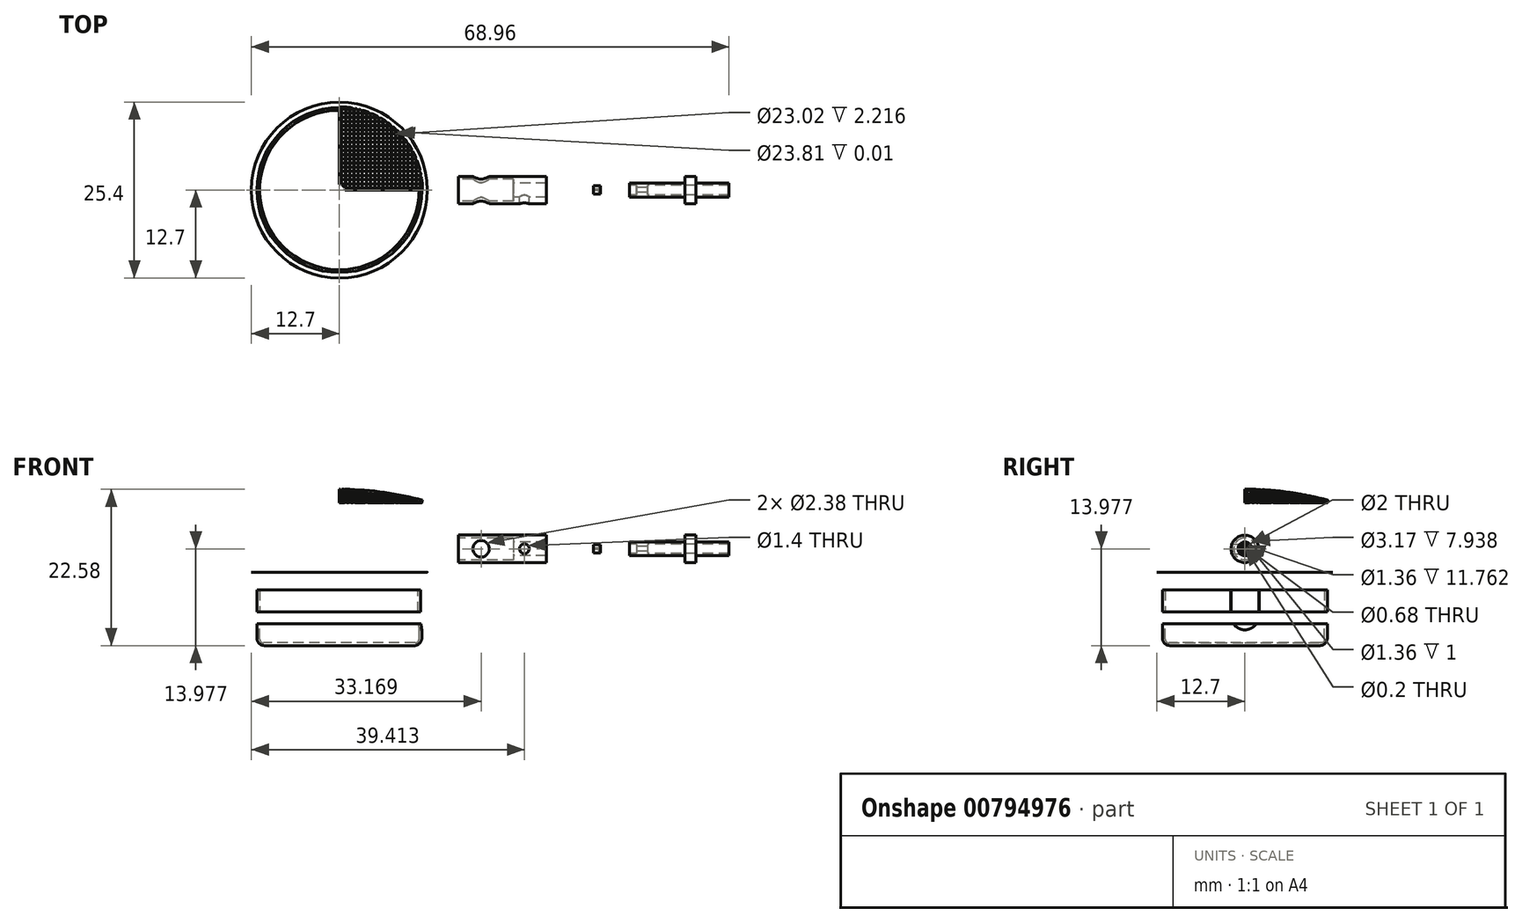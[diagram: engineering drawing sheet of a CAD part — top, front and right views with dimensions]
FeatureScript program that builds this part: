
annotation { "Feature Type Name" : "Feature", "Feature Type Description" : "" }
export const myFeature = defineFeature(function(context is Context, id is Id, definition is map)
    precondition{}
    {
        {
            var Q0;
            Q0=qCreatedBy(makeId("Right.planeOp"),FACE);
            cPlane(context, id + "F0", {"entities" : qUnion([Q0]), "cplaneType" : CPlaneType.OFFSET, "offset" : 15 * mm, "width" : 150 * mm, "height" : 150 * mm});
        }
        {
            var Q0;
            Q0=qCreatedBy(makeId("Front.planeOp"),FACE);
            var sketch = newSketch(context, id + "F1", { "sketchPlane" : qUnion([Q0])});
            skLineSegment(sketch, "E0", {"start": v(0, 0) * mm, "end": v(11.9, 0) * mm, "construction": true});
            skLineSegment(sketch, "E1", {"start": v(0, 0) * mm, "end": v(-11.9, 0) * mm, "construction": true});
            skLineSegment(sketch, "E2", {"start": v(0, 0) * mm, "end": v(0, 1.59) * mm, "construction": true});
            skArc(sketch, "E3", {"start": v(11.9, 0) * mm, "mid": v(0, 1.59) * mm, "end": v(-11.9, 0) * mm});
            skArc(sketch, "E4.0", {"start": v(12.01, 0.38) * mm, "mid": v(0, 1.98) * mm, "end": v(-12.01, 0.38) * mm});
            skLineSegment(sketch, "E5", {"start": v(12.01, 0.38) * mm, "end": v(11.9, 0) * mm});
            skLineSegment(sketch, "E6", {"start": v(0.8, 1.98) * mm, "end": v(0.8, 1.58) * mm});
            skSolve(sketch);
        }
        {
            var Q0;
            {var subQ0=sQuery(id+"F1.wireOp",EDGE,"E5");Q0=makeQuery(id+"F1.imprint","IMPRINT",FACE,{"disambiguationData":[TD([[makeQuery(id+"F1.imprint","IMPRINT",EDGE,{"derivedFrom":subQ0}),-1.0]])]});}
            var Q1;
            Q1=sQuery(id+"F1.wireOp",EDGE,"E2");
            revolve(context, id + "F2", {"surfaceOperationType" : NewSurfaceOperationType.NEW, "entities" : qUnion([Q0]), "axis" : qUnion([Q1]), "revolveType" : RevolveType.ONE_DIRECTION, "angle" : 90 * degree});
        }
        {
            var Q0;
            Q0=qCreatedBy(makeId("Top.planeOp"),FACE);
            var sketch = newSketch(context, id + "F3", { "sketchPlane" : qUnion([Q0])});
            skLineSegment(sketch, "E7.0.20.0", {"start": v(0.11, 11.5) * mm, "end": v(0.11, 11.9) * mm});
            skLineSegment(sketch, "E7.3.20.0", {"start": v(0.51, 11.5) * mm, "end": v(0.51, 11.9) * mm});
            skLineSegment(sketch, "E7.6.20.0", {"start": v(0.51, 11.9) * mm, "end": v(0.11, 11.9) * mm});
            skLineSegment(sketch, "E7.9.20.0", {"start": v(0.51, 11.5) * mm, "end": v(0.11, 11.5) * mm});
            skLineSegment(sketch, "E7.0.20.1", {"start": v(0.11, 10.9) * mm, "end": v(0.11, 11.3) * mm});
            skLineSegment(sketch, "E7.3.20.1", {"start": v(0.5, 10.9) * mm, "end": v(0.5, 11.3) * mm});
            skLineSegment(sketch, "E7.6.20.1", {"start": v(0.5, 11.3) * mm, "end": v(0.11, 11.3) * mm});
            skLineSegment(sketch, "E7.9.20.1", {"start": v(0.5, 10.9) * mm, "end": v(0.11, 10.9) * mm});
            skLineSegment(sketch, "E7.0.20.2", {"start": v(0.11, 10.3) * mm, "end": v(0.11, 10.7) * mm});
            skLineSegment(sketch, "E7.3.20.2", {"start": v(0.5, 10.3) * mm, "end": v(0.5, 10.7) * mm});
            skLineSegment(sketch, "E7.6.20.2", {"start": v(0.5, 10.7) * mm, "end": v(0.11, 10.7) * mm});
            skLineSegment(sketch, "E7.9.20.2", {"start": v(0.5, 10.3) * mm, "end": v(0.11, 10.3) * mm});
            skLineSegment(sketch, "E7.0.20.3", {"start": v(0.11, 9.7) * mm, "end": v(0.11, 10.1) * mm});
            skLineSegment(sketch, "E7.3.20.3", {"start": v(0.5, 9.7) * mm, "end": v(0.5, 10.1) * mm});
            skLineSegment(sketch, "E7.6.20.3", {"start": v(0.5, 10.1) * mm, "end": v(0.11, 10.1) * mm});
            skLineSegment(sketch, "E7.9.20.3", {"start": v(0.5, 9.7) * mm, "end": v(0.11, 9.7) * mm});
            skLineSegment(sketch, "E7.0.20.4", {"start": v(0.11, 9.1) * mm, "end": v(0.11, 9.5) * mm});
            skLineSegment(sketch, "E7.3.20.4", {"start": v(0.5, 9.1) * mm, "end": v(0.5, 9.5) * mm});
            skLineSegment(sketch, "E7.6.20.4", {"start": v(0.5, 9.5) * mm, "end": v(0.11, 9.5) * mm});
            skLineSegment(sketch, "E7.9.20.4", {"start": v(0.5, 9.1) * mm, "end": v(0.11, 9.1) * mm});
            skLineSegment(sketch, "E7.0.20.5", {"start": v(0.11, 8.5) * mm, "end": v(0.11, 8.9) * mm});
            skLineSegment(sketch, "E7.3.20.5", {"start": v(0.5, 8.5) * mm, "end": v(0.5, 8.9) * mm});
            skLineSegment(sketch, "E7.6.20.5", {"start": v(0.5, 8.9) * mm, "end": v(0.11, 8.9) * mm});
            skLineSegment(sketch, "E7.9.20.5", {"start": v(0.5, 8.5) * mm, "end": v(0.11, 8.5) * mm});
            skLineSegment(sketch, "E7.0.20.6", {"start": v(0.11, 7.9) * mm, "end": v(0.11, 8.3) * mm});
            skLineSegment(sketch, "E7.3.20.6", {"start": v(0.5, 7.9) * mm, "end": v(0.5, 8.3) * mm});
            skLineSegment(sketch, "E7.6.20.6", {"start": v(0.5, 8.3) * mm, "end": v(0.11, 8.3) * mm});
            skLineSegment(sketch, "E7.9.20.6", {"start": v(0.5, 7.9) * mm, "end": v(0.11, 7.9) * mm});
            skLineSegment(sketch, "E7.0.20.7", {"start": v(0.11, 7.3) * mm, "end": v(0.11, 7.7) * mm});
            skLineSegment(sketch, "E7.3.20.7", {"start": v(0.5, 7.3) * mm, "end": v(0.5, 7.7) * mm});
            skLineSegment(sketch, "E7.6.20.7", {"start": v(0.5, 7.7) * mm, "end": v(0.11, 7.7) * mm});
            skLineSegment(sketch, "E7.9.20.7", {"start": v(0.5, 7.3) * mm, "end": v(0.11, 7.3) * mm});
            skLineSegment(sketch, "E7.0.20.8", {"start": v(0.11, 6.7) * mm, "end": v(0.11, 7.1) * mm});
            skLineSegment(sketch, "E7.3.20.8", {"start": v(0.5, 6.7) * mm, "end": v(0.5, 7.1) * mm});
            skLineSegment(sketch, "E7.6.20.8", {"start": v(0.5, 7.1) * mm, "end": v(0.11, 7.1) * mm});
            skLineSegment(sketch, "E7.9.20.8", {"start": v(0.5, 6.7) * mm, "end": v(0.11, 6.7) * mm});
            skLineSegment(sketch, "E7.0.20.9", {"start": v(0.11, 6.1) * mm, "end": v(0.11, 6.5) * mm});
            skLineSegment(sketch, "E7.3.20.9", {"start": v(0.5, 6.1) * mm, "end": v(0.5, 6.5) * mm});
            skLineSegment(sketch, "E7.6.20.9", {"start": v(0.5, 6.5) * mm, "end": v(0.11, 6.5) * mm});
            skLineSegment(sketch, "E7.9.20.9", {"start": v(0.5, 6.1) * mm, "end": v(0.11, 6.1) * mm});
            skLineSegment(sketch, "E7.0.21.0", {"start": v(0.71, 11.5) * mm, "end": v(0.71, 11.9) * mm});
            skLineSegment(sketch, "E7.3.21.0", {"start": v(1.11, 11.5) * mm, "end": v(1.11, 11.9) * mm});
            skLineSegment(sketch, "E7.6.21.0", {"start": v(1.11, 11.9) * mm, "end": v(0.71, 11.9) * mm});
            skLineSegment(sketch, "E7.9.21.0", {"start": v(1.11, 11.5) * mm, "end": v(0.71, 11.5) * mm});
            skLineSegment(sketch, "E7.0.21.1", {"start": v(0.71, 10.9) * mm, "end": v(0.71, 11.3) * mm});
            skLineSegment(sketch, "E7.3.21.1", {"start": v(1.1, 10.9) * mm, "end": v(1.1, 11.3) * mm});
            skLineSegment(sketch, "E7.6.21.1", {"start": v(1.1, 11.3) * mm, "end": v(0.71, 11.3) * mm});
            skLineSegment(sketch, "E7.9.21.1", {"start": v(1.1, 10.9) * mm, "end": v(0.71, 10.9) * mm});
            skLineSegment(sketch, "E7.0.21.2", {"start": v(0.71, 10.3) * mm, "end": v(0.71, 10.7) * mm});
            skLineSegment(sketch, "E7.3.21.2", {"start": v(1.1, 10.3) * mm, "end": v(1.1, 10.7) * mm});
            skLineSegment(sketch, "E7.6.21.2", {"start": v(1.1, 10.7) * mm, "end": v(0.71, 10.7) * mm});
            skLineSegment(sketch, "E7.9.21.2", {"start": v(1.1, 10.3) * mm, "end": v(0.71, 10.3) * mm});
            skLineSegment(sketch, "E7.0.21.3", {"start": v(0.71, 9.7) * mm, "end": v(0.71, 10.1) * mm});
            skLineSegment(sketch, "E7.3.21.3", {"start": v(1.1, 9.7) * mm, "end": v(1.1, 10.1) * mm});
            skLineSegment(sketch, "E7.6.21.3", {"start": v(1.1, 10.1) * mm, "end": v(0.71, 10.1) * mm});
            skLineSegment(sketch, "E7.9.21.3", {"start": v(1.1, 9.7) * mm, "end": v(0.71, 9.7) * mm});
            skLineSegment(sketch, "E7.0.21.4", {"start": v(0.71, 9.1) * mm, "end": v(0.71, 9.5) * mm});
            skLineSegment(sketch, "E7.3.21.4", {"start": v(1.1, 9.1) * mm, "end": v(1.1, 9.5) * mm});
            skLineSegment(sketch, "E7.6.21.4", {"start": v(1.1, 9.5) * mm, "end": v(0.71, 9.5) * mm});
            skLineSegment(sketch, "E7.9.21.4", {"start": v(1.1, 9.1) * mm, "end": v(0.71, 9.1) * mm});
            skLineSegment(sketch, "E7.0.21.5", {"start": v(0.71, 8.5) * mm, "end": v(0.71, 8.9) * mm});
            skLineSegment(sketch, "E7.3.21.5", {"start": v(1.1, 8.5) * mm, "end": v(1.1, 8.9) * mm});
            skLineSegment(sketch, "E7.6.21.5", {"start": v(1.1, 8.9) * mm, "end": v(0.71, 8.9) * mm});
            skLineSegment(sketch, "E7.9.21.5", {"start": v(1.1, 8.5) * mm, "end": v(0.71, 8.5) * mm});
            skLineSegment(sketch, "E7.0.21.6", {"start": v(0.71, 7.9) * mm, "end": v(0.71, 8.3) * mm});
            skLineSegment(sketch, "E7.3.21.6", {"start": v(1.1, 7.9) * mm, "end": v(1.1, 8.3) * mm});
            skLineSegment(sketch, "E7.6.21.6", {"start": v(1.1, 8.3) * mm, "end": v(0.71, 8.3) * mm});
            skLineSegment(sketch, "E7.9.21.6", {"start": v(1.1, 7.9) * mm, "end": v(0.71, 7.9) * mm});
            skLineSegment(sketch, "E7.0.21.7", {"start": v(0.71, 7.3) * mm, "end": v(0.71, 7.7) * mm});
            skLineSegment(sketch, "E7.3.21.7", {"start": v(1.1, 7.3) * mm, "end": v(1.1, 7.7) * mm});
            skLineSegment(sketch, "E7.6.21.7", {"start": v(1.1, 7.7) * mm, "end": v(0.71, 7.7) * mm});
            skLineSegment(sketch, "E7.9.21.7", {"start": v(1.1, 7.3) * mm, "end": v(0.71, 7.3) * mm});
            skLineSegment(sketch, "E7.0.21.8", {"start": v(0.71, 6.7) * mm, "end": v(0.71, 7.1) * mm});
            skLineSegment(sketch, "E7.3.21.8", {"start": v(1.1, 6.7) * mm, "end": v(1.1, 7.1) * mm});
            skLineSegment(sketch, "E7.6.21.8", {"start": v(1.1, 7.1) * mm, "end": v(0.71, 7.1) * mm});
            skLineSegment(sketch, "E7.9.21.8", {"start": v(1.1, 6.7) * mm, "end": v(0.71, 6.7) * mm});
            skLineSegment(sketch, "E7.0.21.9", {"start": v(0.71, 6.1) * mm, "end": v(0.71, 6.5) * mm});
            skLineSegment(sketch, "E7.3.21.9", {"start": v(1.1, 6.1) * mm, "end": v(1.1, 6.5) * mm});
            skLineSegment(sketch, "E7.6.21.9", {"start": v(1.1, 6.5) * mm, "end": v(0.71, 6.5) * mm});
            skLineSegment(sketch, "E7.9.21.9", {"start": v(1.1, 6.1) * mm, "end": v(0.71, 6.1) * mm});
            skLineSegment(sketch, "E7.0.22.0", {"start": v(1.31, 11.5) * mm, "end": v(1.31, 11.9) * mm});
            skLineSegment(sketch, "E7.3.22.0", {"start": v(1.71, 11.5) * mm, "end": v(1.71, 11.9) * mm});
            skLineSegment(sketch, "E7.6.22.0", {"start": v(1.71, 11.9) * mm, "end": v(1.31, 11.9) * mm});
            skLineSegment(sketch, "E7.9.22.0", {"start": v(1.71, 11.5) * mm, "end": v(1.31, 11.5) * mm});
            skLineSegment(sketch, "E7.0.22.1", {"start": v(1.31, 10.9) * mm, "end": v(1.31, 11.3) * mm});
            skLineSegment(sketch, "E7.3.22.1", {"start": v(1.7, 10.9) * mm, "end": v(1.7, 11.3) * mm});
            skLineSegment(sketch, "E7.6.22.1", {"start": v(1.7, 11.3) * mm, "end": v(1.31, 11.3) * mm});
            skLineSegment(sketch, "E7.9.22.1", {"start": v(1.7, 10.9) * mm, "end": v(1.31, 10.9) * mm});
            skLineSegment(sketch, "E7.0.22.2", {"start": v(1.31, 10.3) * mm, "end": v(1.31, 10.7) * mm});
            skLineSegment(sketch, "E7.3.22.2", {"start": v(1.7, 10.3) * mm, "end": v(1.7, 10.7) * mm});
            skLineSegment(sketch, "E7.6.22.2", {"start": v(1.7, 10.7) * mm, "end": v(1.31, 10.7) * mm});
            skLineSegment(sketch, "E7.9.22.2", {"start": v(1.7, 10.3) * mm, "end": v(1.31, 10.3) * mm});
            skLineSegment(sketch, "E7.0.22.3", {"start": v(1.31, 9.7) * mm, "end": v(1.31, 10.1) * mm});
            skLineSegment(sketch, "E7.3.22.3", {"start": v(1.7, 9.7) * mm, "end": v(1.7, 10.1) * mm});
            skLineSegment(sketch, "E7.6.22.3", {"start": v(1.7, 10.1) * mm, "end": v(1.31, 10.1) * mm});
            skLineSegment(sketch, "E7.9.22.3", {"start": v(1.7, 9.7) * mm, "end": v(1.31, 9.7) * mm});
            skLineSegment(sketch, "E7.0.22.4", {"start": v(1.31, 9.1) * mm, "end": v(1.31, 9.5) * mm});
            skLineSegment(sketch, "E7.3.22.4", {"start": v(1.7, 9.1) * mm, "end": v(1.7, 9.5) * mm});
            skLineSegment(sketch, "E7.6.22.4", {"start": v(1.7, 9.5) * mm, "end": v(1.31, 9.5) * mm});
            skLineSegment(sketch, "E7.9.22.4", {"start": v(1.7, 9.1) * mm, "end": v(1.31, 9.1) * mm});
            skLineSegment(sketch, "E7.0.22.5", {"start": v(1.31, 8.5) * mm, "end": v(1.31, 8.9) * mm});
            skLineSegment(sketch, "E7.3.22.5", {"start": v(1.7, 8.5) * mm, "end": v(1.7, 8.9) * mm});
            skLineSegment(sketch, "E7.6.22.5", {"start": v(1.7, 8.9) * mm, "end": v(1.31, 8.9) * mm});
            skLineSegment(sketch, "E7.9.22.5", {"start": v(1.7, 8.5) * mm, "end": v(1.31, 8.5) * mm});
            skLineSegment(sketch, "E7.0.22.6", {"start": v(1.31, 7.9) * mm, "end": v(1.31, 8.3) * mm});
            skLineSegment(sketch, "E7.3.22.6", {"start": v(1.7, 7.9) * mm, "end": v(1.7, 8.3) * mm});
            skLineSegment(sketch, "E7.6.22.6", {"start": v(1.7, 8.3) * mm, "end": v(1.31, 8.3) * mm});
            skLineSegment(sketch, "E7.9.22.6", {"start": v(1.7, 7.9) * mm, "end": v(1.31, 7.9) * mm});
            skLineSegment(sketch, "E7.0.22.7", {"start": v(1.31, 7.3) * mm, "end": v(1.31, 7.7) * mm});
            skLineSegment(sketch, "E7.3.22.7", {"start": v(1.7, 7.3) * mm, "end": v(1.7, 7.7) * mm});
            skLineSegment(sketch, "E7.6.22.7", {"start": v(1.7, 7.7) * mm, "end": v(1.31, 7.7) * mm});
            skLineSegment(sketch, "E7.9.22.7", {"start": v(1.7, 7.3) * mm, "end": v(1.31, 7.3) * mm});
            skLineSegment(sketch, "E7.0.22.8", {"start": v(1.31, 6.7) * mm, "end": v(1.31, 7.1) * mm});
            skLineSegment(sketch, "E7.3.22.8", {"start": v(1.7, 6.7) * mm, "end": v(1.7, 7.1) * mm});
            skLineSegment(sketch, "E7.6.22.8", {"start": v(1.7, 7.1) * mm, "end": v(1.31, 7.1) * mm});
            skLineSegment(sketch, "E7.9.22.8", {"start": v(1.7, 6.7) * mm, "end": v(1.31, 6.7) * mm});
            skLineSegment(sketch, "E7.0.22.9", {"start": v(1.31, 6.1) * mm, "end": v(1.31, 6.5) * mm});
            skLineSegment(sketch, "E7.3.22.9", {"start": v(1.7, 6.1) * mm, "end": v(1.7, 6.5) * mm});
            skLineSegment(sketch, "E7.6.22.9", {"start": v(1.7, 6.5) * mm, "end": v(1.31, 6.5) * mm});
            skLineSegment(sketch, "E7.9.22.9", {"start": v(1.7, 6.1) * mm, "end": v(1.31, 6.1) * mm});
            skLineSegment(sketch, "E7.0.23.0", {"start": v(1.91, 11.5) * mm, "end": v(1.91, 11.9) * mm});
            skLineSegment(sketch, "E7.3.23.0", {"start": v(2.31, 11.5) * mm, "end": v(2.31, 11.9) * mm});
            skLineSegment(sketch, "E7.6.23.0", {"start": v(2.31, 11.9) * mm, "end": v(1.91, 11.9) * mm});
            skLineSegment(sketch, "E7.9.23.0", {"start": v(2.31, 11.5) * mm, "end": v(1.91, 11.5) * mm});
            skLineSegment(sketch, "E7.0.23.1", {"start": v(1.91, 10.9) * mm, "end": v(1.91, 11.3) * mm});
            skLineSegment(sketch, "E7.3.23.1", {"start": v(2.3, 10.9) * mm, "end": v(2.3, 11.3) * mm});
            skLineSegment(sketch, "E7.6.23.1", {"start": v(2.3, 11.3) * mm, "end": v(1.91, 11.3) * mm});
            skLineSegment(sketch, "E7.9.23.1", {"start": v(2.3, 10.9) * mm, "end": v(1.91, 10.9) * mm});
            skLineSegment(sketch, "E7.0.23.2", {"start": v(1.91, 10.3) * mm, "end": v(1.91, 10.7) * mm});
            skLineSegment(sketch, "E7.3.23.2", {"start": v(2.3, 10.3) * mm, "end": v(2.3, 10.7) * mm});
            skLineSegment(sketch, "E7.6.23.2", {"start": v(2.3, 10.7) * mm, "end": v(1.91, 10.7) * mm});
            skLineSegment(sketch, "E7.9.23.2", {"start": v(2.3, 10.3) * mm, "end": v(1.91, 10.3) * mm});
            skLineSegment(sketch, "E7.0.23.3", {"start": v(1.91, 9.7) * mm, "end": v(1.91, 10.1) * mm});
            skLineSegment(sketch, "E7.3.23.3", {"start": v(2.3, 9.7) * mm, "end": v(2.3, 10.1) * mm});
            skLineSegment(sketch, "E7.6.23.3", {"start": v(2.3, 10.1) * mm, "end": v(1.91, 10.1) * mm});
            skLineSegment(sketch, "E7.9.23.3", {"start": v(2.3, 9.7) * mm, "end": v(1.91, 9.7) * mm});
            skLineSegment(sketch, "E7.0.23.4", {"start": v(1.91, 9.1) * mm, "end": v(1.91, 9.5) * mm});
            skLineSegment(sketch, "E7.3.23.4", {"start": v(2.3, 9.1) * mm, "end": v(2.3, 9.5) * mm});
            skLineSegment(sketch, "E7.6.23.4", {"start": v(2.3, 9.5) * mm, "end": v(1.91, 9.5) * mm});
            skLineSegment(sketch, "E7.9.23.4", {"start": v(2.3, 9.1) * mm, "end": v(1.91, 9.1) * mm});
            skLineSegment(sketch, "E7.0.23.5", {"start": v(1.91, 8.5) * mm, "end": v(1.91, 8.9) * mm});
            skLineSegment(sketch, "E7.3.23.5", {"start": v(2.3, 8.5) * mm, "end": v(2.3, 8.9) * mm});
            skLineSegment(sketch, "E7.6.23.5", {"start": v(2.3, 8.9) * mm, "end": v(1.91, 8.9) * mm});
            skLineSegment(sketch, "E7.9.23.5", {"start": v(2.3, 8.5) * mm, "end": v(1.91, 8.5) * mm});
            skLineSegment(sketch, "E7.0.23.6", {"start": v(1.91, 7.9) * mm, "end": v(1.91, 8.3) * mm});
            skLineSegment(sketch, "E7.3.23.6", {"start": v(2.3, 7.9) * mm, "end": v(2.3, 8.3) * mm});
            skLineSegment(sketch, "E7.6.23.6", {"start": v(2.3, 8.3) * mm, "end": v(1.91, 8.3) * mm});
            skLineSegment(sketch, "E7.9.23.6", {"start": v(2.3, 7.9) * mm, "end": v(1.91, 7.9) * mm});
            skLineSegment(sketch, "E7.0.23.7", {"start": v(1.91, 7.3) * mm, "end": v(1.91, 7.7) * mm});
            skLineSegment(sketch, "E7.3.23.7", {"start": v(2.3, 7.3) * mm, "end": v(2.3, 7.7) * mm});
            skLineSegment(sketch, "E7.6.23.7", {"start": v(2.3, 7.7) * mm, "end": v(1.91, 7.7) * mm});
            skLineSegment(sketch, "E7.9.23.7", {"start": v(2.3, 7.3) * mm, "end": v(1.91, 7.3) * mm});
            skLineSegment(sketch, "E7.0.23.8", {"start": v(1.91, 6.7) * mm, "end": v(1.91, 7.1) * mm});
            skLineSegment(sketch, "E7.3.23.8", {"start": v(2.3, 6.7) * mm, "end": v(2.3, 7.1) * mm});
            skLineSegment(sketch, "E7.6.23.8", {"start": v(2.3, 7.1) * mm, "end": v(1.91, 7.1) * mm});
            skLineSegment(sketch, "E7.9.23.8", {"start": v(2.3, 6.7) * mm, "end": v(1.91, 6.7) * mm});
            skLineSegment(sketch, "E7.0.23.9", {"start": v(1.91, 6.1) * mm, "end": v(1.91, 6.5) * mm});
            skLineSegment(sketch, "E7.3.23.9", {"start": v(2.3, 6.1) * mm, "end": v(2.3, 6.5) * mm});
            skLineSegment(sketch, "E7.6.23.9", {"start": v(2.3, 6.5) * mm, "end": v(1.91, 6.5) * mm});
            skLineSegment(sketch, "E7.9.23.9", {"start": v(2.3, 6.1) * mm, "end": v(1.91, 6.1) * mm});
            skLineSegment(sketch, "E7.0.24.0", {"start": v(2.51, 11.5) * mm, "end": v(2.51, 11.9) * mm});
            skLineSegment(sketch, "E7.3.24.0", {"start": v(2.91, 11.5) * mm, "end": v(2.91, 11.9) * mm});
            skLineSegment(sketch, "E7.6.24.0", {"start": v(2.91, 11.9) * mm, "end": v(2.51, 11.9) * mm});
            skLineSegment(sketch, "E7.9.24.0", {"start": v(2.91, 11.5) * mm, "end": v(2.51, 11.5) * mm});
            skLineSegment(sketch, "E7.0.24.1", {"start": v(2.51, 10.9) * mm, "end": v(2.51, 11.3) * mm});
            skLineSegment(sketch, "E7.3.24.1", {"start": v(2.9, 10.9) * mm, "end": v(2.9, 11.3) * mm});
            skLineSegment(sketch, "E7.6.24.1", {"start": v(2.9, 11.3) * mm, "end": v(2.51, 11.3) * mm});
            skLineSegment(sketch, "E7.9.24.1", {"start": v(2.9, 10.9) * mm, "end": v(2.51, 10.9) * mm});
            skLineSegment(sketch, "E7.0.24.2", {"start": v(2.51, 10.3) * mm, "end": v(2.51, 10.7) * mm});
            skLineSegment(sketch, "E7.3.24.2", {"start": v(2.9, 10.3) * mm, "end": v(2.9, 10.7) * mm});
            skLineSegment(sketch, "E7.6.24.2", {"start": v(2.9, 10.7) * mm, "end": v(2.51, 10.7) * mm});
            skLineSegment(sketch, "E7.9.24.2", {"start": v(2.9, 10.3) * mm, "end": v(2.51, 10.3) * mm});
            skLineSegment(sketch, "E7.0.24.3", {"start": v(2.51, 9.7) * mm, "end": v(2.51, 10.1) * mm});
            skLineSegment(sketch, "E7.3.24.3", {"start": v(2.9, 9.7) * mm, "end": v(2.9, 10.1) * mm});
            skLineSegment(sketch, "E7.6.24.3", {"start": v(2.9, 10.1) * mm, "end": v(2.51, 10.1) * mm});
            skLineSegment(sketch, "E7.9.24.3", {"start": v(2.9, 9.7) * mm, "end": v(2.51, 9.7) * mm});
            skLineSegment(sketch, "E7.0.24.4", {"start": v(2.51, 9.1) * mm, "end": v(2.51, 9.5) * mm});
            skLineSegment(sketch, "E7.3.24.4", {"start": v(2.9, 9.1) * mm, "end": v(2.9, 9.5) * mm});
            skLineSegment(sketch, "E7.6.24.4", {"start": v(2.9, 9.5) * mm, "end": v(2.51, 9.5) * mm});
            skLineSegment(sketch, "E7.9.24.4", {"start": v(2.9, 9.1) * mm, "end": v(2.51, 9.1) * mm});
            skLineSegment(sketch, "E7.0.24.5", {"start": v(2.51, 8.5) * mm, "end": v(2.51, 8.9) * mm});
            skLineSegment(sketch, "E7.3.24.5", {"start": v(2.9, 8.5) * mm, "end": v(2.9, 8.9) * mm});
            skLineSegment(sketch, "E7.6.24.5", {"start": v(2.9, 8.9) * mm, "end": v(2.51, 8.9) * mm});
            skLineSegment(sketch, "E7.9.24.5", {"start": v(2.9, 8.5) * mm, "end": v(2.51, 8.5) * mm});
            skLineSegment(sketch, "E7.0.24.6", {"start": v(2.51, 7.9) * mm, "end": v(2.51, 8.3) * mm});
            skLineSegment(sketch, "E7.3.24.6", {"start": v(2.9, 7.9) * mm, "end": v(2.9, 8.3) * mm});
            skLineSegment(sketch, "E7.6.24.6", {"start": v(2.9, 8.3) * mm, "end": v(2.51, 8.3) * mm});
            skLineSegment(sketch, "E7.9.24.6", {"start": v(2.9, 7.9) * mm, "end": v(2.51, 7.9) * mm});
            skLineSegment(sketch, "E7.0.24.7", {"start": v(2.51, 7.3) * mm, "end": v(2.51, 7.7) * mm});
            skLineSegment(sketch, "E7.3.24.7", {"start": v(2.9, 7.3) * mm, "end": v(2.9, 7.7) * mm});
            skLineSegment(sketch, "E7.6.24.7", {"start": v(2.9, 7.7) * mm, "end": v(2.51, 7.7) * mm});
            skLineSegment(sketch, "E7.9.24.7", {"start": v(2.9, 7.3) * mm, "end": v(2.51, 7.3) * mm});
            skLineSegment(sketch, "E7.0.24.8", {"start": v(2.51, 6.7) * mm, "end": v(2.51, 7.1) * mm});
            skLineSegment(sketch, "E7.3.24.8", {"start": v(2.9, 6.7) * mm, "end": v(2.9, 7.1) * mm});
            skLineSegment(sketch, "E7.6.24.8", {"start": v(2.9, 7.1) * mm, "end": v(2.51, 7.1) * mm});
            skLineSegment(sketch, "E7.9.24.8", {"start": v(2.9, 6.7) * mm, "end": v(2.51, 6.7) * mm});
            skLineSegment(sketch, "E7.0.24.9", {"start": v(2.51, 6.1) * mm, "end": v(2.51, 6.5) * mm});
            skLineSegment(sketch, "E7.3.24.9", {"start": v(2.9, 6.1) * mm, "end": v(2.9, 6.5) * mm});
            skLineSegment(sketch, "E7.6.24.9", {"start": v(2.9, 6.5) * mm, "end": v(2.51, 6.5) * mm});
            skLineSegment(sketch, "E7.9.24.9", {"start": v(2.9, 6.1) * mm, "end": v(2.51, 6.1) * mm});
            skLineSegment(sketch, "E7.0.25.0", {"start": v(3.11, 11.5) * mm, "end": v(3.11, 11.9) * mm});
            skLineSegment(sketch, "E7.3.25.0", {"start": v(3.51, 11.5) * mm, "end": v(3.51, 11.9) * mm});
            skLineSegment(sketch, "E7.6.25.0", {"start": v(3.51, 11.9) * mm, "end": v(3.11, 11.9) * mm});
            skLineSegment(sketch, "E7.9.25.0", {"start": v(3.51, 11.5) * mm, "end": v(3.11, 11.5) * mm});
            skLineSegment(sketch, "E7.0.25.1", {"start": v(3.11, 10.9) * mm, "end": v(3.11, 11.3) * mm});
            skLineSegment(sketch, "E7.3.25.1", {"start": v(3.5, 10.9) * mm, "end": v(3.5, 11.3) * mm});
            skLineSegment(sketch, "E7.6.25.1", {"start": v(3.5, 11.3) * mm, "end": v(3.11, 11.3) * mm});
            skLineSegment(sketch, "E7.9.25.1", {"start": v(3.5, 10.9) * mm, "end": v(3.11, 10.9) * mm});
            skLineSegment(sketch, "E7.0.25.2", {"start": v(3.11, 10.3) * mm, "end": v(3.11, 10.7) * mm});
            skLineSegment(sketch, "E7.3.25.2", {"start": v(3.5, 10.3) * mm, "end": v(3.5, 10.7) * mm});
            skLineSegment(sketch, "E7.6.25.2", {"start": v(3.5, 10.7) * mm, "end": v(3.11, 10.7) * mm});
            skLineSegment(sketch, "E7.9.25.2", {"start": v(3.5, 10.3) * mm, "end": v(3.11, 10.3) * mm});
            skLineSegment(sketch, "E7.0.25.3", {"start": v(3.11, 9.7) * mm, "end": v(3.11, 10.1) * mm});
            skLineSegment(sketch, "E7.3.25.3", {"start": v(3.5, 9.7) * mm, "end": v(3.5, 10.1) * mm});
            skLineSegment(sketch, "E7.6.25.3", {"start": v(3.5, 10.1) * mm, "end": v(3.11, 10.1) * mm});
            skLineSegment(sketch, "E7.9.25.3", {"start": v(3.5, 9.7) * mm, "end": v(3.11, 9.7) * mm});
            skLineSegment(sketch, "E7.0.25.4", {"start": v(3.11, 9.1) * mm, "end": v(3.11, 9.5) * mm});
            skLineSegment(sketch, "E7.3.25.4", {"start": v(3.5, 9.1) * mm, "end": v(3.5, 9.5) * mm});
            skLineSegment(sketch, "E7.6.25.4", {"start": v(3.5, 9.5) * mm, "end": v(3.11, 9.5) * mm});
            skLineSegment(sketch, "E7.9.25.4", {"start": v(3.5, 9.1) * mm, "end": v(3.11, 9.1) * mm});
            skLineSegment(sketch, "E7.0.25.5", {"start": v(3.11, 8.5) * mm, "end": v(3.11, 8.9) * mm});
            skLineSegment(sketch, "E7.3.25.5", {"start": v(3.5, 8.5) * mm, "end": v(3.5, 8.9) * mm});
            skLineSegment(sketch, "E7.6.25.5", {"start": v(3.5, 8.9) * mm, "end": v(3.11, 8.9) * mm});
            skLineSegment(sketch, "E7.9.25.5", {"start": v(3.5, 8.5) * mm, "end": v(3.11, 8.5) * mm});
            skLineSegment(sketch, "E7.0.25.6", {"start": v(3.11, 7.9) * mm, "end": v(3.11, 8.3) * mm});
            skLineSegment(sketch, "E7.3.25.6", {"start": v(3.5, 7.9) * mm, "end": v(3.5, 8.3) * mm});
            skLineSegment(sketch, "E7.6.25.6", {"start": v(3.5, 8.3) * mm, "end": v(3.11, 8.3) * mm});
            skLineSegment(sketch, "E7.9.25.6", {"start": v(3.5, 7.9) * mm, "end": v(3.11, 7.9) * mm});
            skLineSegment(sketch, "E7.0.25.7", {"start": v(3.11, 7.3) * mm, "end": v(3.11, 7.7) * mm});
            skLineSegment(sketch, "E7.3.25.7", {"start": v(3.5, 7.3) * mm, "end": v(3.5, 7.7) * mm});
            skLineSegment(sketch, "E7.6.25.7", {"start": v(3.5, 7.7) * mm, "end": v(3.11, 7.7) * mm});
            skLineSegment(sketch, "E7.9.25.7", {"start": v(3.5, 7.3) * mm, "end": v(3.11, 7.3) * mm});
            skLineSegment(sketch, "E7.0.25.8", {"start": v(3.11, 6.7) * mm, "end": v(3.11, 7.1) * mm});
            skLineSegment(sketch, "E7.3.25.8", {"start": v(3.5, 6.7) * mm, "end": v(3.5, 7.1) * mm});
            skLineSegment(sketch, "E7.6.25.8", {"start": v(3.5, 7.1) * mm, "end": v(3.11, 7.1) * mm});
            skLineSegment(sketch, "E7.9.25.8", {"start": v(3.5, 6.7) * mm, "end": v(3.11, 6.7) * mm});
            skLineSegment(sketch, "E7.0.25.9", {"start": v(3.11, 6.1) * mm, "end": v(3.11, 6.5) * mm});
            skLineSegment(sketch, "E7.3.25.9", {"start": v(3.5, 6.1) * mm, "end": v(3.5, 6.5) * mm});
            skLineSegment(sketch, "E7.6.25.9", {"start": v(3.5, 6.5) * mm, "end": v(3.11, 6.5) * mm});
            skLineSegment(sketch, "E7.9.25.9", {"start": v(3.5, 6.1) * mm, "end": v(3.11, 6.1) * mm});
            skLineSegment(sketch, "E7.0.26.1", {"start": v(3.71, 10.9) * mm, "end": v(3.71, 11.3) * mm});
            skLineSegment(sketch, "E7.3.26.1", {"start": v(4.1, 10.9) * mm, "end": v(4.1, 11.3) * mm});
            skLineSegment(sketch, "E7.6.26.1", {"start": v(4.1, 11.3) * mm, "end": v(3.71, 11.3) * mm});
            skLineSegment(sketch, "E7.9.26.1", {"start": v(4.1, 10.9) * mm, "end": v(3.71, 10.9) * mm});
            skLineSegment(sketch, "E7.0.26.2", {"start": v(3.71, 10.3) * mm, "end": v(3.71, 10.7) * mm});
            skLineSegment(sketch, "E7.3.26.2", {"start": v(4.1, 10.3) * mm, "end": v(4.1, 10.7) * mm});
            skLineSegment(sketch, "E7.6.26.2", {"start": v(4.1, 10.7) * mm, "end": v(3.71, 10.7) * mm});
            skLineSegment(sketch, "E7.9.26.2", {"start": v(4.1, 10.3) * mm, "end": v(3.71, 10.3) * mm});
            skLineSegment(sketch, "E7.0.26.3", {"start": v(3.71, 9.7) * mm, "end": v(3.71, 10.1) * mm});
            skLineSegment(sketch, "E7.3.26.3", {"start": v(4.1, 9.7) * mm, "end": v(4.1, 10.1) * mm});
            skLineSegment(sketch, "E7.6.26.3", {"start": v(4.1, 10.1) * mm, "end": v(3.71, 10.1) * mm});
            skLineSegment(sketch, "E7.9.26.3", {"start": v(4.1, 9.7) * mm, "end": v(3.71, 9.7) * mm});
            skLineSegment(sketch, "E7.0.26.4", {"start": v(3.71, 9.1) * mm, "end": v(3.71, 9.5) * mm});
            skLineSegment(sketch, "E7.3.26.4", {"start": v(4.1, 9.1) * mm, "end": v(4.1, 9.5) * mm});
            skLineSegment(sketch, "E7.6.26.4", {"start": v(4.1, 9.5) * mm, "end": v(3.71, 9.5) * mm});
            skLineSegment(sketch, "E7.9.26.4", {"start": v(4.1, 9.1) * mm, "end": v(3.71, 9.1) * mm});
            skLineSegment(sketch, "E7.0.26.5", {"start": v(3.71, 8.5) * mm, "end": v(3.71, 8.9) * mm});
            skLineSegment(sketch, "E7.3.26.5", {"start": v(4.1, 8.5) * mm, "end": v(4.1, 8.9) * mm});
            skLineSegment(sketch, "E7.6.26.5", {"start": v(4.1, 8.9) * mm, "end": v(3.71, 8.9) * mm});
            skLineSegment(sketch, "E7.9.26.5", {"start": v(4.1, 8.5) * mm, "end": v(3.71, 8.5) * mm});
            skLineSegment(sketch, "E7.0.26.6", {"start": v(3.71, 7.9) * mm, "end": v(3.71, 8.3) * mm});
            skLineSegment(sketch, "E7.3.26.6", {"start": v(4.1, 7.9) * mm, "end": v(4.1, 8.3) * mm});
            skLineSegment(sketch, "E7.6.26.6", {"start": v(4.1, 8.3) * mm, "end": v(3.71, 8.3) * mm});
            skLineSegment(sketch, "E7.9.26.6", {"start": v(4.1, 7.9) * mm, "end": v(3.71, 7.9) * mm});
            skLineSegment(sketch, "E7.0.26.7", {"start": v(3.71, 7.3) * mm, "end": v(3.71, 7.7) * mm});
            skLineSegment(sketch, "E7.3.26.7", {"start": v(4.1, 7.3) * mm, "end": v(4.1, 7.7) * mm});
            skLineSegment(sketch, "E7.6.26.7", {"start": v(4.1, 7.7) * mm, "end": v(3.71, 7.7) * mm});
            skLineSegment(sketch, "E7.9.26.7", {"start": v(4.1, 7.3) * mm, "end": v(3.71, 7.3) * mm});
            skLineSegment(sketch, "E7.0.26.8", {"start": v(3.71, 6.7) * mm, "end": v(3.71, 7.1) * mm});
            skLineSegment(sketch, "E7.3.26.8", {"start": v(4.1, 6.7) * mm, "end": v(4.1, 7.1) * mm});
            skLineSegment(sketch, "E7.6.26.8", {"start": v(4.1, 7.1) * mm, "end": v(3.71, 7.1) * mm});
            skLineSegment(sketch, "E7.9.26.8", {"start": v(4.1, 6.7) * mm, "end": v(3.71, 6.7) * mm});
            skLineSegment(sketch, "E7.0.26.9", {"start": v(3.71, 6.1) * mm, "end": v(3.71, 6.5) * mm});
            skLineSegment(sketch, "E7.3.26.9", {"start": v(4.1, 6.1) * mm, "end": v(4.1, 6.5) * mm});
            skLineSegment(sketch, "E7.6.26.9", {"start": v(4.1, 6.5) * mm, "end": v(3.71, 6.5) * mm});
            skLineSegment(sketch, "E7.9.26.9", {"start": v(4.1, 6.1) * mm, "end": v(3.71, 6.1) * mm});
            skLineSegment(sketch, "E7.0.27.1", {"start": v(4.31, 10.9) * mm, "end": v(4.31, 11.3) * mm});
            skLineSegment(sketch, "E7.3.27.1", {"start": v(4.7, 10.9) * mm, "end": v(4.7, 11.3) * mm});
            skLineSegment(sketch, "E7.6.27.1", {"start": v(4.7, 11.3) * mm, "end": v(4.31, 11.3) * mm});
            skLineSegment(sketch, "E7.9.27.1", {"start": v(4.7, 10.9) * mm, "end": v(4.31, 10.9) * mm});
            skLineSegment(sketch, "E7.0.27.2", {"start": v(4.31, 10.3) * mm, "end": v(4.31, 10.7) * mm});
            skLineSegment(sketch, "E7.3.27.2", {"start": v(4.7, 10.3) * mm, "end": v(4.7, 10.7) * mm});
            skLineSegment(sketch, "E7.6.27.2", {"start": v(4.7, 10.7) * mm, "end": v(4.31, 10.7) * mm});
            skLineSegment(sketch, "E7.9.27.2", {"start": v(4.7, 10.3) * mm, "end": v(4.31, 10.3) * mm});
            skLineSegment(sketch, "E7.0.27.3", {"start": v(4.31, 9.7) * mm, "end": v(4.31, 10.1) * mm});
            skLineSegment(sketch, "E7.3.27.3", {"start": v(4.7, 9.7) * mm, "end": v(4.7, 10.1) * mm});
            skLineSegment(sketch, "E7.6.27.3", {"start": v(4.7, 10.1) * mm, "end": v(4.31, 10.1) * mm});
            skLineSegment(sketch, "E7.9.27.3", {"start": v(4.7, 9.7) * mm, "end": v(4.31, 9.7) * mm});
            skLineSegment(sketch, "E7.0.27.4", {"start": v(4.31, 9.1) * mm, "end": v(4.31, 9.5) * mm});
            skLineSegment(sketch, "E7.3.27.4", {"start": v(4.7, 9.1) * mm, "end": v(4.7, 9.5) * mm});
            skLineSegment(sketch, "E7.6.27.4", {"start": v(4.7, 9.5) * mm, "end": v(4.31, 9.5) * mm});
            skLineSegment(sketch, "E7.9.27.4", {"start": v(4.7, 9.1) * mm, "end": v(4.31, 9.1) * mm});
            skLineSegment(sketch, "E7.0.27.5", {"start": v(4.31, 8.5) * mm, "end": v(4.31, 8.9) * mm});
            skLineSegment(sketch, "E7.3.27.5", {"start": v(4.7, 8.5) * mm, "end": v(4.7, 8.9) * mm});
            skLineSegment(sketch, "E7.6.27.5", {"start": v(4.7, 8.9) * mm, "end": v(4.31, 8.9) * mm});
            skLineSegment(sketch, "E7.9.27.5", {"start": v(4.7, 8.5) * mm, "end": v(4.31, 8.5) * mm});
            skLineSegment(sketch, "E7.0.27.6", {"start": v(4.31, 7.9) * mm, "end": v(4.31, 8.3) * mm});
            skLineSegment(sketch, "E7.3.27.6", {"start": v(4.7, 7.9) * mm, "end": v(4.7, 8.3) * mm});
            skLineSegment(sketch, "E7.6.27.6", {"start": v(4.7, 8.3) * mm, "end": v(4.31, 8.3) * mm});
            skLineSegment(sketch, "E7.9.27.6", {"start": v(4.7, 7.9) * mm, "end": v(4.31, 7.9) * mm});
            skLineSegment(sketch, "E7.0.27.7", {"start": v(4.31, 7.3) * mm, "end": v(4.31, 7.7) * mm});
            skLineSegment(sketch, "E7.3.27.7", {"start": v(4.7, 7.3) * mm, "end": v(4.7, 7.7) * mm});
            skLineSegment(sketch, "E7.6.27.7", {"start": v(4.7, 7.7) * mm, "end": v(4.31, 7.7) * mm});
            skLineSegment(sketch, "E7.9.27.7", {"start": v(4.7, 7.3) * mm, "end": v(4.31, 7.3) * mm});
            skLineSegment(sketch, "E7.0.27.8", {"start": v(4.31, 6.7) * mm, "end": v(4.31, 7.1) * mm});
            skLineSegment(sketch, "E7.3.27.8", {"start": v(4.7, 6.7) * mm, "end": v(4.7, 7.1) * mm});
            skLineSegment(sketch, "E7.6.27.8", {"start": v(4.7, 7.1) * mm, "end": v(4.31, 7.1) * mm});
            skLineSegment(sketch, "E7.9.27.8", {"start": v(4.7, 6.7) * mm, "end": v(4.31, 6.7) * mm});
            skLineSegment(sketch, "E7.0.27.9", {"start": v(4.31, 6.1) * mm, "end": v(4.31, 6.5) * mm});
            skLineSegment(sketch, "E7.3.27.9", {"start": v(4.7, 6.1) * mm, "end": v(4.7, 6.5) * mm});
            skLineSegment(sketch, "E7.6.27.9", {"start": v(4.7, 6.5) * mm, "end": v(4.31, 6.5) * mm});
            skLineSegment(sketch, "E7.9.27.9", {"start": v(4.7, 6.1) * mm, "end": v(4.31, 6.1) * mm});
            skLineSegment(sketch, "E7.0.28.2", {"start": v(4.91, 10.3) * mm, "end": v(4.91, 10.7) * mm});
            skLineSegment(sketch, "E7.3.28.2", {"start": v(5.3, 10.3) * mm, "end": v(5.3, 10.7) * mm});
            skLineSegment(sketch, "E7.6.28.2", {"start": v(5.3, 10.7) * mm, "end": v(4.91, 10.7) * mm});
            skLineSegment(sketch, "E7.9.28.2", {"start": v(5.3, 10.3) * mm, "end": v(4.91, 10.3) * mm});
            skLineSegment(sketch, "E7.0.28.3", {"start": v(4.91, 9.7) * mm, "end": v(4.91, 10.1) * mm});
            skLineSegment(sketch, "E7.3.28.3", {"start": v(5.3, 9.7) * mm, "end": v(5.3, 10.1) * mm});
            skLineSegment(sketch, "E7.6.28.3", {"start": v(5.3, 10.1) * mm, "end": v(4.91, 10.1) * mm});
            skLineSegment(sketch, "E7.9.28.3", {"start": v(5.3, 9.7) * mm, "end": v(4.91, 9.7) * mm});
            skLineSegment(sketch, "E7.0.28.4", {"start": v(4.91, 9.1) * mm, "end": v(4.91, 9.5) * mm});
            skLineSegment(sketch, "E7.3.28.4", {"start": v(5.3, 9.1) * mm, "end": v(5.3, 9.5) * mm});
            skLineSegment(sketch, "E7.6.28.4", {"start": v(5.3, 9.5) * mm, "end": v(4.91, 9.5) * mm});
            skLineSegment(sketch, "E7.9.28.4", {"start": v(5.3, 9.1) * mm, "end": v(4.91, 9.1) * mm});
            skLineSegment(sketch, "E7.0.28.5", {"start": v(4.91, 8.5) * mm, "end": v(4.91, 8.9) * mm});
            skLineSegment(sketch, "E7.3.28.5", {"start": v(5.3, 8.5) * mm, "end": v(5.3, 8.9) * mm});
            skLineSegment(sketch, "E7.6.28.5", {"start": v(5.3, 8.9) * mm, "end": v(4.91, 8.9) * mm});
            skLineSegment(sketch, "E7.9.28.5", {"start": v(5.3, 8.5) * mm, "end": v(4.91, 8.5) * mm});
            skLineSegment(sketch, "E7.0.28.6", {"start": v(4.91, 7.9) * mm, "end": v(4.91, 8.3) * mm});
            skLineSegment(sketch, "E7.3.28.6", {"start": v(5.3, 7.9) * mm, "end": v(5.3, 8.3) * mm});
            skLineSegment(sketch, "E7.6.28.6", {"start": v(5.3, 8.3) * mm, "end": v(4.91, 8.3) * mm});
            skLineSegment(sketch, "E7.9.28.6", {"start": v(5.3, 7.9) * mm, "end": v(4.91, 7.9) * mm});
            skLineSegment(sketch, "E7.0.28.7", {"start": v(4.91, 7.3) * mm, "end": v(4.91, 7.7) * mm});
            skLineSegment(sketch, "E7.3.28.7", {"start": v(5.3, 7.3) * mm, "end": v(5.3, 7.7) * mm});
            skLineSegment(sketch, "E7.6.28.7", {"start": v(5.3, 7.7) * mm, "end": v(4.91, 7.7) * mm});
            skLineSegment(sketch, "E7.9.28.7", {"start": v(5.3, 7.3) * mm, "end": v(4.91, 7.3) * mm});
            skLineSegment(sketch, "E7.0.28.8", {"start": v(4.91, 6.7) * mm, "end": v(4.91, 7.1) * mm});
            skLineSegment(sketch, "E7.3.28.8", {"start": v(5.3, 6.7) * mm, "end": v(5.3, 7.1) * mm});
            skLineSegment(sketch, "E7.6.28.8", {"start": v(5.3, 7.1) * mm, "end": v(4.91, 7.1) * mm});
            skLineSegment(sketch, "E7.9.28.8", {"start": v(5.3, 6.7) * mm, "end": v(4.91, 6.7) * mm});
            skLineSegment(sketch, "E7.0.28.9", {"start": v(4.91, 6.1) * mm, "end": v(4.91, 6.5) * mm});
            skLineSegment(sketch, "E7.3.28.9", {"start": v(5.3, 6.1) * mm, "end": v(5.3, 6.5) * mm});
            skLineSegment(sketch, "E7.6.28.9", {"start": v(5.3, 6.5) * mm, "end": v(4.91, 6.5) * mm});
            skLineSegment(sketch, "E7.9.28.9", {"start": v(5.3, 6.1) * mm, "end": v(4.91, 6.1) * mm});
            skLineSegment(sketch, "E7.0.29.2", {"start": v(5.51, 10.3) * mm, "end": v(5.51, 10.7) * mm});
            skLineSegment(sketch, "E7.3.29.2", {"start": v(5.9, 10.3) * mm, "end": v(5.9, 10.7) * mm});
            skLineSegment(sketch, "E7.6.29.2", {"start": v(5.9, 10.7) * mm, "end": v(5.51, 10.7) * mm});
            skLineSegment(sketch, "E7.9.29.2", {"start": v(5.9, 10.3) * mm, "end": v(5.51, 10.3) * mm});
            skLineSegment(sketch, "E7.0.29.3", {"start": v(5.51, 9.7) * mm, "end": v(5.51, 10.1) * mm});
            skLineSegment(sketch, "E7.3.29.3", {"start": v(5.9, 9.7) * mm, "end": v(5.9, 10.1) * mm});
            skLineSegment(sketch, "E7.6.29.3", {"start": v(5.9, 10.1) * mm, "end": v(5.51, 10.1) * mm});
            skLineSegment(sketch, "E7.9.29.3", {"start": v(5.9, 9.7) * mm, "end": v(5.51, 9.7) * mm});
            skLineSegment(sketch, "E7.0.29.4", {"start": v(5.51, 9.1) * mm, "end": v(5.51, 9.5) * mm});
            skLineSegment(sketch, "E7.3.29.4", {"start": v(5.9, 9.1) * mm, "end": v(5.9, 9.5) * mm});
            skLineSegment(sketch, "E7.6.29.4", {"start": v(5.9, 9.5) * mm, "end": v(5.51, 9.5) * mm});
            skLineSegment(sketch, "E7.9.29.4", {"start": v(5.9, 9.1) * mm, "end": v(5.51, 9.1) * mm});
            skLineSegment(sketch, "E7.0.29.5", {"start": v(5.51, 8.5) * mm, "end": v(5.51, 8.9) * mm});
            skLineSegment(sketch, "E7.3.29.5", {"start": v(5.9, 8.5) * mm, "end": v(5.9, 8.9) * mm});
            skLineSegment(sketch, "E7.6.29.5", {"start": v(5.9, 8.9) * mm, "end": v(5.51, 8.9) * mm});
            skLineSegment(sketch, "E7.9.29.5", {"start": v(5.9, 8.5) * mm, "end": v(5.51, 8.5) * mm});
            skLineSegment(sketch, "E7.0.29.6", {"start": v(5.51, 7.9) * mm, "end": v(5.51, 8.3) * mm});
            skLineSegment(sketch, "E7.3.29.6", {"start": v(5.9, 7.9) * mm, "end": v(5.9, 8.3) * mm});
            skLineSegment(sketch, "E7.6.29.6", {"start": v(5.9, 8.3) * mm, "end": v(5.51, 8.3) * mm});
            skLineSegment(sketch, "E7.9.29.6", {"start": v(5.9, 7.9) * mm, "end": v(5.51, 7.9) * mm});
            skLineSegment(sketch, "E7.0.29.7", {"start": v(5.51, 7.3) * mm, "end": v(5.51, 7.7) * mm});
            skLineSegment(sketch, "E7.3.29.7", {"start": v(5.9, 7.3) * mm, "end": v(5.9, 7.7) * mm});
            skLineSegment(sketch, "E7.6.29.7", {"start": v(5.9, 7.7) * mm, "end": v(5.51, 7.7) * mm});
            skLineSegment(sketch, "E7.9.29.7", {"start": v(5.9, 7.3) * mm, "end": v(5.51, 7.3) * mm});
            skLineSegment(sketch, "E7.0.29.8", {"start": v(5.51, 6.7) * mm, "end": v(5.51, 7.1) * mm});
            skLineSegment(sketch, "E7.3.29.8", {"start": v(5.9, 6.7) * mm, "end": v(5.9, 7.1) * mm});
            skLineSegment(sketch, "E7.6.29.8", {"start": v(5.9, 7.1) * mm, "end": v(5.51, 7.1) * mm});
            skLineSegment(sketch, "E7.9.29.8", {"start": v(5.9, 6.7) * mm, "end": v(5.51, 6.7) * mm});
            skLineSegment(sketch, "E7.0.29.9", {"start": v(5.51, 6.1) * mm, "end": v(5.51, 6.5) * mm});
            skLineSegment(sketch, "E7.3.29.9", {"start": v(5.9, 6.1) * mm, "end": v(5.9, 6.5) * mm});
            skLineSegment(sketch, "E7.6.29.9", {"start": v(5.9, 6.5) * mm, "end": v(5.51, 6.5) * mm});
            skLineSegment(sketch, "E7.9.29.9", {"start": v(5.9, 6.1) * mm, "end": v(5.51, 6.1) * mm});
            skLineSegment(sketch, "E7.0.30.3", {"start": v(6.11, 9.7) * mm, "end": v(6.11, 10.1) * mm});
            skLineSegment(sketch, "E7.3.30.3", {"start": v(6.5, 9.7) * mm, "end": v(6.5, 10.1) * mm});
            skLineSegment(sketch, "E7.6.30.3", {"start": v(6.5, 10.1) * mm, "end": v(6.11, 10.1) * mm});
            skLineSegment(sketch, "E7.9.30.3", {"start": v(6.5, 9.7) * mm, "end": v(6.11, 9.7) * mm});
            skLineSegment(sketch, "E7.0.30.4", {"start": v(6.11, 9.1) * mm, "end": v(6.11, 9.5) * mm});
            skLineSegment(sketch, "E7.3.30.4", {"start": v(6.5, 9.1) * mm, "end": v(6.5, 9.5) * mm});
            skLineSegment(sketch, "E7.6.30.4", {"start": v(6.5, 9.5) * mm, "end": v(6.11, 9.5) * mm});
            skLineSegment(sketch, "E7.9.30.4", {"start": v(6.5, 9.1) * mm, "end": v(6.11, 9.1) * mm});
            skLineSegment(sketch, "E7.0.30.5", {"start": v(6.11, 8.5) * mm, "end": v(6.11, 8.9) * mm});
            skLineSegment(sketch, "E7.3.30.5", {"start": v(6.5, 8.5) * mm, "end": v(6.5, 8.9) * mm});
            skLineSegment(sketch, "E7.6.30.5", {"start": v(6.5, 8.9) * mm, "end": v(6.11, 8.9) * mm});
            skLineSegment(sketch, "E7.9.30.5", {"start": v(6.5, 8.5) * mm, "end": v(6.11, 8.5) * mm});
            skLineSegment(sketch, "E7.0.30.6", {"start": v(6.11, 7.9) * mm, "end": v(6.11, 8.3) * mm});
            skLineSegment(sketch, "E7.3.30.6", {"start": v(6.5, 7.9) * mm, "end": v(6.5, 8.3) * mm});
            skLineSegment(sketch, "E7.6.30.6", {"start": v(6.5, 8.3) * mm, "end": v(6.11, 8.3) * mm});
            skLineSegment(sketch, "E7.9.30.6", {"start": v(6.5, 7.9) * mm, "end": v(6.11, 7.9) * mm});
            skLineSegment(sketch, "E7.0.30.7", {"start": v(6.11, 7.3) * mm, "end": v(6.11, 7.7) * mm});
            skLineSegment(sketch, "E7.3.30.7", {"start": v(6.5, 7.3) * mm, "end": v(6.5, 7.7) * mm});
            skLineSegment(sketch, "E7.6.30.7", {"start": v(6.5, 7.7) * mm, "end": v(6.11, 7.7) * mm});
            skLineSegment(sketch, "E7.9.30.7", {"start": v(6.5, 7.3) * mm, "end": v(6.11, 7.3) * mm});
            skLineSegment(sketch, "E7.0.30.8", {"start": v(6.11, 6.7) * mm, "end": v(6.11, 7.1) * mm});
            skLineSegment(sketch, "E7.3.30.8", {"start": v(6.5, 6.7) * mm, "end": v(6.5, 7.1) * mm});
            skLineSegment(sketch, "E7.6.30.8", {"start": v(6.5, 7.1) * mm, "end": v(6.11, 7.1) * mm});
            skLineSegment(sketch, "E7.9.30.8", {"start": v(6.5, 6.7) * mm, "end": v(6.11, 6.7) * mm});
            skLineSegment(sketch, "E7.0.30.9", {"start": v(6.11, 6.1) * mm, "end": v(6.11, 6.5) * mm});
            skLineSegment(sketch, "E7.3.30.9", {"start": v(6.5, 6.1) * mm, "end": v(6.5, 6.5) * mm});
            skLineSegment(sketch, "E7.6.30.9", {"start": v(6.5, 6.5) * mm, "end": v(6.11, 6.5) * mm});
            skLineSegment(sketch, "E7.9.30.9", {"start": v(6.5, 6.1) * mm, "end": v(6.11, 6.1) * mm});
            skLineSegment(sketch, "E7.0.31.3", {"start": v(6.71, 9.7) * mm, "end": v(6.71, 10.1) * mm});
            skLineSegment(sketch, "E7.3.31.3", {"start": v(7.1, 9.7) * mm, "end": v(7.1, 10.1) * mm});
            skLineSegment(sketch, "E7.6.31.3", {"start": v(7.1, 10.1) * mm, "end": v(6.71, 10.1) * mm});
            skLineSegment(sketch, "E7.9.31.3", {"start": v(7.1, 9.7) * mm, "end": v(6.71, 9.7) * mm});
            skLineSegment(sketch, "E7.0.31.4", {"start": v(6.71, 9.1) * mm, "end": v(6.71, 9.5) * mm});
            skLineSegment(sketch, "E7.3.31.4", {"start": v(7.1, 9.1) * mm, "end": v(7.1, 9.5) * mm});
            skLineSegment(sketch, "E7.6.31.4", {"start": v(7.1, 9.5) * mm, "end": v(6.71, 9.5) * mm});
            skLineSegment(sketch, "E7.9.31.4", {"start": v(7.1, 9.1) * mm, "end": v(6.71, 9.1) * mm});
            skLineSegment(sketch, "E7.0.31.5", {"start": v(6.71, 8.5) * mm, "end": v(6.71, 8.9) * mm});
            skLineSegment(sketch, "E7.3.31.5", {"start": v(7.1, 8.5) * mm, "end": v(7.1, 8.9) * mm});
            skLineSegment(sketch, "E7.6.31.5", {"start": v(7.1, 8.9) * mm, "end": v(6.71, 8.9) * mm});
            skLineSegment(sketch, "E7.9.31.5", {"start": v(7.1, 8.5) * mm, "end": v(6.71, 8.5) * mm});
            skLineSegment(sketch, "E7.0.31.6", {"start": v(6.71, 7.9) * mm, "end": v(6.71, 8.3) * mm});
            skLineSegment(sketch, "E7.3.31.6", {"start": v(7.1, 7.9) * mm, "end": v(7.1, 8.3) * mm});
            skLineSegment(sketch, "E7.6.31.6", {"start": v(7.1, 8.3) * mm, "end": v(6.71, 8.3) * mm});
            skLineSegment(sketch, "E7.9.31.6", {"start": v(7.1, 7.9) * mm, "end": v(6.71, 7.9) * mm});
            skLineSegment(sketch, "E7.0.31.7", {"start": v(6.71, 7.3) * mm, "end": v(6.71, 7.7) * mm});
            skLineSegment(sketch, "E7.3.31.7", {"start": v(7.1, 7.3) * mm, "end": v(7.1, 7.7) * mm});
            skLineSegment(sketch, "E7.6.31.7", {"start": v(7.1, 7.7) * mm, "end": v(6.71, 7.7) * mm});
            skLineSegment(sketch, "E7.9.31.7", {"start": v(7.1, 7.3) * mm, "end": v(6.71, 7.3) * mm});
            skLineSegment(sketch, "E7.0.31.8", {"start": v(6.71, 6.7) * mm, "end": v(6.71, 7.1) * mm});
            skLineSegment(sketch, "E7.3.31.8", {"start": v(7.1, 6.7) * mm, "end": v(7.1, 7.1) * mm});
            skLineSegment(sketch, "E7.6.31.8", {"start": v(7.1, 7.1) * mm, "end": v(6.71, 7.1) * mm});
            skLineSegment(sketch, "E7.9.31.8", {"start": v(7.1, 6.7) * mm, "end": v(6.71, 6.7) * mm});
            skLineSegment(sketch, "E7.0.31.9", {"start": v(6.71, 6.1) * mm, "end": v(6.71, 6.5) * mm});
            skLineSegment(sketch, "E7.3.31.9", {"start": v(7.1, 6.1) * mm, "end": v(7.1, 6.5) * mm});
            skLineSegment(sketch, "E7.6.31.9", {"start": v(7.1, 6.5) * mm, "end": v(6.71, 6.5) * mm});
            skLineSegment(sketch, "E7.9.31.9", {"start": v(7.1, 6.1) * mm, "end": v(6.71, 6.1) * mm});
            skLineSegment(sketch, "E7.0.32.4", {"start": v(7.31, 9.1) * mm, "end": v(7.31, 9.5) * mm});
            skLineSegment(sketch, "E7.3.32.4", {"start": v(7.7, 9.1) * mm, "end": v(7.7, 9.5) * mm});
            skLineSegment(sketch, "E7.6.32.4", {"start": v(7.7, 9.5) * mm, "end": v(7.31, 9.5) * mm});
            skLineSegment(sketch, "E7.9.32.4", {"start": v(7.7, 9.1) * mm, "end": v(7.31, 9.1) * mm});
            skLineSegment(sketch, "E7.0.32.5", {"start": v(7.31, 8.5) * mm, "end": v(7.31, 8.9) * mm});
            skLineSegment(sketch, "E7.3.32.5", {"start": v(7.7, 8.5) * mm, "end": v(7.7, 8.9) * mm});
            skLineSegment(sketch, "E7.6.32.5", {"start": v(7.7, 8.9) * mm, "end": v(7.31, 8.9) * mm});
            skLineSegment(sketch, "E7.9.32.5", {"start": v(7.7, 8.5) * mm, "end": v(7.31, 8.5) * mm});
            skLineSegment(sketch, "E7.0.32.6", {"start": v(7.31, 7.9) * mm, "end": v(7.31, 8.3) * mm});
            skLineSegment(sketch, "E7.3.32.6", {"start": v(7.7, 7.9) * mm, "end": v(7.7, 8.3) * mm});
            skLineSegment(sketch, "E7.6.32.6", {"start": v(7.7, 8.3) * mm, "end": v(7.31, 8.3) * mm});
            skLineSegment(sketch, "E7.9.32.6", {"start": v(7.7, 7.9) * mm, "end": v(7.31, 7.9) * mm});
            skLineSegment(sketch, "E7.0.32.7", {"start": v(7.31, 7.3) * mm, "end": v(7.31, 7.7) * mm});
            skLineSegment(sketch, "E7.3.32.7", {"start": v(7.7, 7.3) * mm, "end": v(7.7, 7.7) * mm});
            skLineSegment(sketch, "E7.6.32.7", {"start": v(7.7, 7.7) * mm, "end": v(7.31, 7.7) * mm});
            skLineSegment(sketch, "E7.9.32.7", {"start": v(7.7, 7.3) * mm, "end": v(7.31, 7.3) * mm});
            skLineSegment(sketch, "E7.0.32.8", {"start": v(7.31, 6.7) * mm, "end": v(7.31, 7.1) * mm});
            skLineSegment(sketch, "E7.3.32.8", {"start": v(7.7, 6.7) * mm, "end": v(7.7, 7.1) * mm});
            skLineSegment(sketch, "E7.6.32.8", {"start": v(7.7, 7.1) * mm, "end": v(7.31, 7.1) * mm});
            skLineSegment(sketch, "E7.9.32.8", {"start": v(7.7, 6.7) * mm, "end": v(7.31, 6.7) * mm});
            skLineSegment(sketch, "E7.0.32.9", {"start": v(7.31, 6.1) * mm, "end": v(7.31, 6.5) * mm});
            skLineSegment(sketch, "E7.3.32.9", {"start": v(7.7, 6.1) * mm, "end": v(7.7, 6.5) * mm});
            skLineSegment(sketch, "E7.6.32.9", {"start": v(7.7, 6.5) * mm, "end": v(7.31, 6.5) * mm});
            skLineSegment(sketch, "E7.9.32.9", {"start": v(7.7, 6.1) * mm, "end": v(7.31, 6.1) * mm});
            skLineSegment(sketch, "E7.0.33.5", {"start": v(7.91, 8.5) * mm, "end": v(7.91, 8.9) * mm});
            skLineSegment(sketch, "E7.3.33.5", {"start": v(8.3, 8.5) * mm, "end": v(8.3, 8.9) * mm});
            skLineSegment(sketch, "E7.6.33.5", {"start": v(8.3, 8.9) * mm, "end": v(7.91, 8.9) * mm});
            skLineSegment(sketch, "E7.9.33.5", {"start": v(8.3, 8.5) * mm, "end": v(7.91, 8.5) * mm});
            skLineSegment(sketch, "E7.0.33.6", {"start": v(7.91, 7.9) * mm, "end": v(7.91, 8.3) * mm});
            skLineSegment(sketch, "E7.3.33.6", {"start": v(8.3, 7.9) * mm, "end": v(8.3, 8.3) * mm});
            skLineSegment(sketch, "E7.6.33.6", {"start": v(8.3, 8.3) * mm, "end": v(7.91, 8.3) * mm});
            skLineSegment(sketch, "E7.9.33.6", {"start": v(8.3, 7.9) * mm, "end": v(7.91, 7.9) * mm});
            skLineSegment(sketch, "E7.0.33.7", {"start": v(7.91, 7.3) * mm, "end": v(7.91, 7.7) * mm});
            skLineSegment(sketch, "E7.3.33.7", {"start": v(8.3, 7.3) * mm, "end": v(8.3, 7.7) * mm});
            skLineSegment(sketch, "E7.6.33.7", {"start": v(8.3, 7.7) * mm, "end": v(7.91, 7.7) * mm});
            skLineSegment(sketch, "E7.9.33.7", {"start": v(8.3, 7.3) * mm, "end": v(7.91, 7.3) * mm});
            skLineSegment(sketch, "E7.0.33.8", {"start": v(7.91, 6.7) * mm, "end": v(7.91, 7.1) * mm});
            skLineSegment(sketch, "E7.3.33.8", {"start": v(8.3, 6.7) * mm, "end": v(8.3, 7.1) * mm});
            skLineSegment(sketch, "E7.6.33.8", {"start": v(8.3, 7.1) * mm, "end": v(7.91, 7.1) * mm});
            skLineSegment(sketch, "E7.9.33.8", {"start": v(8.3, 6.7) * mm, "end": v(7.91, 6.7) * mm});
            skLineSegment(sketch, "E7.0.33.9", {"start": v(7.91, 6.1) * mm, "end": v(7.91, 6.5) * mm});
            skLineSegment(sketch, "E7.3.33.9", {"start": v(8.3, 6.1) * mm, "end": v(8.3, 6.5) * mm});
            skLineSegment(sketch, "E7.6.33.9", {"start": v(8.3, 6.5) * mm, "end": v(7.91, 6.5) * mm});
            skLineSegment(sketch, "E7.9.33.9", {"start": v(8.3, 6.1) * mm, "end": v(7.91, 6.1) * mm});
            skLineSegment(sketch, "E7.0.34.6", {"start": v(8.51, 7.9) * mm, "end": v(8.51, 8.3) * mm});
            skLineSegment(sketch, "E7.3.34.6", {"start": v(8.9, 7.9) * mm, "end": v(8.9, 8.3) * mm});
            skLineSegment(sketch, "E7.6.34.6", {"start": v(8.9, 8.3) * mm, "end": v(8.51, 8.3) * mm});
            skLineSegment(sketch, "E7.9.34.6", {"start": v(8.9, 7.9) * mm, "end": v(8.51, 7.9) * mm});
            skLineSegment(sketch, "E7.0.34.7", {"start": v(8.51, 7.3) * mm, "end": v(8.51, 7.7) * mm});
            skLineSegment(sketch, "E7.3.34.7", {"start": v(8.9, 7.3) * mm, "end": v(8.9, 7.7) * mm});
            skLineSegment(sketch, "E7.6.34.7", {"start": v(8.9, 7.7) * mm, "end": v(8.51, 7.7) * mm});
            skLineSegment(sketch, "E7.9.34.7", {"start": v(8.9, 7.3) * mm, "end": v(8.51, 7.3) * mm});
            skLineSegment(sketch, "E7.0.34.8", {"start": v(8.51, 6.7) * mm, "end": v(8.51, 7.1) * mm});
            skLineSegment(sketch, "E7.3.34.8", {"start": v(8.9, 6.7) * mm, "end": v(8.9, 7.1) * mm});
            skLineSegment(sketch, "E7.6.34.8", {"start": v(8.9, 7.1) * mm, "end": v(8.51, 7.1) * mm});
            skLineSegment(sketch, "E7.9.34.8", {"start": v(8.9, 6.7) * mm, "end": v(8.51, 6.7) * mm});
            skLineSegment(sketch, "E7.0.34.9", {"start": v(8.51, 6.1) * mm, "end": v(8.51, 6.5) * mm});
            skLineSegment(sketch, "E7.3.34.9", {"start": v(8.9, 6.1) * mm, "end": v(8.9, 6.5) * mm});
            skLineSegment(sketch, "E7.6.34.9", {"start": v(8.9, 6.5) * mm, "end": v(8.51, 6.5) * mm});
            skLineSegment(sketch, "E7.9.34.9", {"start": v(8.9, 6.1) * mm, "end": v(8.51, 6.1) * mm});
            skLineSegment(sketch, "E7.0.35.7", {"start": v(9.11, 7.3) * mm, "end": v(9.11, 7.7) * mm});
            skLineSegment(sketch, "E7.3.35.7", {"start": v(9.5, 7.3) * mm, "end": v(9.5, 7.7) * mm});
            skLineSegment(sketch, "E7.6.35.7", {"start": v(9.5, 7.7) * mm, "end": v(9.11, 7.7) * mm});
            skLineSegment(sketch, "E7.9.35.7", {"start": v(9.5, 7.3) * mm, "end": v(9.11, 7.3) * mm});
            skLineSegment(sketch, "E7.0.35.8", {"start": v(9.11, 6.7) * mm, "end": v(9.11, 7.1) * mm});
            skLineSegment(sketch, "E7.3.35.8", {"start": v(9.5, 6.7) * mm, "end": v(9.5, 7.1) * mm});
            skLineSegment(sketch, "E7.6.35.8", {"start": v(9.5, 7.1) * mm, "end": v(9.11, 7.1) * mm});
            skLineSegment(sketch, "E7.9.35.8", {"start": v(9.5, 6.7) * mm, "end": v(9.11, 6.7) * mm});
            skLineSegment(sketch, "E7.0.35.9", {"start": v(9.11, 6.1) * mm, "end": v(9.11, 6.5) * mm});
            skLineSegment(sketch, "E7.3.35.9", {"start": v(9.5, 6.1) * mm, "end": v(9.5, 6.5) * mm});
            skLineSegment(sketch, "E7.6.35.9", {"start": v(9.5, 6.5) * mm, "end": v(9.11, 6.5) * mm});
            skLineSegment(sketch, "E7.9.35.9", {"start": v(9.5, 6.1) * mm, "end": v(9.11, 6.1) * mm});
            skLineSegment(sketch, "E7.0.36.8", {"start": v(9.71, 6.7) * mm, "end": v(9.71, 7.1) * mm});
            skLineSegment(sketch, "E7.3.36.8", {"start": v(10.1, 6.7) * mm, "end": v(10.1, 7.1) * mm});
            skLineSegment(sketch, "E7.6.36.8", {"start": v(10.1, 7.1) * mm, "end": v(9.71, 7.1) * mm});
            skLineSegment(sketch, "E7.9.36.8", {"start": v(10.1, 6.7) * mm, "end": v(9.71, 6.7) * mm});
            skLineSegment(sketch, "E7.0.36.9", {"start": v(9.71, 6.1) * mm, "end": v(9.71, 6.5) * mm});
            skLineSegment(sketch, "E7.3.36.9", {"start": v(10.1, 6.1) * mm, "end": v(10.1, 6.5) * mm});
            skLineSegment(sketch, "E7.6.36.9", {"start": v(10.1, 6.5) * mm, "end": v(9.71, 6.5) * mm});
            skLineSegment(sketch, "E7.9.36.9", {"start": v(10.1, 6.1) * mm, "end": v(9.71, 6.1) * mm});
            skLineSegment(sketch, "E8.0.20.10", {"start": v(0.11, 5.5) * mm, "end": v(0.11, 5.9) * mm});
            skLineSegment(sketch, "E8.3.20.10", {"start": v(0.5, 5.5) * mm, "end": v(0.5, 5.9) * mm});
            skLineSegment(sketch, "E8.6.20.10", {"start": v(0.5, 5.9) * mm, "end": v(0.11, 5.9) * mm});
            skLineSegment(sketch, "E8.9.20.10", {"start": v(0.5, 5.5) * mm, "end": v(0.11, 5.5) * mm});
            skLineSegment(sketch, "E8.0.20.11", {"start": v(0.1, 4.9) * mm, "end": v(0.1, 5.3) * mm});
            skLineSegment(sketch, "E8.3.20.11", {"start": v(0.5, 4.9) * mm, "end": v(0.5, 5.3) * mm});
            skLineSegment(sketch, "E8.6.20.11", {"start": v(0.5, 5.3) * mm, "end": v(0.1, 5.3) * mm});
            skLineSegment(sketch, "E8.9.20.11", {"start": v(0.5, 4.9) * mm, "end": v(0.1, 4.9) * mm});
            skLineSegment(sketch, "E8.0.20.12", {"start": v(0.1, 4.3) * mm, "end": v(0.1, 4.7) * mm});
            skLineSegment(sketch, "E8.3.20.12", {"start": v(0.5, 4.3) * mm, "end": v(0.5, 4.7) * mm});
            skLineSegment(sketch, "E8.6.20.12", {"start": v(0.5, 4.7) * mm, "end": v(0.1, 4.7) * mm});
            skLineSegment(sketch, "E8.9.20.12", {"start": v(0.5, 4.3) * mm, "end": v(0.1, 4.3) * mm});
            skLineSegment(sketch, "E8.0.20.13", {"start": v(0.1, 3.7) * mm, "end": v(0.1, 4.1) * mm});
            skLineSegment(sketch, "E8.3.20.13", {"start": v(0.5, 3.7) * mm, "end": v(0.5, 4.1) * mm});
            skLineSegment(sketch, "E8.6.20.13", {"start": v(0.5, 4.1) * mm, "end": v(0.1, 4.1) * mm});
            skLineSegment(sketch, "E8.9.20.13", {"start": v(0.5, 3.7) * mm, "end": v(0.1, 3.7) * mm});
            skLineSegment(sketch, "E8.0.20.14", {"start": v(0.1, 3.1) * mm, "end": v(0.1, 3.5) * mm});
            skLineSegment(sketch, "E8.3.20.14", {"start": v(0.5, 3.1) * mm, "end": v(0.5, 3.5) * mm});
            skLineSegment(sketch, "E8.6.20.14", {"start": v(0.5, 3.5) * mm, "end": v(0.1, 3.5) * mm});
            skLineSegment(sketch, "E8.9.20.14", {"start": v(0.5, 3.1) * mm, "end": v(0.1, 3.1) * mm});
            skLineSegment(sketch, "E8.0.21.10", {"start": v(0.71, 5.5) * mm, "end": v(0.71, 5.9) * mm});
            skLineSegment(sketch, "E8.3.21.10", {"start": v(1.1, 5.5) * mm, "end": v(1.1, 5.9) * mm});
            skLineSegment(sketch, "E8.6.21.10", {"start": v(1.1, 5.9) * mm, "end": v(0.71, 5.9) * mm});
            skLineSegment(sketch, "E8.9.21.10", {"start": v(1.1, 5.5) * mm, "end": v(0.71, 5.5) * mm});
            skLineSegment(sketch, "E8.0.21.11", {"start": v(0.7, 4.9) * mm, "end": v(0.7, 5.3) * mm});
            skLineSegment(sketch, "E8.3.21.11", {"start": v(1.1, 4.9) * mm, "end": v(1.1, 5.3) * mm});
            skLineSegment(sketch, "E8.6.21.11", {"start": v(1.1, 5.3) * mm, "end": v(0.7, 5.3) * mm});
            skLineSegment(sketch, "E8.9.21.11", {"start": v(1.1, 4.9) * mm, "end": v(0.7, 4.9) * mm});
            skLineSegment(sketch, "E8.0.21.12", {"start": v(0.7, 4.3) * mm, "end": v(0.7, 4.7) * mm});
            skLineSegment(sketch, "E8.3.21.12", {"start": v(1.1, 4.3) * mm, "end": v(1.1, 4.7) * mm});
            skLineSegment(sketch, "E8.6.21.12", {"start": v(1.1, 4.7) * mm, "end": v(0.7, 4.7) * mm});
            skLineSegment(sketch, "E8.9.21.12", {"start": v(1.1, 4.3) * mm, "end": v(0.7, 4.3) * mm});
            skLineSegment(sketch, "E8.0.21.13", {"start": v(0.7, 3.7) * mm, "end": v(0.7, 4.1) * mm});
            skLineSegment(sketch, "E8.3.21.13", {"start": v(1.1, 3.7) * mm, "end": v(1.1, 4.1) * mm});
            skLineSegment(sketch, "E8.6.21.13", {"start": v(1.1, 4.1) * mm, "end": v(0.7, 4.1) * mm});
            skLineSegment(sketch, "E8.9.21.13", {"start": v(1.1, 3.7) * mm, "end": v(0.7, 3.7) * mm});
            skLineSegment(sketch, "E8.0.21.14", {"start": v(0.7, 3.1) * mm, "end": v(0.7, 3.5) * mm});
            skLineSegment(sketch, "E8.3.21.14", {"start": v(1.1, 3.1) * mm, "end": v(1.1, 3.5) * mm});
            skLineSegment(sketch, "E8.6.21.14", {"start": v(1.1, 3.5) * mm, "end": v(0.7, 3.5) * mm});
            skLineSegment(sketch, "E8.9.21.14", {"start": v(1.1, 3.1) * mm, "end": v(0.7, 3.1) * mm});
            skLineSegment(sketch, "E8.0.22.10", {"start": v(1.31, 5.5) * mm, "end": v(1.31, 5.9) * mm});
            skLineSegment(sketch, "E8.3.22.10", {"start": v(1.7, 5.5) * mm, "end": v(1.7, 5.9) * mm});
            skLineSegment(sketch, "E8.6.22.10", {"start": v(1.7, 5.9) * mm, "end": v(1.31, 5.9) * mm});
            skLineSegment(sketch, "E8.9.22.10", {"start": v(1.7, 5.5) * mm, "end": v(1.31, 5.5) * mm});
            skLineSegment(sketch, "E8.0.22.11", {"start": v(1.3, 4.9) * mm, "end": v(1.3, 5.3) * mm});
            skLineSegment(sketch, "E8.3.22.11", {"start": v(1.7, 4.9) * mm, "end": v(1.7, 5.3) * mm});
            skLineSegment(sketch, "E8.6.22.11", {"start": v(1.7, 5.3) * mm, "end": v(1.3, 5.3) * mm});
            skLineSegment(sketch, "E8.9.22.11", {"start": v(1.7, 4.9) * mm, "end": v(1.3, 4.9) * mm});
            skLineSegment(sketch, "E8.0.22.12", {"start": v(1.3, 4.3) * mm, "end": v(1.3, 4.7) * mm});
            skLineSegment(sketch, "E8.3.22.12", {"start": v(1.7, 4.3) * mm, "end": v(1.7, 4.7) * mm});
            skLineSegment(sketch, "E8.6.22.12", {"start": v(1.7, 4.7) * mm, "end": v(1.3, 4.7) * mm});
            skLineSegment(sketch, "E8.9.22.12", {"start": v(1.7, 4.3) * mm, "end": v(1.3, 4.3) * mm});
            skLineSegment(sketch, "E8.0.22.13", {"start": v(1.3, 3.7) * mm, "end": v(1.3, 4.1) * mm});
            skLineSegment(sketch, "E8.3.22.13", {"start": v(1.7, 3.7) * mm, "end": v(1.7, 4.1) * mm});
            skLineSegment(sketch, "E8.6.22.13", {"start": v(1.7, 4.1) * mm, "end": v(1.3, 4.1) * mm});
            skLineSegment(sketch, "E8.9.22.13", {"start": v(1.7, 3.7) * mm, "end": v(1.3, 3.7) * mm});
            skLineSegment(sketch, "E8.0.22.14", {"start": v(1.3, 3.1) * mm, "end": v(1.3, 3.5) * mm});
            skLineSegment(sketch, "E8.3.22.14", {"start": v(1.7, 3.1) * mm, "end": v(1.7, 3.5) * mm});
            skLineSegment(sketch, "E8.6.22.14", {"start": v(1.7, 3.5) * mm, "end": v(1.3, 3.5) * mm});
            skLineSegment(sketch, "E8.9.22.14", {"start": v(1.7, 3.1) * mm, "end": v(1.3, 3.1) * mm});
            skLineSegment(sketch, "E8.0.23.10", {"start": v(1.91, 5.5) * mm, "end": v(1.91, 5.9) * mm});
            skLineSegment(sketch, "E8.3.23.10", {"start": v(2.3, 5.5) * mm, "end": v(2.3, 5.9) * mm});
            skLineSegment(sketch, "E8.6.23.10", {"start": v(2.3, 5.9) * mm, "end": v(1.91, 5.9) * mm});
            skLineSegment(sketch, "E8.9.23.10", {"start": v(2.3, 5.5) * mm, "end": v(1.91, 5.5) * mm});
            skLineSegment(sketch, "E8.0.23.11", {"start": v(1.9, 4.9) * mm, "end": v(1.9, 5.3) * mm});
            skLineSegment(sketch, "E8.3.23.11", {"start": v(2.3, 4.9) * mm, "end": v(2.3, 5.3) * mm});
            skLineSegment(sketch, "E8.6.23.11", {"start": v(2.3, 5.3) * mm, "end": v(1.9, 5.3) * mm});
            skLineSegment(sketch, "E8.9.23.11", {"start": v(2.3, 4.9) * mm, "end": v(1.9, 4.9) * mm});
            skLineSegment(sketch, "E8.0.23.12", {"start": v(1.9, 4.3) * mm, "end": v(1.9, 4.7) * mm});
            skLineSegment(sketch, "E8.3.23.12", {"start": v(2.3, 4.3) * mm, "end": v(2.3, 4.7) * mm});
            skLineSegment(sketch, "E8.6.23.12", {"start": v(2.3, 4.7) * mm, "end": v(1.9, 4.7) * mm});
            skLineSegment(sketch, "E8.9.23.12", {"start": v(2.3, 4.3) * mm, "end": v(1.9, 4.3) * mm});
            skLineSegment(sketch, "E8.0.23.13", {"start": v(1.9, 3.7) * mm, "end": v(1.9, 4.1) * mm});
            skLineSegment(sketch, "E8.3.23.13", {"start": v(2.3, 3.7) * mm, "end": v(2.3, 4.1) * mm});
            skLineSegment(sketch, "E8.6.23.13", {"start": v(2.3, 4.1) * mm, "end": v(1.9, 4.1) * mm});
            skLineSegment(sketch, "E8.9.23.13", {"start": v(2.3, 3.7) * mm, "end": v(1.9, 3.7) * mm});
            skLineSegment(sketch, "E8.0.23.14", {"start": v(1.9, 3.1) * mm, "end": v(1.9, 3.5) * mm});
            skLineSegment(sketch, "E8.3.23.14", {"start": v(2.3, 3.1) * mm, "end": v(2.3, 3.5) * mm});
            skLineSegment(sketch, "E8.6.23.14", {"start": v(2.3, 3.5) * mm, "end": v(1.9, 3.5) * mm});
            skLineSegment(sketch, "E8.9.23.14", {"start": v(2.3, 3.1) * mm, "end": v(1.9, 3.1) * mm});
            skLineSegment(sketch, "E8.0.24.10", {"start": v(2.51, 5.5) * mm, "end": v(2.51, 5.9) * mm});
            skLineSegment(sketch, "E8.3.24.10", {"start": v(2.9, 5.5) * mm, "end": v(2.9, 5.9) * mm});
            skLineSegment(sketch, "E8.6.24.10", {"start": v(2.9, 5.9) * mm, "end": v(2.51, 5.9) * mm});
            skLineSegment(sketch, "E8.9.24.10", {"start": v(2.9, 5.5) * mm, "end": v(2.51, 5.5) * mm});
            skLineSegment(sketch, "E8.0.24.11", {"start": v(2.5, 4.9) * mm, "end": v(2.5, 5.3) * mm});
            skLineSegment(sketch, "E8.3.24.11", {"start": v(2.9, 4.9) * mm, "end": v(2.9, 5.3) * mm});
            skLineSegment(sketch, "E8.6.24.11", {"start": v(2.9, 5.3) * mm, "end": v(2.5, 5.3) * mm});
            skLineSegment(sketch, "E8.9.24.11", {"start": v(2.9, 4.9) * mm, "end": v(2.5, 4.9) * mm});
            skLineSegment(sketch, "E8.0.24.12", {"start": v(2.5, 4.3) * mm, "end": v(2.5, 4.7) * mm});
            skLineSegment(sketch, "E8.3.24.12", {"start": v(2.9, 4.3) * mm, "end": v(2.9, 4.7) * mm});
            skLineSegment(sketch, "E8.6.24.12", {"start": v(2.9, 4.7) * mm, "end": v(2.5, 4.7) * mm});
            skLineSegment(sketch, "E8.9.24.12", {"start": v(2.9, 4.3) * mm, "end": v(2.5, 4.3) * mm});
            skLineSegment(sketch, "E8.0.24.13", {"start": v(2.5, 3.7) * mm, "end": v(2.5, 4.1) * mm});
            skLineSegment(sketch, "E8.3.24.13", {"start": v(2.9, 3.7) * mm, "end": v(2.9, 4.1) * mm});
            skLineSegment(sketch, "E8.6.24.13", {"start": v(2.9, 4.1) * mm, "end": v(2.5, 4.1) * mm});
            skLineSegment(sketch, "E8.9.24.13", {"start": v(2.9, 3.7) * mm, "end": v(2.5, 3.7) * mm});
            skLineSegment(sketch, "E8.0.24.14", {"start": v(2.5, 3.1) * mm, "end": v(2.5, 3.5) * mm});
            skLineSegment(sketch, "E8.3.24.14", {"start": v(2.9, 3.1) * mm, "end": v(2.9, 3.5) * mm});
            skLineSegment(sketch, "E8.6.24.14", {"start": v(2.9, 3.5) * mm, "end": v(2.5, 3.5) * mm});
            skLineSegment(sketch, "E8.9.24.14", {"start": v(2.9, 3.1) * mm, "end": v(2.5, 3.1) * mm});
            skLineSegment(sketch, "E8.0.25.10", {"start": v(3.11, 5.5) * mm, "end": v(3.11, 5.9) * mm});
            skLineSegment(sketch, "E8.3.25.10", {"start": v(3.5, 5.5) * mm, "end": v(3.5, 5.9) * mm});
            skLineSegment(sketch, "E8.6.25.10", {"start": v(3.5, 5.9) * mm, "end": v(3.11, 5.9) * mm});
            skLineSegment(sketch, "E8.9.25.10", {"start": v(3.5, 5.5) * mm, "end": v(3.11, 5.5) * mm});
            skLineSegment(sketch, "E8.0.25.11", {"start": v(3.1, 4.9) * mm, "end": v(3.1, 5.3) * mm});
            skLineSegment(sketch, "E8.3.25.11", {"start": v(3.5, 4.9) * mm, "end": v(3.5, 5.3) * mm});
            skLineSegment(sketch, "E8.6.25.11", {"start": v(3.5, 5.3) * mm, "end": v(3.1, 5.3) * mm});
            skLineSegment(sketch, "E8.9.25.11", {"start": v(3.5, 4.9) * mm, "end": v(3.1, 4.9) * mm});
            skLineSegment(sketch, "E8.0.25.12", {"start": v(3.1, 4.3) * mm, "end": v(3.1, 4.7) * mm});
            skLineSegment(sketch, "E8.3.25.12", {"start": v(3.5, 4.3) * mm, "end": v(3.5, 4.7) * mm});
            skLineSegment(sketch, "E8.6.25.12", {"start": v(3.5, 4.7) * mm, "end": v(3.1, 4.7) * mm});
            skLineSegment(sketch, "E8.9.25.12", {"start": v(3.5, 4.3) * mm, "end": v(3.1, 4.3) * mm});
            skLineSegment(sketch, "E8.0.25.13", {"start": v(3.1, 3.7) * mm, "end": v(3.1, 4.1) * mm});
            skLineSegment(sketch, "E8.3.25.13", {"start": v(3.5, 3.7) * mm, "end": v(3.5, 4.1) * mm});
            skLineSegment(sketch, "E8.6.25.13", {"start": v(3.5, 4.1) * mm, "end": v(3.1, 4.1) * mm});
            skLineSegment(sketch, "E8.9.25.13", {"start": v(3.5, 3.7) * mm, "end": v(3.1, 3.7) * mm});
            skLineSegment(sketch, "E8.0.25.14", {"start": v(3.1, 3.1) * mm, "end": v(3.1, 3.5) * mm});
            skLineSegment(sketch, "E8.3.25.14", {"start": v(3.5, 3.1) * mm, "end": v(3.5, 3.5) * mm});
            skLineSegment(sketch, "E8.6.25.14", {"start": v(3.5, 3.5) * mm, "end": v(3.1, 3.5) * mm});
            skLineSegment(sketch, "E8.9.25.14", {"start": v(3.5, 3.1) * mm, "end": v(3.1, 3.1) * mm});
            skLineSegment(sketch, "E8.0.26.10", {"start": v(3.71, 5.5) * mm, "end": v(3.71, 5.9) * mm});
            skLineSegment(sketch, "E8.3.26.10", {"start": v(4.1, 5.5) * mm, "end": v(4.1, 5.9) * mm});
            skLineSegment(sketch, "E8.6.26.10", {"start": v(4.1, 5.9) * mm, "end": v(3.71, 5.9) * mm});
            skLineSegment(sketch, "E8.9.26.10", {"start": v(4.1, 5.5) * mm, "end": v(3.71, 5.5) * mm});
            skLineSegment(sketch, "E8.0.26.11", {"start": v(3.7, 4.9) * mm, "end": v(3.7, 5.3) * mm});
            skLineSegment(sketch, "E8.3.26.11", {"start": v(4.1, 4.9) * mm, "end": v(4.1, 5.3) * mm});
            skLineSegment(sketch, "E8.6.26.11", {"start": v(4.1, 5.3) * mm, "end": v(3.7, 5.3) * mm});
            skLineSegment(sketch, "E8.9.26.11", {"start": v(4.1, 4.9) * mm, "end": v(3.7, 4.9) * mm});
            skLineSegment(sketch, "E8.0.26.12", {"start": v(3.7, 4.3) * mm, "end": v(3.7, 4.7) * mm});
            skLineSegment(sketch, "E8.3.26.12", {"start": v(4.1, 4.3) * mm, "end": v(4.1, 4.7) * mm});
            skLineSegment(sketch, "E8.6.26.12", {"start": v(4.1, 4.7) * mm, "end": v(3.7, 4.7) * mm});
            skLineSegment(sketch, "E8.9.26.12", {"start": v(4.1, 4.3) * mm, "end": v(3.7, 4.3) * mm});
            skLineSegment(sketch, "E8.0.26.13", {"start": v(3.7, 3.7) * mm, "end": v(3.7, 4.1) * mm});
            skLineSegment(sketch, "E8.3.26.13", {"start": v(4.1, 3.7) * mm, "end": v(4.1, 4.1) * mm});
            skLineSegment(sketch, "E8.6.26.13", {"start": v(4.1, 4.1) * mm, "end": v(3.7, 4.1) * mm});
            skLineSegment(sketch, "E8.9.26.13", {"start": v(4.1, 3.7) * mm, "end": v(3.7, 3.7) * mm});
            skLineSegment(sketch, "E8.0.26.14", {"start": v(3.7, 3.1) * mm, "end": v(3.7, 3.5) * mm});
            skLineSegment(sketch, "E8.3.26.14", {"start": v(4.1, 3.1) * mm, "end": v(4.1, 3.5) * mm});
            skLineSegment(sketch, "E8.6.26.14", {"start": v(4.1, 3.5) * mm, "end": v(3.7, 3.5) * mm});
            skLineSegment(sketch, "E8.9.26.14", {"start": v(4.1, 3.1) * mm, "end": v(3.7, 3.1) * mm});
            skLineSegment(sketch, "E8.0.27.10", {"start": v(4.31, 5.5) * mm, "end": v(4.31, 5.9) * mm});
            skLineSegment(sketch, "E8.3.27.10", {"start": v(4.7, 5.5) * mm, "end": v(4.7, 5.9) * mm});
            skLineSegment(sketch, "E8.6.27.10", {"start": v(4.7, 5.9) * mm, "end": v(4.31, 5.9) * mm});
            skLineSegment(sketch, "E8.9.27.10", {"start": v(4.7, 5.5) * mm, "end": v(4.31, 5.5) * mm});
            skLineSegment(sketch, "E8.0.27.11", {"start": v(4.3, 4.9) * mm, "end": v(4.3, 5.3) * mm});
            skLineSegment(sketch, "E8.3.27.11", {"start": v(4.7, 4.9) * mm, "end": v(4.7, 5.3) * mm});
            skLineSegment(sketch, "E8.6.27.11", {"start": v(4.7, 5.3) * mm, "end": v(4.3, 5.3) * mm});
            skLineSegment(sketch, "E8.9.27.11", {"start": v(4.7, 4.9) * mm, "end": v(4.3, 4.9) * mm});
            skLineSegment(sketch, "E8.0.27.12", {"start": v(4.3, 4.3) * mm, "end": v(4.3, 4.7) * mm});
            skLineSegment(sketch, "E8.3.27.12", {"start": v(4.7, 4.3) * mm, "end": v(4.7, 4.7) * mm});
            skLineSegment(sketch, "E8.6.27.12", {"start": v(4.7, 4.7) * mm, "end": v(4.3, 4.7) * mm});
            skLineSegment(sketch, "E8.9.27.12", {"start": v(4.7, 4.3) * mm, "end": v(4.3, 4.3) * mm});
            skLineSegment(sketch, "E8.0.27.13", {"start": v(4.3, 3.7) * mm, "end": v(4.3, 4.1) * mm});
            skLineSegment(sketch, "E8.3.27.13", {"start": v(4.7, 3.7) * mm, "end": v(4.7, 4.1) * mm});
            skLineSegment(sketch, "E8.6.27.13", {"start": v(4.7, 4.1) * mm, "end": v(4.3, 4.1) * mm});
            skLineSegment(sketch, "E8.9.27.13", {"start": v(4.7, 3.7) * mm, "end": v(4.3, 3.7) * mm});
            skLineSegment(sketch, "E8.0.27.14", {"start": v(4.3, 3.1) * mm, "end": v(4.3, 3.5) * mm});
            skLineSegment(sketch, "E8.3.27.14", {"start": v(4.7, 3.1) * mm, "end": v(4.7, 3.5) * mm});
            skLineSegment(sketch, "E8.6.27.14", {"start": v(4.7, 3.5) * mm, "end": v(4.3, 3.5) * mm});
            skLineSegment(sketch, "E8.9.27.14", {"start": v(4.7, 3.1) * mm, "end": v(4.3, 3.1) * mm});
            skLineSegment(sketch, "E8.0.28.10", {"start": v(4.91, 5.5) * mm, "end": v(4.91, 5.9) * mm});
            skLineSegment(sketch, "E8.3.28.10", {"start": v(5.3, 5.5) * mm, "end": v(5.3, 5.9) * mm});
            skLineSegment(sketch, "E8.6.28.10", {"start": v(5.3, 5.9) * mm, "end": v(4.91, 5.9) * mm});
            skLineSegment(sketch, "E8.9.28.10", {"start": v(5.3, 5.5) * mm, "end": v(4.91, 5.5) * mm});
            skLineSegment(sketch, "E8.0.28.11", {"start": v(4.9, 4.9) * mm, "end": v(4.9, 5.3) * mm});
            skLineSegment(sketch, "E8.3.28.11", {"start": v(5.3, 4.9) * mm, "end": v(5.3, 5.3) * mm});
            skLineSegment(sketch, "E8.6.28.11", {"start": v(5.3, 5.3) * mm, "end": v(4.9, 5.3) * mm});
            skLineSegment(sketch, "E8.9.28.11", {"start": v(5.3, 4.9) * mm, "end": v(4.9, 4.9) * mm});
            skLineSegment(sketch, "E8.0.28.12", {"start": v(4.9, 4.3) * mm, "end": v(4.9, 4.7) * mm});
            skLineSegment(sketch, "E8.3.28.12", {"start": v(5.3, 4.3) * mm, "end": v(5.3, 4.7) * mm});
            skLineSegment(sketch, "E8.6.28.12", {"start": v(5.3, 4.7) * mm, "end": v(4.9, 4.7) * mm});
            skLineSegment(sketch, "E8.9.28.12", {"start": v(5.3, 4.3) * mm, "end": v(4.9, 4.3) * mm});
            skLineSegment(sketch, "E8.0.28.13", {"start": v(4.9, 3.7) * mm, "end": v(4.9, 4.1) * mm});
            skLineSegment(sketch, "E8.3.28.13", {"start": v(5.3, 3.7) * mm, "end": v(5.3, 4.1) * mm});
            skLineSegment(sketch, "E8.6.28.13", {"start": v(5.3, 4.1) * mm, "end": v(4.9, 4.1) * mm});
            skLineSegment(sketch, "E8.9.28.13", {"start": v(5.3, 3.7) * mm, "end": v(4.9, 3.7) * mm});
            skLineSegment(sketch, "E8.0.28.14", {"start": v(4.9, 3.1) * mm, "end": v(4.9, 3.5) * mm});
            skLineSegment(sketch, "E8.3.28.14", {"start": v(5.3, 3.1) * mm, "end": v(5.3, 3.5) * mm});
            skLineSegment(sketch, "E8.6.28.14", {"start": v(5.3, 3.5) * mm, "end": v(4.9, 3.5) * mm});
            skLineSegment(sketch, "E8.9.28.14", {"start": v(5.3, 3.1) * mm, "end": v(4.9, 3.1) * mm});
            skLineSegment(sketch, "E8.0.29.10", {"start": v(5.51, 5.5) * mm, "end": v(5.51, 5.9) * mm});
            skLineSegment(sketch, "E8.3.29.10", {"start": v(5.9, 5.5) * mm, "end": v(5.9, 5.9) * mm});
            skLineSegment(sketch, "E8.6.29.10", {"start": v(5.9, 5.9) * mm, "end": v(5.51, 5.9) * mm});
            skLineSegment(sketch, "E8.9.29.10", {"start": v(5.9, 5.5) * mm, "end": v(5.51, 5.5) * mm});
            skLineSegment(sketch, "E8.0.29.11", {"start": v(5.5, 4.9) * mm, "end": v(5.5, 5.3) * mm});
            skLineSegment(sketch, "E8.3.29.11", {"start": v(5.9, 4.9) * mm, "end": v(5.9, 5.3) * mm});
            skLineSegment(sketch, "E8.6.29.11", {"start": v(5.9, 5.3) * mm, "end": v(5.5, 5.3) * mm});
            skLineSegment(sketch, "E8.9.29.11", {"start": v(5.9, 4.9) * mm, "end": v(5.5, 4.9) * mm});
            skLineSegment(sketch, "E8.0.29.12", {"start": v(5.5, 4.3) * mm, "end": v(5.5, 4.7) * mm});
            skLineSegment(sketch, "E8.3.29.12", {"start": v(5.9, 4.3) * mm, "end": v(5.9, 4.7) * mm});
            skLineSegment(sketch, "E8.6.29.12", {"start": v(5.9, 4.7) * mm, "end": v(5.5, 4.7) * mm});
            skLineSegment(sketch, "E8.9.29.12", {"start": v(5.9, 4.3) * mm, "end": v(5.5, 4.3) * mm});
            skLineSegment(sketch, "E8.0.29.13", {"start": v(5.5, 3.7) * mm, "end": v(5.5, 4.1) * mm});
            skLineSegment(sketch, "E8.3.29.13", {"start": v(5.9, 3.7) * mm, "end": v(5.9, 4.1) * mm});
            skLineSegment(sketch, "E8.6.29.13", {"start": v(5.9, 4.1) * mm, "end": v(5.5, 4.1) * mm});
            skLineSegment(sketch, "E8.9.29.13", {"start": v(5.9, 3.7) * mm, "end": v(5.5, 3.7) * mm});
            skLineSegment(sketch, "E8.0.29.14", {"start": v(5.5, 3.1) * mm, "end": v(5.5, 3.5) * mm});
            skLineSegment(sketch, "E8.3.29.14", {"start": v(5.9, 3.1) * mm, "end": v(5.9, 3.5) * mm});
            skLineSegment(sketch, "E8.6.29.14", {"start": v(5.9, 3.5) * mm, "end": v(5.5, 3.5) * mm});
            skLineSegment(sketch, "E8.9.29.14", {"start": v(5.9, 3.1) * mm, "end": v(5.5, 3.1) * mm});
            skLineSegment(sketch, "E8.0.30.10", {"start": v(6.11, 5.5) * mm, "end": v(6.11, 5.9) * mm});
            skLineSegment(sketch, "E8.3.30.10", {"start": v(6.5, 5.5) * mm, "end": v(6.5, 5.9) * mm});
            skLineSegment(sketch, "E8.6.30.10", {"start": v(6.5, 5.9) * mm, "end": v(6.11, 5.9) * mm});
            skLineSegment(sketch, "E8.9.30.10", {"start": v(6.5, 5.5) * mm, "end": v(6.11, 5.5) * mm});
            skLineSegment(sketch, "E8.0.30.11", {"start": v(6.1, 4.9) * mm, "end": v(6.1, 5.3) * mm});
            skLineSegment(sketch, "E8.3.30.11", {"start": v(6.5, 4.9) * mm, "end": v(6.5, 5.3) * mm});
            skLineSegment(sketch, "E8.6.30.11", {"start": v(6.5, 5.3) * mm, "end": v(6.1, 5.3) * mm});
            skLineSegment(sketch, "E8.9.30.11", {"start": v(6.5, 4.9) * mm, "end": v(6.1, 4.9) * mm});
            skLineSegment(sketch, "E8.0.30.12", {"start": v(6.1, 4.3) * mm, "end": v(6.1, 4.7) * mm});
            skLineSegment(sketch, "E8.3.30.12", {"start": v(6.5, 4.3) * mm, "end": v(6.5, 4.7) * mm});
            skLineSegment(sketch, "E8.6.30.12", {"start": v(6.5, 4.7) * mm, "end": v(6.1, 4.7) * mm});
            skLineSegment(sketch, "E8.9.30.12", {"start": v(6.5, 4.3) * mm, "end": v(6.1, 4.3) * mm});
            skLineSegment(sketch, "E8.0.30.13", {"start": v(6.1, 3.7) * mm, "end": v(6.1, 4.1) * mm});
            skLineSegment(sketch, "E8.3.30.13", {"start": v(6.5, 3.7) * mm, "end": v(6.5, 4.1) * mm});
            skLineSegment(sketch, "E8.6.30.13", {"start": v(6.5, 4.1) * mm, "end": v(6.1, 4.1) * mm});
            skLineSegment(sketch, "E8.9.30.13", {"start": v(6.5, 3.7) * mm, "end": v(6.1, 3.7) * mm});
            skLineSegment(sketch, "E8.0.30.14", {"start": v(6.1, 3.1) * mm, "end": v(6.1, 3.5) * mm});
            skLineSegment(sketch, "E8.3.30.14", {"start": v(6.5, 3.1) * mm, "end": v(6.5, 3.5) * mm});
            skLineSegment(sketch, "E8.6.30.14", {"start": v(6.5, 3.5) * mm, "end": v(6.1, 3.5) * mm});
            skLineSegment(sketch, "E8.9.30.14", {"start": v(6.5, 3.1) * mm, "end": v(6.1, 3.1) * mm});
            skLineSegment(sketch, "E8.0.31.10", {"start": v(6.71, 5.5) * mm, "end": v(6.71, 5.9) * mm});
            skLineSegment(sketch, "E8.3.31.10", {"start": v(7.1, 5.5) * mm, "end": v(7.1, 5.9) * mm});
            skLineSegment(sketch, "E8.6.31.10", {"start": v(7.1, 5.9) * mm, "end": v(6.71, 5.9) * mm});
            skLineSegment(sketch, "E8.9.31.10", {"start": v(7.1, 5.5) * mm, "end": v(6.71, 5.5) * mm});
            skLineSegment(sketch, "E8.0.31.11", {"start": v(6.7, 4.9) * mm, "end": v(6.7, 5.3) * mm});
            skLineSegment(sketch, "E8.3.31.11", {"start": v(7.1, 4.9) * mm, "end": v(7.1, 5.3) * mm});
            skLineSegment(sketch, "E8.6.31.11", {"start": v(7.1, 5.3) * mm, "end": v(6.7, 5.3) * mm});
            skLineSegment(sketch, "E8.9.31.11", {"start": v(7.1, 4.9) * mm, "end": v(6.7, 4.9) * mm});
            skLineSegment(sketch, "E8.0.31.12", {"start": v(6.7, 4.3) * mm, "end": v(6.7, 4.7) * mm});
            skLineSegment(sketch, "E8.3.31.12", {"start": v(7.1, 4.3) * mm, "end": v(7.1, 4.7) * mm});
            skLineSegment(sketch, "E8.6.31.12", {"start": v(7.1, 4.7) * mm, "end": v(6.7, 4.7) * mm});
            skLineSegment(sketch, "E8.9.31.12", {"start": v(7.1, 4.3) * mm, "end": v(6.7, 4.3) * mm});
            skLineSegment(sketch, "E8.0.31.13", {"start": v(6.7, 3.7) * mm, "end": v(6.7, 4.1) * mm});
            skLineSegment(sketch, "E8.3.31.13", {"start": v(7.1, 3.7) * mm, "end": v(7.1, 4.1) * mm});
            skLineSegment(sketch, "E8.6.31.13", {"start": v(7.1, 4.1) * mm, "end": v(6.7, 4.1) * mm});
            skLineSegment(sketch, "E8.9.31.13", {"start": v(7.1, 3.7) * mm, "end": v(6.7, 3.7) * mm});
            skLineSegment(sketch, "E8.0.31.14", {"start": v(6.7, 3.1) * mm, "end": v(6.7, 3.5) * mm});
            skLineSegment(sketch, "E8.3.31.14", {"start": v(7.1, 3.1) * mm, "end": v(7.1, 3.5) * mm});
            skLineSegment(sketch, "E8.6.31.14", {"start": v(7.1, 3.5) * mm, "end": v(6.7, 3.5) * mm});
            skLineSegment(sketch, "E8.9.31.14", {"start": v(7.1, 3.1) * mm, "end": v(6.7, 3.1) * mm});
            skLineSegment(sketch, "E8.0.32.10", {"start": v(7.31, 5.5) * mm, "end": v(7.31, 5.9) * mm});
            skLineSegment(sketch, "E8.3.32.10", {"start": v(7.7, 5.5) * mm, "end": v(7.7, 5.9) * mm});
            skLineSegment(sketch, "E8.6.32.10", {"start": v(7.7, 5.9) * mm, "end": v(7.31, 5.9) * mm});
            skLineSegment(sketch, "E8.9.32.10", {"start": v(7.7, 5.5) * mm, "end": v(7.31, 5.5) * mm});
            skLineSegment(sketch, "E8.0.32.11", {"start": v(7.3, 4.9) * mm, "end": v(7.3, 5.3) * mm});
            skLineSegment(sketch, "E8.3.32.11", {"start": v(7.7, 4.9) * mm, "end": v(7.7, 5.3) * mm});
            skLineSegment(sketch, "E8.6.32.11", {"start": v(7.7, 5.3) * mm, "end": v(7.3, 5.3) * mm});
            skLineSegment(sketch, "E8.9.32.11", {"start": v(7.7, 4.9) * mm, "end": v(7.3, 4.9) * mm});
            skLineSegment(sketch, "E8.0.32.12", {"start": v(7.3, 4.3) * mm, "end": v(7.3, 4.7) * mm});
            skLineSegment(sketch, "E8.3.32.12", {"start": v(7.7, 4.3) * mm, "end": v(7.7, 4.7) * mm});
            skLineSegment(sketch, "E8.6.32.12", {"start": v(7.7, 4.7) * mm, "end": v(7.3, 4.7) * mm});
            skLineSegment(sketch, "E8.9.32.12", {"start": v(7.7, 4.3) * mm, "end": v(7.3, 4.3) * mm});
            skLineSegment(sketch, "E8.0.32.13", {"start": v(7.3, 3.7) * mm, "end": v(7.3, 4.1) * mm});
            skLineSegment(sketch, "E8.3.32.13", {"start": v(7.7, 3.7) * mm, "end": v(7.7, 4.1) * mm});
            skLineSegment(sketch, "E8.6.32.13", {"start": v(7.7, 4.1) * mm, "end": v(7.3, 4.1) * mm});
            skLineSegment(sketch, "E8.9.32.13", {"start": v(7.7, 3.7) * mm, "end": v(7.3, 3.7) * mm});
            skLineSegment(sketch, "E8.0.32.14", {"start": v(7.3, 3.1) * mm, "end": v(7.3, 3.5) * mm});
            skLineSegment(sketch, "E8.3.32.14", {"start": v(7.7, 3.1) * mm, "end": v(7.7, 3.5) * mm});
            skLineSegment(sketch, "E8.6.32.14", {"start": v(7.7, 3.5) * mm, "end": v(7.3, 3.5) * mm});
            skLineSegment(sketch, "E8.9.32.14", {"start": v(7.7, 3.1) * mm, "end": v(7.3, 3.1) * mm});
            skLineSegment(sketch, "E8.0.33.10", {"start": v(7.91, 5.5) * mm, "end": v(7.91, 5.9) * mm});
            skLineSegment(sketch, "E8.3.33.10", {"start": v(8.3, 5.5) * mm, "end": v(8.3, 5.9) * mm});
            skLineSegment(sketch, "E8.6.33.10", {"start": v(8.3, 5.9) * mm, "end": v(7.91, 5.9) * mm});
            skLineSegment(sketch, "E8.9.33.10", {"start": v(8.3, 5.5) * mm, "end": v(7.91, 5.5) * mm});
            skLineSegment(sketch, "E8.0.33.11", {"start": v(7.9, 4.9) * mm, "end": v(7.9, 5.3) * mm});
            skLineSegment(sketch, "E8.3.33.11", {"start": v(8.3, 4.9) * mm, "end": v(8.3, 5.3) * mm});
            skLineSegment(sketch, "E8.6.33.11", {"start": v(8.3, 5.3) * mm, "end": v(7.9, 5.3) * mm});
            skLineSegment(sketch, "E8.9.33.11", {"start": v(8.3, 4.9) * mm, "end": v(7.9, 4.9) * mm});
            skLineSegment(sketch, "E8.0.33.12", {"start": v(7.9, 4.3) * mm, "end": v(7.9, 4.7) * mm});
            skLineSegment(sketch, "E8.3.33.12", {"start": v(8.3, 4.3) * mm, "end": v(8.3, 4.7) * mm});
            skLineSegment(sketch, "E8.6.33.12", {"start": v(8.3, 4.7) * mm, "end": v(7.9, 4.7) * mm});
            skLineSegment(sketch, "E8.9.33.12", {"start": v(8.3, 4.3) * mm, "end": v(7.9, 4.3) * mm});
            skLineSegment(sketch, "E8.0.33.13", {"start": v(7.9, 3.7) * mm, "end": v(7.9, 4.1) * mm});
            skLineSegment(sketch, "E8.3.33.13", {"start": v(8.3, 3.7) * mm, "end": v(8.3, 4.1) * mm});
            skLineSegment(sketch, "E8.6.33.13", {"start": v(8.3, 4.1) * mm, "end": v(7.9, 4.1) * mm});
            skLineSegment(sketch, "E8.9.33.13", {"start": v(8.3, 3.7) * mm, "end": v(7.9, 3.7) * mm});
            skLineSegment(sketch, "E8.0.33.14", {"start": v(7.9, 3.1) * mm, "end": v(7.9, 3.5) * mm});
            skLineSegment(sketch, "E8.3.33.14", {"start": v(8.3, 3.1) * mm, "end": v(8.3, 3.5) * mm});
            skLineSegment(sketch, "E8.6.33.14", {"start": v(8.3, 3.5) * mm, "end": v(7.9, 3.5) * mm});
            skLineSegment(sketch, "E8.9.33.14", {"start": v(8.3, 3.1) * mm, "end": v(7.9, 3.1) * mm});
            skLineSegment(sketch, "E8.0.34.10", {"start": v(8.51, 5.5) * mm, "end": v(8.51, 5.9) * mm});
            skLineSegment(sketch, "E8.3.34.10", {"start": v(8.9, 5.5) * mm, "end": v(8.9, 5.9) * mm});
            skLineSegment(sketch, "E8.6.34.10", {"start": v(8.9, 5.9) * mm, "end": v(8.51, 5.9) * mm});
            skLineSegment(sketch, "E8.9.34.10", {"start": v(8.9, 5.5) * mm, "end": v(8.51, 5.5) * mm});
            skLineSegment(sketch, "E8.0.34.11", {"start": v(8.5, 4.9) * mm, "end": v(8.5, 5.3) * mm});
            skLineSegment(sketch, "E8.3.34.11", {"start": v(8.9, 4.9) * mm, "end": v(8.9, 5.3) * mm});
            skLineSegment(sketch, "E8.6.34.11", {"start": v(8.9, 5.3) * mm, "end": v(8.5, 5.3) * mm});
            skLineSegment(sketch, "E8.9.34.11", {"start": v(8.9, 4.9) * mm, "end": v(8.5, 4.9) * mm});
            skLineSegment(sketch, "E8.0.34.12", {"start": v(8.5, 4.3) * mm, "end": v(8.5, 4.7) * mm});
            skLineSegment(sketch, "E8.3.34.12", {"start": v(8.9, 4.3) * mm, "end": v(8.9, 4.7) * mm});
            skLineSegment(sketch, "E8.6.34.12", {"start": v(8.9, 4.7) * mm, "end": v(8.5, 4.7) * mm});
            skLineSegment(sketch, "E8.9.34.12", {"start": v(8.9, 4.3) * mm, "end": v(8.5, 4.3) * mm});
            skLineSegment(sketch, "E8.0.34.13", {"start": v(8.5, 3.7) * mm, "end": v(8.5, 4.1) * mm});
            skLineSegment(sketch, "E8.3.34.13", {"start": v(8.9, 3.7) * mm, "end": v(8.9, 4.1) * mm});
            skLineSegment(sketch, "E8.6.34.13", {"start": v(8.9, 4.1) * mm, "end": v(8.5, 4.1) * mm});
            skLineSegment(sketch, "E8.9.34.13", {"start": v(8.9, 3.7) * mm, "end": v(8.5, 3.7) * mm});
            skLineSegment(sketch, "E8.0.34.14", {"start": v(8.5, 3.1) * mm, "end": v(8.5, 3.5) * mm});
            skLineSegment(sketch, "E8.3.34.14", {"start": v(8.9, 3.1) * mm, "end": v(8.9, 3.5) * mm});
            skLineSegment(sketch, "E8.6.34.14", {"start": v(8.9, 3.5) * mm, "end": v(8.5, 3.5) * mm});
            skLineSegment(sketch, "E8.9.34.14", {"start": v(8.9, 3.1) * mm, "end": v(8.5, 3.1) * mm});
            skLineSegment(sketch, "E8.0.35.10", {"start": v(9.11, 5.5) * mm, "end": v(9.11, 5.9) * mm});
            skLineSegment(sketch, "E8.3.35.10", {"start": v(9.5, 5.5) * mm, "end": v(9.5, 5.9) * mm});
            skLineSegment(sketch, "E8.6.35.10", {"start": v(9.5, 5.9) * mm, "end": v(9.11, 5.9) * mm});
            skLineSegment(sketch, "E8.9.35.10", {"start": v(9.5, 5.5) * mm, "end": v(9.11, 5.5) * mm});
            skLineSegment(sketch, "E8.0.35.11", {"start": v(9.1, 4.9) * mm, "end": v(9.1, 5.3) * mm});
            skLineSegment(sketch, "E8.3.35.11", {"start": v(9.5, 4.9) * mm, "end": v(9.5, 5.3) * mm});
            skLineSegment(sketch, "E8.6.35.11", {"start": v(9.5, 5.3) * mm, "end": v(9.1, 5.3) * mm});
            skLineSegment(sketch, "E8.9.35.11", {"start": v(9.5, 4.9) * mm, "end": v(9.1, 4.9) * mm});
            skLineSegment(sketch, "E8.0.35.12", {"start": v(9.1, 4.3) * mm, "end": v(9.1, 4.7) * mm});
            skLineSegment(sketch, "E8.3.35.12", {"start": v(9.5, 4.3) * mm, "end": v(9.5, 4.7) * mm});
            skLineSegment(sketch, "E8.6.35.12", {"start": v(9.5, 4.7) * mm, "end": v(9.1, 4.7) * mm});
            skLineSegment(sketch, "E8.9.35.12", {"start": v(9.5, 4.3) * mm, "end": v(9.1, 4.3) * mm});
            skLineSegment(sketch, "E8.0.35.13", {"start": v(9.1, 3.7) * mm, "end": v(9.1, 4.1) * mm});
            skLineSegment(sketch, "E8.3.35.13", {"start": v(9.5, 3.7) * mm, "end": v(9.5, 4.1) * mm});
            skLineSegment(sketch, "E8.6.35.13", {"start": v(9.5, 4.1) * mm, "end": v(9.1, 4.1) * mm});
            skLineSegment(sketch, "E8.9.35.13", {"start": v(9.5, 3.7) * mm, "end": v(9.1, 3.7) * mm});
            skLineSegment(sketch, "E8.0.35.14", {"start": v(9.1, 3.1) * mm, "end": v(9.1, 3.5) * mm});
            skLineSegment(sketch, "E8.3.35.14", {"start": v(9.5, 3.1) * mm, "end": v(9.5, 3.5) * mm});
            skLineSegment(sketch, "E8.6.35.14", {"start": v(9.5, 3.5) * mm, "end": v(9.1, 3.5) * mm});
            skLineSegment(sketch, "E8.9.35.14", {"start": v(9.5, 3.1) * mm, "end": v(9.1, 3.1) * mm});
            skLineSegment(sketch, "E8.0.36.10", {"start": v(9.71, 5.5) * mm, "end": v(9.71, 5.9) * mm});
            skLineSegment(sketch, "E8.3.36.10", {"start": v(10.1, 5.5) * mm, "end": v(10.1, 5.9) * mm});
            skLineSegment(sketch, "E8.6.36.10", {"start": v(10.1, 5.9) * mm, "end": v(9.71, 5.9) * mm});
            skLineSegment(sketch, "E8.9.36.10", {"start": v(10.1, 5.5) * mm, "end": v(9.71, 5.5) * mm});
            skLineSegment(sketch, "E8.0.36.11", {"start": v(9.7, 4.9) * mm, "end": v(9.7, 5.3) * mm});
            skLineSegment(sketch, "E8.3.36.11", {"start": v(10.1, 4.9) * mm, "end": v(10.1, 5.3) * mm});
            skLineSegment(sketch, "E8.6.36.11", {"start": v(10.1, 5.3) * mm, "end": v(9.7, 5.3) * mm});
            skLineSegment(sketch, "E8.9.36.11", {"start": v(10.1, 4.9) * mm, "end": v(9.7, 4.9) * mm});
            skLineSegment(sketch, "E8.0.36.12", {"start": v(9.7, 4.3) * mm, "end": v(9.7, 4.7) * mm});
            skLineSegment(sketch, "E8.3.36.12", {"start": v(10.1, 4.3) * mm, "end": v(10.1, 4.7) * mm});
            skLineSegment(sketch, "E8.6.36.12", {"start": v(10.1, 4.7) * mm, "end": v(9.7, 4.7) * mm});
            skLineSegment(sketch, "E8.9.36.12", {"start": v(10.1, 4.3) * mm, "end": v(9.7, 4.3) * mm});
            skLineSegment(sketch, "E8.0.36.13", {"start": v(9.7, 3.7) * mm, "end": v(9.7, 4.1) * mm});
            skLineSegment(sketch, "E8.3.36.13", {"start": v(10.1, 3.7) * mm, "end": v(10.1, 4.1) * mm});
            skLineSegment(sketch, "E8.6.36.13", {"start": v(10.1, 4.1) * mm, "end": v(9.7, 4.1) * mm});
            skLineSegment(sketch, "E8.9.36.13", {"start": v(10.1, 3.7) * mm, "end": v(9.7, 3.7) * mm});
            skLineSegment(sketch, "E8.0.36.14", {"start": v(9.7, 3.1) * mm, "end": v(9.7, 3.5) * mm});
            skLineSegment(sketch, "E8.3.36.14", {"start": v(10.1, 3.1) * mm, "end": v(10.1, 3.5) * mm});
            skLineSegment(sketch, "E8.6.36.14", {"start": v(10.1, 3.5) * mm, "end": v(9.7, 3.5) * mm});
            skLineSegment(sketch, "E8.9.36.14", {"start": v(10.1, 3.1) * mm, "end": v(9.7, 3.1) * mm});
            skLineSegment(sketch, "E8.0.37.10", {"start": v(10.31, 5.5) * mm, "end": v(10.31, 5.9) * mm});
            skLineSegment(sketch, "E8.3.37.10", {"start": v(10.7, 5.5) * mm, "end": v(10.7, 5.9) * mm});
            skLineSegment(sketch, "E8.6.37.10", {"start": v(10.7, 5.9) * mm, "end": v(10.31, 5.9) * mm});
            skLineSegment(sketch, "E8.9.37.10", {"start": v(10.7, 5.5) * mm, "end": v(10.31, 5.5) * mm});
            skLineSegment(sketch, "E8.0.37.11", {"start": v(10.3, 4.9) * mm, "end": v(10.3, 5.3) * mm});
            skLineSegment(sketch, "E8.3.37.11", {"start": v(10.7, 4.9) * mm, "end": v(10.7, 5.3) * mm});
            skLineSegment(sketch, "E8.6.37.11", {"start": v(10.7, 5.3) * mm, "end": v(10.3, 5.3) * mm});
            skLineSegment(sketch, "E8.9.37.11", {"start": v(10.7, 4.9) * mm, "end": v(10.3, 4.9) * mm});
            skLineSegment(sketch, "E8.0.37.12", {"start": v(10.3, 4.3) * mm, "end": v(10.3, 4.7) * mm});
            skLineSegment(sketch, "E8.3.37.12", {"start": v(10.7, 4.3) * mm, "end": v(10.7, 4.7) * mm});
            skLineSegment(sketch, "E8.6.37.12", {"start": v(10.7, 4.7) * mm, "end": v(10.3, 4.7) * mm});
            skLineSegment(sketch, "E8.9.37.12", {"start": v(10.7, 4.3) * mm, "end": v(10.3, 4.3) * mm});
            skLineSegment(sketch, "E8.0.37.13", {"start": v(10.3, 3.7) * mm, "end": v(10.3, 4.1) * mm});
            skLineSegment(sketch, "E8.3.37.13", {"start": v(10.7, 3.7) * mm, "end": v(10.7, 4.1) * mm});
            skLineSegment(sketch, "E8.6.37.13", {"start": v(10.7, 4.1) * mm, "end": v(10.3, 4.1) * mm});
            skLineSegment(sketch, "E8.9.37.13", {"start": v(10.7, 3.7) * mm, "end": v(10.3, 3.7) * mm});
            skLineSegment(sketch, "E8.0.37.14", {"start": v(10.3, 3.1) * mm, "end": v(10.3, 3.5) * mm});
            skLineSegment(sketch, "E8.3.37.14", {"start": v(10.7, 3.1) * mm, "end": v(10.7, 3.5) * mm});
            skLineSegment(sketch, "E8.6.37.14", {"start": v(10.7, 3.5) * mm, "end": v(10.3, 3.5) * mm});
            skLineSegment(sketch, "E8.9.37.14", {"start": v(10.7, 3.1) * mm, "end": v(10.3, 3.1) * mm});
            skLineSegment(sketch, "E8.0.38.12", {"start": v(10.9, 4.3) * mm, "end": v(10.9, 4.7) * mm});
            skLineSegment(sketch, "E8.3.38.12", {"start": v(11.3, 4.3) * mm, "end": v(11.3, 4.7) * mm});
            skLineSegment(sketch, "E8.6.38.12", {"start": v(11.3, 4.7) * mm, "end": v(10.9, 4.7) * mm});
            skLineSegment(sketch, "E8.9.38.12", {"start": v(11.3, 4.3) * mm, "end": v(10.9, 4.3) * mm});
            skLineSegment(sketch, "E8.0.38.13", {"start": v(10.9, 3.7) * mm, "end": v(10.9, 4.1) * mm});
            skLineSegment(sketch, "E8.3.38.13", {"start": v(11.3, 3.7) * mm, "end": v(11.3, 4.1) * mm});
            skLineSegment(sketch, "E8.6.38.13", {"start": v(11.3, 4.1) * mm, "end": v(10.9, 4.1) * mm});
            skLineSegment(sketch, "E8.9.38.13", {"start": v(11.3, 3.7) * mm, "end": v(10.9, 3.7) * mm});
            skLineSegment(sketch, "E8.0.38.14", {"start": v(10.9, 3.1) * mm, "end": v(10.9, 3.5) * mm});
            skLineSegment(sketch, "E8.3.38.14", {"start": v(11.3, 3.1) * mm, "end": v(11.3, 3.5) * mm});
            skLineSegment(sketch, "E8.6.38.14", {"start": v(11.3, 3.5) * mm, "end": v(10.9, 3.5) * mm});
            skLineSegment(sketch, "E8.9.38.14", {"start": v(11.3, 3.1) * mm, "end": v(10.9, 3.1) * mm});
            skLineSegment(sketch, "E8.0.39.14", {"start": v(11.5, 3.1) * mm, "end": v(11.5, 3.5) * mm});
            skLineSegment(sketch, "E9.0.20.15", {"start": v(0.1, 2.5) * mm, "end": v(0.1, 2.9) * mm});
            skLineSegment(sketch, "E9.3.20.15", {"start": v(0.5, 2.5) * mm, "end": v(0.5, 2.9) * mm});
            skLineSegment(sketch, "E9.6.20.15", {"start": v(0.5, 2.9) * mm, "end": v(0.1, 2.9) * mm});
            skLineSegment(sketch, "E9.9.20.15", {"start": v(0.5, 2.5) * mm, "end": v(0.1, 2.5) * mm});
            skLineSegment(sketch, "E9.0.20.16", {"start": v(0.1, 1.9) * mm, "end": v(0.1, 2.3) * mm});
            skLineSegment(sketch, "E9.3.20.16", {"start": v(0.5, 1.9) * mm, "end": v(0.5, 2.3) * mm});
            skLineSegment(sketch, "E9.6.20.16", {"start": v(0.5, 2.3) * mm, "end": v(0.1, 2.3) * mm});
            skLineSegment(sketch, "E9.9.20.16", {"start": v(0.5, 1.9) * mm, "end": v(0.1, 1.9) * mm});
            skLineSegment(sketch, "E9.0.20.17", {"start": v(0.1, 1.3) * mm, "end": v(0.1, 1.7) * mm});
            skLineSegment(sketch, "E9.3.20.17", {"start": v(0.5, 1.3) * mm, "end": v(0.5, 1.7) * mm});
            skLineSegment(sketch, "E9.6.20.17", {"start": v(0.5, 1.7) * mm, "end": v(0.1, 1.7) * mm});
            skLineSegment(sketch, "E9.9.20.17", {"start": v(0.5, 1.3) * mm, "end": v(0.1, 1.3) * mm});
            skLineSegment(sketch, "E9.0.21.15", {"start": v(0.7, 2.5) * mm, "end": v(0.7, 2.9) * mm});
            skLineSegment(sketch, "E9.3.21.15", {"start": v(1.1, 2.5) * mm, "end": v(1.1, 2.9) * mm});
            skLineSegment(sketch, "E9.6.21.15", {"start": v(1.1, 2.9) * mm, "end": v(0.7, 2.9) * mm});
            skLineSegment(sketch, "E9.9.21.15", {"start": v(1.1, 2.5) * mm, "end": v(0.7, 2.5) * mm});
            skLineSegment(sketch, "E9.0.21.16", {"start": v(0.7, 1.9) * mm, "end": v(0.7, 2.3) * mm});
            skLineSegment(sketch, "E9.3.21.16", {"start": v(1.1, 1.9) * mm, "end": v(1.1, 2.3) * mm});
            skLineSegment(sketch, "E9.6.21.16", {"start": v(1.1, 2.3) * mm, "end": v(0.7, 2.3) * mm});
            skLineSegment(sketch, "E9.9.21.16", {"start": v(1.1, 1.9) * mm, "end": v(0.7, 1.9) * mm});
            skLineSegment(sketch, "E9.0.21.17", {"start": v(0.7, 1.3) * mm, "end": v(0.7, 1.7) * mm});
            skLineSegment(sketch, "E9.3.21.17", {"start": v(1.1, 1.3) * mm, "end": v(1.1, 1.7) * mm});
            skLineSegment(sketch, "E9.6.21.17", {"start": v(1.1, 1.7) * mm, "end": v(0.7, 1.7) * mm});
            skLineSegment(sketch, "E9.9.21.17", {"start": v(1.1, 1.3) * mm, "end": v(0.7, 1.3) * mm});
            skLineSegment(sketch, "E9.0.22.15", {"start": v(1.3, 2.5) * mm, "end": v(1.3, 2.9) * mm});
            skLineSegment(sketch, "E9.3.22.15", {"start": v(1.7, 2.5) * mm, "end": v(1.7, 2.9) * mm});
            skLineSegment(sketch, "E9.6.22.15", {"start": v(1.7, 2.9) * mm, "end": v(1.3, 2.9) * mm});
            skLineSegment(sketch, "E9.9.22.15", {"start": v(1.7, 2.5) * mm, "end": v(1.3, 2.5) * mm});
            skLineSegment(sketch, "E9.0.22.16", {"start": v(1.3, 1.9) * mm, "end": v(1.3, 2.3) * mm});
            skLineSegment(sketch, "E9.3.22.16", {"start": v(1.7, 1.9) * mm, "end": v(1.7, 2.3) * mm});
            skLineSegment(sketch, "E9.6.22.16", {"start": v(1.7, 2.3) * mm, "end": v(1.3, 2.3) * mm});
            skLineSegment(sketch, "E9.9.22.16", {"start": v(1.7, 1.9) * mm, "end": v(1.3, 1.9) * mm});
            skLineSegment(sketch, "E9.0.22.17", {"start": v(1.3, 1.3) * mm, "end": v(1.3, 1.7) * mm});
            skLineSegment(sketch, "E9.3.22.17", {"start": v(1.7, 1.3) * mm, "end": v(1.7, 1.7) * mm});
            skLineSegment(sketch, "E9.6.22.17", {"start": v(1.7, 1.7) * mm, "end": v(1.3, 1.7) * mm});
            skLineSegment(sketch, "E9.9.22.17", {"start": v(1.7, 1.3) * mm, "end": v(1.3, 1.3) * mm});
            skLineSegment(sketch, "E9.0.23.15", {"start": v(1.9, 2.5) * mm, "end": v(1.9, 2.9) * mm});
            skLineSegment(sketch, "E9.3.23.15", {"start": v(2.3, 2.5) * mm, "end": v(2.3, 2.9) * mm});
            skLineSegment(sketch, "E9.6.23.15", {"start": v(2.3, 2.9) * mm, "end": v(1.9, 2.9) * mm});
            skLineSegment(sketch, "E9.9.23.15", {"start": v(2.3, 2.5) * mm, "end": v(1.9, 2.5) * mm});
            skLineSegment(sketch, "E9.0.23.16", {"start": v(1.9, 1.9) * mm, "end": v(1.9, 2.3) * mm});
            skLineSegment(sketch, "E9.3.23.16", {"start": v(2.3, 1.9) * mm, "end": v(2.3, 2.3) * mm});
            skLineSegment(sketch, "E9.6.23.16", {"start": v(2.3, 2.3) * mm, "end": v(1.9, 2.3) * mm});
            skLineSegment(sketch, "E9.9.23.16", {"start": v(2.3, 1.9) * mm, "end": v(1.9, 1.9) * mm});
            skLineSegment(sketch, "E9.0.23.17", {"start": v(1.9, 1.3) * mm, "end": v(1.9, 1.7) * mm});
            skLineSegment(sketch, "E9.3.23.17", {"start": v(2.3, 1.3) * mm, "end": v(2.3, 1.7) * mm});
            skLineSegment(sketch, "E9.6.23.17", {"start": v(2.3, 1.7) * mm, "end": v(1.9, 1.7) * mm});
            skLineSegment(sketch, "E9.9.23.17", {"start": v(2.3, 1.3) * mm, "end": v(1.9, 1.3) * mm});
            skLineSegment(sketch, "E9.0.24.15", {"start": v(2.5, 2.5) * mm, "end": v(2.5, 2.9) * mm});
            skLineSegment(sketch, "E9.3.24.15", {"start": v(2.9, 2.5) * mm, "end": v(2.9, 2.9) * mm});
            skLineSegment(sketch, "E9.6.24.15", {"start": v(2.9, 2.9) * mm, "end": v(2.5, 2.9) * mm});
            skLineSegment(sketch, "E9.9.24.15", {"start": v(2.9, 2.5) * mm, "end": v(2.5, 2.5) * mm});
            skLineSegment(sketch, "E9.0.24.16", {"start": v(2.5, 1.9) * mm, "end": v(2.5, 2.3) * mm});
            skLineSegment(sketch, "E9.3.24.16", {"start": v(2.9, 1.9) * mm, "end": v(2.9, 2.3) * mm});
            skLineSegment(sketch, "E9.6.24.16", {"start": v(2.9, 2.3) * mm, "end": v(2.5, 2.3) * mm});
            skLineSegment(sketch, "E9.9.24.16", {"start": v(2.9, 1.9) * mm, "end": v(2.5, 1.9) * mm});
            skLineSegment(sketch, "E9.0.24.17", {"start": v(2.5, 1.3) * mm, "end": v(2.5, 1.7) * mm});
            skLineSegment(sketch, "E9.3.24.17", {"start": v(2.9, 1.3) * mm, "end": v(2.9, 1.7) * mm});
            skLineSegment(sketch, "E9.6.24.17", {"start": v(2.9, 1.7) * mm, "end": v(2.5, 1.7) * mm});
            skLineSegment(sketch, "E9.9.24.17", {"start": v(2.9, 1.3) * mm, "end": v(2.5, 1.3) * mm});
            skLineSegment(sketch, "E9.0.25.15", {"start": v(3.1, 2.5) * mm, "end": v(3.1, 2.9) * mm});
            skLineSegment(sketch, "E9.3.25.15", {"start": v(3.5, 2.5) * mm, "end": v(3.5, 2.9) * mm});
            skLineSegment(sketch, "E9.6.25.15", {"start": v(3.5, 2.9) * mm, "end": v(3.1, 2.9) * mm});
            skLineSegment(sketch, "E9.9.25.15", {"start": v(3.5, 2.5) * mm, "end": v(3.1, 2.5) * mm});
            skLineSegment(sketch, "E9.0.25.16", {"start": v(3.1, 1.9) * mm, "end": v(3.1, 2.3) * mm});
            skLineSegment(sketch, "E9.3.25.16", {"start": v(3.5, 1.9) * mm, "end": v(3.5, 2.3) * mm});
            skLineSegment(sketch, "E9.6.25.16", {"start": v(3.5, 2.3) * mm, "end": v(3.1, 2.3) * mm});
            skLineSegment(sketch, "E9.9.25.16", {"start": v(3.5, 1.9) * mm, "end": v(3.1, 1.9) * mm});
            skLineSegment(sketch, "E9.0.25.17", {"start": v(3.1, 1.3) * mm, "end": v(3.1, 1.7) * mm});
            skLineSegment(sketch, "E9.3.25.17", {"start": v(3.5, 1.3) * mm, "end": v(3.5, 1.7) * mm});
            skLineSegment(sketch, "E9.6.25.17", {"start": v(3.5, 1.7) * mm, "end": v(3.1, 1.7) * mm});
            skLineSegment(sketch, "E9.9.25.17", {"start": v(3.5, 1.3) * mm, "end": v(3.1, 1.3) * mm});
            skLineSegment(sketch, "E9.0.26.15", {"start": v(3.7, 2.5) * mm, "end": v(3.7, 2.9) * mm});
            skLineSegment(sketch, "E9.3.26.15", {"start": v(4.1, 2.5) * mm, "end": v(4.1, 2.9) * mm});
            skLineSegment(sketch, "E9.6.26.15", {"start": v(4.1, 2.9) * mm, "end": v(3.7, 2.9) * mm});
            skLineSegment(sketch, "E9.9.26.15", {"start": v(4.1, 2.5) * mm, "end": v(3.7, 2.5) * mm});
            skLineSegment(sketch, "E9.0.26.16", {"start": v(3.7, 1.9) * mm, "end": v(3.7, 2.3) * mm});
            skLineSegment(sketch, "E9.3.26.16", {"start": v(4.1, 1.9) * mm, "end": v(4.1, 2.3) * mm});
            skLineSegment(sketch, "E9.6.26.16", {"start": v(4.1, 2.3) * mm, "end": v(3.7, 2.3) * mm});
            skLineSegment(sketch, "E9.9.26.16", {"start": v(4.1, 1.9) * mm, "end": v(3.7, 1.9) * mm});
            skLineSegment(sketch, "E9.0.26.17", {"start": v(3.7, 1.3) * mm, "end": v(3.7, 1.7) * mm});
            skLineSegment(sketch, "E9.3.26.17", {"start": v(4.1, 1.3) * mm, "end": v(4.1, 1.7) * mm});
            skLineSegment(sketch, "E9.6.26.17", {"start": v(4.1, 1.7) * mm, "end": v(3.7, 1.7) * mm});
            skLineSegment(sketch, "E9.9.26.17", {"start": v(4.1, 1.3) * mm, "end": v(3.7, 1.3) * mm});
            skLineSegment(sketch, "E9.0.27.15", {"start": v(4.3, 2.5) * mm, "end": v(4.3, 2.9) * mm});
            skLineSegment(sketch, "E9.3.27.15", {"start": v(4.7, 2.5) * mm, "end": v(4.7, 2.9) * mm});
            skLineSegment(sketch, "E9.6.27.15", {"start": v(4.7, 2.9) * mm, "end": v(4.3, 2.9) * mm});
            skLineSegment(sketch, "E9.9.27.15", {"start": v(4.7, 2.5) * mm, "end": v(4.3, 2.5) * mm});
            skLineSegment(sketch, "E9.0.27.16", {"start": v(4.3, 1.9) * mm, "end": v(4.3, 2.3) * mm});
            skLineSegment(sketch, "E9.3.27.16", {"start": v(4.7, 1.9) * mm, "end": v(4.7, 2.3) * mm});
            skLineSegment(sketch, "E9.6.27.16", {"start": v(4.7, 2.3) * mm, "end": v(4.3, 2.3) * mm});
            skLineSegment(sketch, "E9.9.27.16", {"start": v(4.7, 1.9) * mm, "end": v(4.3, 1.9) * mm});
            skLineSegment(sketch, "E9.0.27.17", {"start": v(4.3, 1.3) * mm, "end": v(4.3, 1.7) * mm});
            skLineSegment(sketch, "E9.3.27.17", {"start": v(4.7, 1.3) * mm, "end": v(4.7, 1.7) * mm});
            skLineSegment(sketch, "E9.6.27.17", {"start": v(4.7, 1.7) * mm, "end": v(4.3, 1.7) * mm});
            skLineSegment(sketch, "E9.9.27.17", {"start": v(4.7, 1.3) * mm, "end": v(4.3, 1.3) * mm});
            skLineSegment(sketch, "E9.0.28.15", {"start": v(4.9, 2.5) * mm, "end": v(4.9, 2.9) * mm});
            skLineSegment(sketch, "E9.3.28.15", {"start": v(5.3, 2.5) * mm, "end": v(5.3, 2.9) * mm});
            skLineSegment(sketch, "E9.6.28.15", {"start": v(5.3, 2.9) * mm, "end": v(4.9, 2.9) * mm});
            skLineSegment(sketch, "E9.9.28.15", {"start": v(5.3, 2.5) * mm, "end": v(4.9, 2.5) * mm});
            skLineSegment(sketch, "E9.0.28.16", {"start": v(4.9, 1.9) * mm, "end": v(4.9, 2.3) * mm});
            skLineSegment(sketch, "E9.3.28.16", {"start": v(5.3, 1.9) * mm, "end": v(5.3, 2.3) * mm});
            skLineSegment(sketch, "E9.6.28.16", {"start": v(5.3, 2.3) * mm, "end": v(4.9, 2.3) * mm});
            skLineSegment(sketch, "E9.9.28.16", {"start": v(5.3, 1.9) * mm, "end": v(4.9, 1.9) * mm});
            skLineSegment(sketch, "E9.0.28.17", {"start": v(4.9, 1.3) * mm, "end": v(4.9, 1.7) * mm});
            skLineSegment(sketch, "E9.3.28.17", {"start": v(5.3, 1.3) * mm, "end": v(5.3, 1.7) * mm});
            skLineSegment(sketch, "E9.6.28.17", {"start": v(5.3, 1.7) * mm, "end": v(4.9, 1.7) * mm});
            skLineSegment(sketch, "E9.9.28.17", {"start": v(5.3, 1.3) * mm, "end": v(4.9, 1.3) * mm});
            skLineSegment(sketch, "E9.0.29.15", {"start": v(5.5, 2.5) * mm, "end": v(5.5, 2.9) * mm});
            skLineSegment(sketch, "E9.3.29.15", {"start": v(5.9, 2.5) * mm, "end": v(5.9, 2.9) * mm});
            skLineSegment(sketch, "E9.6.29.15", {"start": v(5.9, 2.9) * mm, "end": v(5.5, 2.9) * mm});
            skLineSegment(sketch, "E9.9.29.15", {"start": v(5.9, 2.5) * mm, "end": v(5.5, 2.5) * mm});
            skLineSegment(sketch, "E9.0.29.16", {"start": v(5.5, 1.9) * mm, "end": v(5.5, 2.3) * mm});
            skLineSegment(sketch, "E9.3.29.16", {"start": v(5.9, 1.9) * mm, "end": v(5.9, 2.3) * mm});
            skLineSegment(sketch, "E9.6.29.16", {"start": v(5.9, 2.3) * mm, "end": v(5.5, 2.3) * mm});
            skLineSegment(sketch, "E9.9.29.16", {"start": v(5.9, 1.9) * mm, "end": v(5.5, 1.9) * mm});
            skLineSegment(sketch, "E9.0.29.17", {"start": v(5.5, 1.3) * mm, "end": v(5.5, 1.7) * mm});
            skLineSegment(sketch, "E9.3.29.17", {"start": v(5.9, 1.3) * mm, "end": v(5.9, 1.7) * mm});
            skLineSegment(sketch, "E9.6.29.17", {"start": v(5.9, 1.7) * mm, "end": v(5.5, 1.7) * mm});
            skLineSegment(sketch, "E9.9.29.17", {"start": v(5.9, 1.3) * mm, "end": v(5.5, 1.3) * mm});
            skLineSegment(sketch, "E9.0.30.15", {"start": v(6.1, 2.5) * mm, "end": v(6.1, 2.9) * mm});
            skLineSegment(sketch, "E9.3.30.15", {"start": v(6.5, 2.5) * mm, "end": v(6.5, 2.9) * mm});
            skLineSegment(sketch, "E9.6.30.15", {"start": v(6.5, 2.9) * mm, "end": v(6.1, 2.9) * mm});
            skLineSegment(sketch, "E9.9.30.15", {"start": v(6.5, 2.5) * mm, "end": v(6.1, 2.5) * mm});
            skLineSegment(sketch, "E9.0.30.16", {"start": v(6.1, 1.9) * mm, "end": v(6.1, 2.3) * mm});
            skLineSegment(sketch, "E9.3.30.16", {"start": v(6.5, 1.9) * mm, "end": v(6.5, 2.3) * mm});
            skLineSegment(sketch, "E9.6.30.16", {"start": v(6.5, 2.3) * mm, "end": v(6.1, 2.3) * mm});
            skLineSegment(sketch, "E9.9.30.16", {"start": v(6.5, 1.9) * mm, "end": v(6.1, 1.9) * mm});
            skLineSegment(sketch, "E9.0.30.17", {"start": v(6.1, 1.3) * mm, "end": v(6.1, 1.7) * mm});
            skLineSegment(sketch, "E9.3.30.17", {"start": v(6.5, 1.3) * mm, "end": v(6.5, 1.7) * mm});
            skLineSegment(sketch, "E9.6.30.17", {"start": v(6.5, 1.7) * mm, "end": v(6.1, 1.7) * mm});
            skLineSegment(sketch, "E9.9.30.17", {"start": v(6.5, 1.3) * mm, "end": v(6.1, 1.3) * mm});
            skLineSegment(sketch, "E9.0.31.15", {"start": v(6.7, 2.5) * mm, "end": v(6.7, 2.9) * mm});
            skLineSegment(sketch, "E9.3.31.15", {"start": v(7.1, 2.5) * mm, "end": v(7.1, 2.9) * mm});
            skLineSegment(sketch, "E9.6.31.15", {"start": v(7.1, 2.9) * mm, "end": v(6.7, 2.9) * mm});
            skLineSegment(sketch, "E9.9.31.15", {"start": v(7.1, 2.5) * mm, "end": v(6.7, 2.5) * mm});
            skLineSegment(sketch, "E9.0.31.16", {"start": v(6.7, 1.9) * mm, "end": v(6.7, 2.3) * mm});
            skLineSegment(sketch, "E9.3.31.16", {"start": v(7.1, 1.9) * mm, "end": v(7.1, 2.3) * mm});
            skLineSegment(sketch, "E9.6.31.16", {"start": v(7.1, 2.3) * mm, "end": v(6.7, 2.3) * mm});
            skLineSegment(sketch, "E9.9.31.16", {"start": v(7.1, 1.9) * mm, "end": v(6.7, 1.9) * mm});
            skLineSegment(sketch, "E9.0.31.17", {"start": v(6.7, 1.3) * mm, "end": v(6.7, 1.7) * mm});
            skLineSegment(sketch, "E9.3.31.17", {"start": v(7.1, 1.3) * mm, "end": v(7.1, 1.7) * mm});
            skLineSegment(sketch, "E9.6.31.17", {"start": v(7.1, 1.7) * mm, "end": v(6.7, 1.7) * mm});
            skLineSegment(sketch, "E9.9.31.17", {"start": v(7.1, 1.3) * mm, "end": v(6.7, 1.3) * mm});
            skLineSegment(sketch, "E9.0.32.15", {"start": v(7.3, 2.5) * mm, "end": v(7.3, 2.9) * mm});
            skLineSegment(sketch, "E9.3.32.15", {"start": v(7.7, 2.5) * mm, "end": v(7.7, 2.9) * mm});
            skLineSegment(sketch, "E9.6.32.15", {"start": v(7.7, 2.9) * mm, "end": v(7.3, 2.9) * mm});
            skLineSegment(sketch, "E9.9.32.15", {"start": v(7.7, 2.5) * mm, "end": v(7.3, 2.5) * mm});
            skLineSegment(sketch, "E9.0.32.16", {"start": v(7.3, 1.9) * mm, "end": v(7.3, 2.3) * mm});
            skLineSegment(sketch, "E9.3.32.16", {"start": v(7.7, 1.9) * mm, "end": v(7.7, 2.3) * mm});
            skLineSegment(sketch, "E9.6.32.16", {"start": v(7.7, 2.3) * mm, "end": v(7.3, 2.3) * mm});
            skLineSegment(sketch, "E9.9.32.16", {"start": v(7.7, 1.9) * mm, "end": v(7.3, 1.9) * mm});
            skLineSegment(sketch, "E9.0.32.17", {"start": v(7.3, 1.3) * mm, "end": v(7.3, 1.7) * mm});
            skLineSegment(sketch, "E9.3.32.17", {"start": v(7.7, 1.3) * mm, "end": v(7.7, 1.7) * mm});
            skLineSegment(sketch, "E9.6.32.17", {"start": v(7.7, 1.7) * mm, "end": v(7.3, 1.7) * mm});
            skLineSegment(sketch, "E9.9.32.17", {"start": v(7.7, 1.3) * mm, "end": v(7.3, 1.3) * mm});
            skLineSegment(sketch, "E9.0.33.15", {"start": v(7.9, 2.5) * mm, "end": v(7.9, 2.9) * mm});
            skLineSegment(sketch, "E9.3.33.15", {"start": v(8.3, 2.5) * mm, "end": v(8.3, 2.9) * mm});
            skLineSegment(sketch, "E9.6.33.15", {"start": v(8.3, 2.9) * mm, "end": v(7.9, 2.9) * mm});
            skLineSegment(sketch, "E9.9.33.15", {"start": v(8.3, 2.5) * mm, "end": v(7.9, 2.5) * mm});
            skLineSegment(sketch, "E9.0.33.16", {"start": v(7.9, 1.9) * mm, "end": v(7.9, 2.3) * mm});
            skLineSegment(sketch, "E9.3.33.16", {"start": v(8.3, 1.9) * mm, "end": v(8.3, 2.3) * mm});
            skLineSegment(sketch, "E9.6.33.16", {"start": v(8.3, 2.3) * mm, "end": v(7.9, 2.3) * mm});
            skLineSegment(sketch, "E9.9.33.16", {"start": v(8.3, 1.9) * mm, "end": v(7.9, 1.9) * mm});
            skLineSegment(sketch, "E9.0.33.17", {"start": v(7.9, 1.3) * mm, "end": v(7.9, 1.7) * mm});
            skLineSegment(sketch, "E9.3.33.17", {"start": v(8.3, 1.3) * mm, "end": v(8.3, 1.7) * mm});
            skLineSegment(sketch, "E9.6.33.17", {"start": v(8.3, 1.7) * mm, "end": v(7.9, 1.7) * mm});
            skLineSegment(sketch, "E9.9.33.17", {"start": v(8.3, 1.3) * mm, "end": v(7.9, 1.3) * mm});
            skLineSegment(sketch, "E9.0.34.15", {"start": v(8.5, 2.5) * mm, "end": v(8.5, 2.9) * mm});
            skLineSegment(sketch, "E9.3.34.15", {"start": v(8.9, 2.5) * mm, "end": v(8.9, 2.9) * mm});
            skLineSegment(sketch, "E9.6.34.15", {"start": v(8.9, 2.9) * mm, "end": v(8.5, 2.9) * mm});
            skLineSegment(sketch, "E9.9.34.15", {"start": v(8.9, 2.5) * mm, "end": v(8.5, 2.5) * mm});
            skLineSegment(sketch, "E9.0.34.16", {"start": v(8.5, 1.9) * mm, "end": v(8.5, 2.3) * mm});
            skLineSegment(sketch, "E9.3.34.16", {"start": v(8.9, 1.9) * mm, "end": v(8.9, 2.3) * mm});
            skLineSegment(sketch, "E9.6.34.16", {"start": v(8.9, 2.3) * mm, "end": v(8.5, 2.3) * mm});
            skLineSegment(sketch, "E9.9.34.16", {"start": v(8.9, 1.9) * mm, "end": v(8.5, 1.9) * mm});
            skLineSegment(sketch, "E9.0.34.17", {"start": v(8.5, 1.3) * mm, "end": v(8.5, 1.7) * mm});
            skLineSegment(sketch, "E9.3.34.17", {"start": v(8.9, 1.3) * mm, "end": v(8.9, 1.7) * mm});
            skLineSegment(sketch, "E9.6.34.17", {"start": v(8.9, 1.7) * mm, "end": v(8.5, 1.7) * mm});
            skLineSegment(sketch, "E9.9.34.17", {"start": v(8.9, 1.3) * mm, "end": v(8.5, 1.3) * mm});
            skLineSegment(sketch, "E9.0.35.15", {"start": v(9.1, 2.5) * mm, "end": v(9.1, 2.9) * mm});
            skLineSegment(sketch, "E9.3.35.15", {"start": v(9.5, 2.5) * mm, "end": v(9.5, 2.9) * mm});
            skLineSegment(sketch, "E9.6.35.15", {"start": v(9.5, 2.9) * mm, "end": v(9.1, 2.9) * mm});
            skLineSegment(sketch, "E9.9.35.15", {"start": v(9.5, 2.5) * mm, "end": v(9.1, 2.5) * mm});
            skLineSegment(sketch, "E9.0.35.16", {"start": v(9.1, 1.9) * mm, "end": v(9.1, 2.3) * mm});
            skLineSegment(sketch, "E9.3.35.16", {"start": v(9.5, 1.9) * mm, "end": v(9.5, 2.3) * mm});
            skLineSegment(sketch, "E9.6.35.16", {"start": v(9.5, 2.3) * mm, "end": v(9.1, 2.3) * mm});
            skLineSegment(sketch, "E9.9.35.16", {"start": v(9.5, 1.9) * mm, "end": v(9.1, 1.9) * mm});
            skLineSegment(sketch, "E9.0.35.17", {"start": v(9.1, 1.3) * mm, "end": v(9.1, 1.7) * mm});
            skLineSegment(sketch, "E9.3.35.17", {"start": v(9.5, 1.3) * mm, "end": v(9.5, 1.7) * mm});
            skLineSegment(sketch, "E9.6.35.17", {"start": v(9.5, 1.7) * mm, "end": v(9.1, 1.7) * mm});
            skLineSegment(sketch, "E9.9.35.17", {"start": v(9.5, 1.3) * mm, "end": v(9.1, 1.3) * mm});
            skLineSegment(sketch, "E9.0.36.15", {"start": v(9.7, 2.5) * mm, "end": v(9.7, 2.9) * mm});
            skLineSegment(sketch, "E9.3.36.15", {"start": v(10.1, 2.5) * mm, "end": v(10.1, 2.9) * mm});
            skLineSegment(sketch, "E9.6.36.15", {"start": v(10.1, 2.9) * mm, "end": v(9.7, 2.9) * mm});
            skLineSegment(sketch, "E9.9.36.15", {"start": v(10.1, 2.5) * mm, "end": v(9.7, 2.5) * mm});
            skLineSegment(sketch, "E9.0.36.16", {"start": v(9.7, 1.9) * mm, "end": v(9.7, 2.3) * mm});
            skLineSegment(sketch, "E9.3.36.16", {"start": v(10.1, 1.9) * mm, "end": v(10.1, 2.3) * mm});
            skLineSegment(sketch, "E9.6.36.16", {"start": v(10.1, 2.3) * mm, "end": v(9.7, 2.3) * mm});
            skLineSegment(sketch, "E9.9.36.16", {"start": v(10.1, 1.9) * mm, "end": v(9.7, 1.9) * mm});
            skLineSegment(sketch, "E9.0.36.17", {"start": v(9.7, 1.3) * mm, "end": v(9.7, 1.7) * mm});
            skLineSegment(sketch, "E9.3.36.17", {"start": v(10.1, 1.3) * mm, "end": v(10.1, 1.7) * mm});
            skLineSegment(sketch, "E9.6.36.17", {"start": v(10.1, 1.7) * mm, "end": v(9.7, 1.7) * mm});
            skLineSegment(sketch, "E9.9.36.17", {"start": v(10.1, 1.3) * mm, "end": v(9.7, 1.3) * mm});
            skLineSegment(sketch, "E9.0.37.15", {"start": v(10.3, 2.5) * mm, "end": v(10.3, 2.9) * mm});
            skLineSegment(sketch, "E9.3.37.15", {"start": v(10.7, 2.5) * mm, "end": v(10.7, 2.9) * mm});
            skLineSegment(sketch, "E9.6.37.15", {"start": v(10.7, 2.9) * mm, "end": v(10.3, 2.9) * mm});
            skLineSegment(sketch, "E9.9.37.15", {"start": v(10.7, 2.5) * mm, "end": v(10.3, 2.5) * mm});
            skLineSegment(sketch, "E9.0.37.16", {"start": v(10.3, 1.9) * mm, "end": v(10.3, 2.3) * mm});
            skLineSegment(sketch, "E9.3.37.16", {"start": v(10.7, 1.9) * mm, "end": v(10.7, 2.3) * mm});
            skLineSegment(sketch, "E9.6.37.16", {"start": v(10.7, 2.3) * mm, "end": v(10.3, 2.3) * mm});
            skLineSegment(sketch, "E9.9.37.16", {"start": v(10.7, 1.9) * mm, "end": v(10.3, 1.9) * mm});
            skLineSegment(sketch, "E9.0.37.17", {"start": v(10.3, 1.3) * mm, "end": v(10.3, 1.7) * mm});
            skLineSegment(sketch, "E9.3.37.17", {"start": v(10.7, 1.3) * mm, "end": v(10.7, 1.7) * mm});
            skLineSegment(sketch, "E9.6.37.17", {"start": v(10.7, 1.7) * mm, "end": v(10.3, 1.7) * mm});
            skLineSegment(sketch, "E9.9.37.17", {"start": v(10.7, 1.3) * mm, "end": v(10.3, 1.3) * mm});
            skLineSegment(sketch, "E9.0.38.15", {"start": v(10.9, 2.5) * mm, "end": v(10.9, 2.9) * mm});
            skLineSegment(sketch, "E9.3.38.15", {"start": v(11.3, 2.5) * mm, "end": v(11.3, 2.9) * mm});
            skLineSegment(sketch, "E9.6.38.15", {"start": v(11.3, 2.9) * mm, "end": v(10.9, 2.9) * mm});
            skLineSegment(sketch, "E9.9.38.15", {"start": v(11.3, 2.5) * mm, "end": v(10.9, 2.5) * mm});
            skLineSegment(sketch, "E9.0.38.16", {"start": v(10.9, 1.9) * mm, "end": v(10.9, 2.3) * mm});
            skLineSegment(sketch, "E9.3.38.16", {"start": v(11.3, 1.9) * mm, "end": v(11.3, 2.3) * mm});
            skLineSegment(sketch, "E9.6.38.16", {"start": v(11.3, 2.3) * mm, "end": v(10.9, 2.3) * mm});
            skLineSegment(sketch, "E9.9.38.16", {"start": v(11.3, 1.9) * mm, "end": v(10.9, 1.9) * mm});
            skLineSegment(sketch, "E9.0.38.17", {"start": v(10.9, 1.3) * mm, "end": v(10.9, 1.7) * mm});
            skLineSegment(sketch, "E9.3.38.17", {"start": v(11.3, 1.3) * mm, "end": v(11.3, 1.7) * mm});
            skLineSegment(sketch, "E9.6.38.17", {"start": v(11.3, 1.7) * mm, "end": v(10.9, 1.7) * mm});
            skLineSegment(sketch, "E9.9.38.17", {"start": v(11.3, 1.3) * mm, "end": v(10.9, 1.3) * mm});
            skLineSegment(sketch, "E9.0.39.15", {"start": v(11.5, 2.5) * mm, "end": v(11.5, 2.9) * mm});
            skLineSegment(sketch, "E9.3.39.15", {"start": v(11.9, 2.5) * mm, "end": v(11.9, 2.9) * mm});
            skLineSegment(sketch, "E9.6.39.15", {"start": v(11.9, 2.9) * mm, "end": v(11.5, 2.9) * mm});
            skLineSegment(sketch, "E9.9.39.15", {"start": v(11.9, 2.5) * mm, "end": v(11.5, 2.5) * mm});
            skLineSegment(sketch, "E9.0.39.16", {"start": v(11.5, 1.9) * mm, "end": v(11.5, 2.3) * mm});
            skLineSegment(sketch, "E9.3.39.16", {"start": v(11.9, 1.9) * mm, "end": v(11.9, 2.3) * mm});
            skLineSegment(sketch, "E9.6.39.16", {"start": v(11.9, 2.3) * mm, "end": v(11.5, 2.3) * mm});
            skLineSegment(sketch, "E9.9.39.16", {"start": v(11.9, 1.9) * mm, "end": v(11.5, 1.9) * mm});
            skLineSegment(sketch, "E9.0.39.17", {"start": v(11.5, 1.3) * mm, "end": v(11.5, 1.7) * mm});
            skLineSegment(sketch, "E9.3.39.17", {"start": v(11.9, 1.3) * mm, "end": v(11.9, 1.7) * mm});
            skLineSegment(sketch, "E9.6.39.17", {"start": v(11.9, 1.7) * mm, "end": v(11.5, 1.7) * mm});
            skLineSegment(sketch, "E9.9.39.17", {"start": v(11.9, 1.3) * mm, "end": v(11.5, 1.3) * mm});
            skLineSegment(sketch, "E10.0.20.18", {"start": v(0.1, 0.7) * mm, "end": v(0.1, 1.1) * mm});
            skLineSegment(sketch, "E10.3.20.18", {"start": v(0.5, 0.7) * mm, "end": v(0.5, 1.1) * mm});
            skLineSegment(sketch, "E10.6.20.18", {"start": v(0.5, 1.1) * mm, "end": v(0.1, 1.1) * mm});
            skLineSegment(sketch, "E10.9.20.18", {"start": v(0.5, 0.7) * mm, "end": v(0.1, 0.7) * mm});
            skLineSegment(sketch, "E10.0.21.18", {"start": v(0.7, 0.7) * mm, "end": v(0.7, 1.1) * mm});
            skLineSegment(sketch, "E10.3.21.18", {"start": v(1.1, 0.7) * mm, "end": v(1.1, 1.1) * mm});
            skLineSegment(sketch, "E10.6.21.18", {"start": v(1.1, 1.1) * mm, "end": v(0.7, 1.1) * mm});
            skLineSegment(sketch, "E10.9.21.18", {"start": v(1.1, 0.7) * mm, "end": v(0.7, 0.7) * mm});
            skLineSegment(sketch, "E10.0.21.19", {"start": v(0.7, 0.1) * mm, "end": v(0.7, 0.5) * mm});
            skLineSegment(sketch, "E10.3.21.19", {"start": v(1.1, 0.1) * mm, "end": v(1.1, 0.5) * mm});
            skLineSegment(sketch, "E10.6.21.19", {"start": v(1.1, 0.5) * mm, "end": v(0.7, 0.5) * mm});
            skLineSegment(sketch, "E10.9.21.19", {"start": v(1.1, 0.1) * mm, "end": v(0.7, 0.1) * mm});
            skLineSegment(sketch, "E10.0.22.18", {"start": v(1.3, 0.7) * mm, "end": v(1.3, 1.1) * mm});
            skLineSegment(sketch, "E10.3.22.18", {"start": v(1.7, 0.7) * mm, "end": v(1.7, 1.1) * mm});
            skLineSegment(sketch, "E10.6.22.18", {"start": v(1.7, 1.1) * mm, "end": v(1.3, 1.1) * mm});
            skLineSegment(sketch, "E10.9.22.18", {"start": v(1.7, 0.7) * mm, "end": v(1.3, 0.7) * mm});
            skLineSegment(sketch, "E10.0.22.19", {"start": v(1.3, 0.1) * mm, "end": v(1.3, 0.5) * mm});
            skLineSegment(sketch, "E10.3.22.19", {"start": v(1.7, 0.1) * mm, "end": v(1.7, 0.5) * mm});
            skLineSegment(sketch, "E10.6.22.19", {"start": v(1.7, 0.5) * mm, "end": v(1.3, 0.5) * mm});
            skLineSegment(sketch, "E10.9.22.19", {"start": v(1.7, 0.1) * mm, "end": v(1.3, 0.1) * mm});
            skLineSegment(sketch, "E10.0.23.18", {"start": v(1.9, 0.7) * mm, "end": v(1.9, 1.1) * mm});
            skLineSegment(sketch, "E10.3.23.18", {"start": v(2.3, 0.7) * mm, "end": v(2.3, 1.1) * mm});
            skLineSegment(sketch, "E10.6.23.18", {"start": v(2.3, 1.1) * mm, "end": v(1.9, 1.1) * mm});
            skLineSegment(sketch, "E10.9.23.18", {"start": v(2.3, 0.7) * mm, "end": v(1.9, 0.7) * mm});
            skLineSegment(sketch, "E10.0.23.19", {"start": v(1.9, 0.1) * mm, "end": v(1.9, 0.5) * mm});
            skLineSegment(sketch, "E10.3.23.19", {"start": v(2.3, 0.1) * mm, "end": v(2.3, 0.5) * mm});
            skLineSegment(sketch, "E10.6.23.19", {"start": v(2.3, 0.5) * mm, "end": v(1.9, 0.5) * mm});
            skLineSegment(sketch, "E10.9.23.19", {"start": v(2.3, 0.1) * mm, "end": v(1.9, 0.1) * mm});
            skLineSegment(sketch, "E10.0.24.18", {"start": v(2.5, 0.7) * mm, "end": v(2.5, 1.1) * mm});
            skLineSegment(sketch, "E10.3.24.18", {"start": v(2.9, 0.7) * mm, "end": v(2.9, 1.1) * mm});
            skLineSegment(sketch, "E10.6.24.18", {"start": v(2.9, 1.1) * mm, "end": v(2.5, 1.1) * mm});
            skLineSegment(sketch, "E10.9.24.18", {"start": v(2.9, 0.7) * mm, "end": v(2.5, 0.7) * mm});
            skLineSegment(sketch, "E10.0.24.19", {"start": v(2.5, 0.1) * mm, "end": v(2.5, 0.5) * mm});
            skLineSegment(sketch, "E10.3.24.19", {"start": v(2.9, 0.1) * mm, "end": v(2.9, 0.5) * mm});
            skLineSegment(sketch, "E10.6.24.19", {"start": v(2.9, 0.5) * mm, "end": v(2.5, 0.5) * mm});
            skLineSegment(sketch, "E10.9.24.19", {"start": v(2.9, 0.1) * mm, "end": v(2.5, 0.1) * mm});
            skLineSegment(sketch, "E10.0.25.18", {"start": v(3.1, 0.7) * mm, "end": v(3.1, 1.1) * mm});
            skLineSegment(sketch, "E10.3.25.18", {"start": v(3.5, 0.7) * mm, "end": v(3.5, 1.1) * mm});
            skLineSegment(sketch, "E10.6.25.18", {"start": v(3.5, 1.1) * mm, "end": v(3.1, 1.1) * mm});
            skLineSegment(sketch, "E10.9.25.18", {"start": v(3.5, 0.7) * mm, "end": v(3.1, 0.7) * mm});
            skLineSegment(sketch, "E10.0.25.19", {"start": v(3.1, 0.1) * mm, "end": v(3.1, 0.5) * mm});
            skLineSegment(sketch, "E10.3.25.19", {"start": v(3.5, 0.1) * mm, "end": v(3.5, 0.5) * mm});
            skLineSegment(sketch, "E10.6.25.19", {"start": v(3.5, 0.5) * mm, "end": v(3.1, 0.5) * mm});
            skLineSegment(sketch, "E10.9.25.19", {"start": v(3.5, 0.1) * mm, "end": v(3.1, 0.1) * mm});
            skLineSegment(sketch, "E10.0.26.18", {"start": v(3.7, 0.7) * mm, "end": v(3.7, 1.1) * mm});
            skLineSegment(sketch, "E10.3.26.18", {"start": v(4.1, 0.7) * mm, "end": v(4.1, 1.1) * mm});
            skLineSegment(sketch, "E10.6.26.18", {"start": v(4.1, 1.1) * mm, "end": v(3.7, 1.1) * mm});
            skLineSegment(sketch, "E10.9.26.18", {"start": v(4.1, 0.7) * mm, "end": v(3.7, 0.7) * mm});
            skLineSegment(sketch, "E10.0.26.19", {"start": v(3.7, 0.1) * mm, "end": v(3.7, 0.5) * mm});
            skLineSegment(sketch, "E10.3.26.19", {"start": v(4.1, 0.1) * mm, "end": v(4.1, 0.5) * mm});
            skLineSegment(sketch, "E10.6.26.19", {"start": v(4.1, 0.5) * mm, "end": v(3.7, 0.5) * mm});
            skLineSegment(sketch, "E10.9.26.19", {"start": v(4.1, 0.1) * mm, "end": v(3.7, 0.1) * mm});
            skLineSegment(sketch, "E10.0.27.18", {"start": v(4.3, 0.7) * mm, "end": v(4.3, 1.1) * mm});
            skLineSegment(sketch, "E10.3.27.18", {"start": v(4.7, 0.7) * mm, "end": v(4.7, 1.1) * mm});
            skLineSegment(sketch, "E10.6.27.18", {"start": v(4.7, 1.1) * mm, "end": v(4.3, 1.1) * mm});
            skLineSegment(sketch, "E10.9.27.18", {"start": v(4.7, 0.7) * mm, "end": v(4.3, 0.7) * mm});
            skLineSegment(sketch, "E10.0.27.19", {"start": v(4.3, 0.1) * mm, "end": v(4.3, 0.5) * mm});
            skLineSegment(sketch, "E10.3.27.19", {"start": v(4.7, 0.1) * mm, "end": v(4.7, 0.5) * mm});
            skLineSegment(sketch, "E10.6.27.19", {"start": v(4.7, 0.5) * mm, "end": v(4.3, 0.5) * mm});
            skLineSegment(sketch, "E10.9.27.19", {"start": v(4.7, 0.1) * mm, "end": v(4.3, 0.1) * mm});
            skLineSegment(sketch, "E10.0.28.18", {"start": v(4.9, 0.7) * mm, "end": v(4.9, 1.1) * mm});
            skLineSegment(sketch, "E10.3.28.18", {"start": v(5.3, 0.7) * mm, "end": v(5.3, 1.1) * mm});
            skLineSegment(sketch, "E10.6.28.18", {"start": v(5.3, 1.1) * mm, "end": v(4.9, 1.1) * mm});
            skLineSegment(sketch, "E10.9.28.18", {"start": v(5.3, 0.7) * mm, "end": v(4.9, 0.7) * mm});
            skLineSegment(sketch, "E10.0.28.19", {"start": v(4.9, 0.1) * mm, "end": v(4.9, 0.5) * mm});
            skLineSegment(sketch, "E10.3.28.19", {"start": v(5.3, 0.1) * mm, "end": v(5.3, 0.5) * mm});
            skLineSegment(sketch, "E10.6.28.19", {"start": v(5.3, 0.5) * mm, "end": v(4.9, 0.5) * mm});
            skLineSegment(sketch, "E10.9.28.19", {"start": v(5.3, 0.1) * mm, "end": v(4.9, 0.1) * mm});
            skLineSegment(sketch, "E10.0.29.18", {"start": v(5.5, 0.7) * mm, "end": v(5.5, 1.1) * mm});
            skLineSegment(sketch, "E10.3.29.18", {"start": v(5.9, 0.7) * mm, "end": v(5.9, 1.1) * mm});
            skLineSegment(sketch, "E10.6.29.18", {"start": v(5.9, 1.1) * mm, "end": v(5.5, 1.1) * mm});
            skLineSegment(sketch, "E10.9.29.18", {"start": v(5.9, 0.7) * mm, "end": v(5.5, 0.7) * mm});
            skLineSegment(sketch, "E10.0.29.19", {"start": v(5.5, 0.1) * mm, "end": v(5.5, 0.5) * mm});
            skLineSegment(sketch, "E10.3.29.19", {"start": v(5.9, 0.1) * mm, "end": v(5.9, 0.5) * mm});
            skLineSegment(sketch, "E10.6.29.19", {"start": v(5.9, 0.5) * mm, "end": v(5.5, 0.5) * mm});
            skLineSegment(sketch, "E10.9.29.19", {"start": v(5.9, 0.1) * mm, "end": v(5.5, 0.1) * mm});
            skLineSegment(sketch, "E10.0.30.18", {"start": v(6.1, 0.7) * mm, "end": v(6.1, 1.1) * mm});
            skLineSegment(sketch, "E10.3.30.18", {"start": v(6.5, 0.7) * mm, "end": v(6.5, 1.1) * mm});
            skLineSegment(sketch, "E10.6.30.18", {"start": v(6.5, 1.1) * mm, "end": v(6.1, 1.1) * mm});
            skLineSegment(sketch, "E10.9.30.18", {"start": v(6.5, 0.7) * mm, "end": v(6.1, 0.7) * mm});
            skLineSegment(sketch, "E10.0.30.19", {"start": v(6.1, 0.1) * mm, "end": v(6.1, 0.5) * mm});
            skLineSegment(sketch, "E10.3.30.19", {"start": v(6.5, 0.1) * mm, "end": v(6.5, 0.5) * mm});
            skLineSegment(sketch, "E10.6.30.19", {"start": v(6.5, 0.5) * mm, "end": v(6.1, 0.5) * mm});
            skLineSegment(sketch, "E10.9.30.19", {"start": v(6.5, 0.1) * mm, "end": v(6.1, 0.1) * mm});
            skLineSegment(sketch, "E10.0.31.18", {"start": v(6.7, 0.7) * mm, "end": v(6.7, 1.1) * mm});
            skLineSegment(sketch, "E10.3.31.18", {"start": v(7.1, 0.7) * mm, "end": v(7.1, 1.1) * mm});
            skLineSegment(sketch, "E10.6.31.18", {"start": v(7.1, 1.1) * mm, "end": v(6.7, 1.1) * mm});
            skLineSegment(sketch, "E10.9.31.18", {"start": v(7.1, 0.7) * mm, "end": v(6.7, 0.7) * mm});
            skLineSegment(sketch, "E10.0.31.19", {"start": v(6.7, 0.1) * mm, "end": v(6.7, 0.5) * mm});
            skLineSegment(sketch, "E10.3.31.19", {"start": v(7.1, 0.1) * mm, "end": v(7.1, 0.5) * mm});
            skLineSegment(sketch, "E10.6.31.19", {"start": v(7.1, 0.5) * mm, "end": v(6.7, 0.5) * mm});
            skLineSegment(sketch, "E10.9.31.19", {"start": v(7.1, 0.1) * mm, "end": v(6.7, 0.1) * mm});
            skLineSegment(sketch, "E10.0.32.18", {"start": v(7.3, 0.7) * mm, "end": v(7.3, 1.1) * mm});
            skLineSegment(sketch, "E10.3.32.18", {"start": v(7.7, 0.7) * mm, "end": v(7.7, 1.1) * mm});
            skLineSegment(sketch, "E10.6.32.18", {"start": v(7.7, 1.1) * mm, "end": v(7.3, 1.1) * mm});
            skLineSegment(sketch, "E10.9.32.18", {"start": v(7.7, 0.7) * mm, "end": v(7.3, 0.7) * mm});
            skLineSegment(sketch, "E10.0.32.19", {"start": v(7.3, 0.1) * mm, "end": v(7.3, 0.5) * mm});
            skLineSegment(sketch, "E10.3.32.19", {"start": v(7.7, 0.1) * mm, "end": v(7.7, 0.5) * mm});
            skLineSegment(sketch, "E10.6.32.19", {"start": v(7.7, 0.5) * mm, "end": v(7.3, 0.5) * mm});
            skLineSegment(sketch, "E10.9.32.19", {"start": v(7.7, 0.1) * mm, "end": v(7.3, 0.1) * mm});
            skLineSegment(sketch, "E10.0.33.18", {"start": v(7.9, 0.7) * mm, "end": v(7.9, 1.1) * mm});
            skLineSegment(sketch, "E10.3.33.18", {"start": v(8.3, 0.7) * mm, "end": v(8.3, 1.1) * mm});
            skLineSegment(sketch, "E10.6.33.18", {"start": v(8.3, 1.1) * mm, "end": v(7.9, 1.1) * mm});
            skLineSegment(sketch, "E10.9.33.18", {"start": v(8.3, 0.7) * mm, "end": v(7.9, 0.7) * mm});
            skLineSegment(sketch, "E10.0.33.19", {"start": v(7.9, 0.1) * mm, "end": v(7.9, 0.5) * mm});
            skLineSegment(sketch, "E10.3.33.19", {"start": v(8.3, 0.1) * mm, "end": v(8.3, 0.5) * mm});
            skLineSegment(sketch, "E10.6.33.19", {"start": v(8.3, 0.5) * mm, "end": v(7.9, 0.5) * mm});
            skLineSegment(sketch, "E10.9.33.19", {"start": v(8.3, 0.1) * mm, "end": v(7.9, 0.1) * mm});
            skLineSegment(sketch, "E10.0.34.18", {"start": v(8.5, 0.7) * mm, "end": v(8.5, 1.1) * mm});
            skLineSegment(sketch, "E10.3.34.18", {"start": v(8.9, 0.7) * mm, "end": v(8.9, 1.1) * mm});
            skLineSegment(sketch, "E10.6.34.18", {"start": v(8.9, 1.1) * mm, "end": v(8.5, 1.1) * mm});
            skLineSegment(sketch, "E10.9.34.18", {"start": v(8.9, 0.7) * mm, "end": v(8.5, 0.7) * mm});
            skLineSegment(sketch, "E10.0.34.19", {"start": v(8.5, 0.1) * mm, "end": v(8.5, 0.5) * mm});
            skLineSegment(sketch, "E10.3.34.19", {"start": v(8.9, 0.1) * mm, "end": v(8.9, 0.5) * mm});
            skLineSegment(sketch, "E10.6.34.19", {"start": v(8.9, 0.5) * mm, "end": v(8.5, 0.5) * mm});
            skLineSegment(sketch, "E10.9.34.19", {"start": v(8.9, 0.1) * mm, "end": v(8.5, 0.1) * mm});
            skLineSegment(sketch, "E10.0.35.18", {"start": v(9.1, 0.7) * mm, "end": v(9.1, 1.1) * mm});
            skLineSegment(sketch, "E10.3.35.18", {"start": v(9.5, 0.7) * mm, "end": v(9.5, 1.1) * mm});
            skLineSegment(sketch, "E10.6.35.18", {"start": v(9.5, 1.1) * mm, "end": v(9.1, 1.1) * mm});
            skLineSegment(sketch, "E10.9.35.18", {"start": v(9.5, 0.7) * mm, "end": v(9.1, 0.7) * mm});
            skLineSegment(sketch, "E10.0.35.19", {"start": v(9.1, 0.1) * mm, "end": v(9.1, 0.5) * mm});
            skLineSegment(sketch, "E10.3.35.19", {"start": v(9.5, 0.1) * mm, "end": v(9.5, 0.5) * mm});
            skLineSegment(sketch, "E10.6.35.19", {"start": v(9.5, 0.5) * mm, "end": v(9.1, 0.5) * mm});
            skLineSegment(sketch, "E10.9.35.19", {"start": v(9.5, 0.1) * mm, "end": v(9.1, 0.1) * mm});
            skLineSegment(sketch, "E10.0.36.18", {"start": v(9.7, 0.7) * mm, "end": v(9.7, 1.1) * mm});
            skLineSegment(sketch, "E10.3.36.18", {"start": v(10.1, 0.7) * mm, "end": v(10.1, 1.1) * mm});
            skLineSegment(sketch, "E10.6.36.18", {"start": v(10.1, 1.1) * mm, "end": v(9.7, 1.1) * mm});
            skLineSegment(sketch, "E10.9.36.18", {"start": v(10.1, 0.7) * mm, "end": v(9.7, 0.7) * mm});
            skLineSegment(sketch, "E10.0.36.19", {"start": v(9.7, 0.1) * mm, "end": v(9.7, 0.5) * mm});
            skLineSegment(sketch, "E10.3.36.19", {"start": v(10.1, 0.1) * mm, "end": v(10.1, 0.5) * mm});
            skLineSegment(sketch, "E10.6.36.19", {"start": v(10.1, 0.5) * mm, "end": v(9.7, 0.5) * mm});
            skLineSegment(sketch, "E10.9.36.19", {"start": v(10.1, 0.1) * mm, "end": v(9.7, 0.1) * mm});
            skLineSegment(sketch, "E10.0.37.18", {"start": v(10.3, 0.7) * mm, "end": v(10.3, 1.1) * mm});
            skLineSegment(sketch, "E10.3.37.18", {"start": v(10.7, 0.7) * mm, "end": v(10.7, 1.1) * mm});
            skLineSegment(sketch, "E10.6.37.18", {"start": v(10.7, 1.1) * mm, "end": v(10.3, 1.1) * mm});
            skLineSegment(sketch, "E10.9.37.18", {"start": v(10.7, 0.7) * mm, "end": v(10.3, 0.7) * mm});
            skLineSegment(sketch, "E10.0.37.19", {"start": v(10.3, 0.1) * mm, "end": v(10.3, 0.5) * mm});
            skLineSegment(sketch, "E10.3.37.19", {"start": v(10.7, 0.1) * mm, "end": v(10.7, 0.5) * mm});
            skLineSegment(sketch, "E10.6.37.19", {"start": v(10.7, 0.5) * mm, "end": v(10.3, 0.5) * mm});
            skLineSegment(sketch, "E10.9.37.19", {"start": v(10.7, 0.1) * mm, "end": v(10.3, 0.1) * mm});
            skLineSegment(sketch, "E10.0.38.18", {"start": v(10.9, 0.7) * mm, "end": v(10.9, 1.1) * mm});
            skLineSegment(sketch, "E10.3.38.18", {"start": v(11.3, 0.7) * mm, "end": v(11.3, 1.1) * mm});
            skLineSegment(sketch, "E10.6.38.18", {"start": v(11.3, 1.1) * mm, "end": v(10.9, 1.1) * mm});
            skLineSegment(sketch, "E10.9.38.18", {"start": v(11.3, 0.7) * mm, "end": v(10.9, 0.7) * mm});
            skLineSegment(sketch, "E10.0.38.19", {"start": v(10.9, 0.1) * mm, "end": v(10.9, 0.5) * mm});
            skLineSegment(sketch, "E10.3.38.19", {"start": v(11.3, 0.1) * mm, "end": v(11.3, 0.5) * mm});
            skLineSegment(sketch, "E10.6.38.19", {"start": v(11.3, 0.5) * mm, "end": v(10.9, 0.5) * mm});
            skLineSegment(sketch, "E10.9.38.19", {"start": v(11.3, 0.1) * mm, "end": v(10.9, 0.1) * mm});
            skLineSegment(sketch, "E10.0.39.18", {"start": v(11.5, 0.7) * mm, "end": v(11.5, 1.1) * mm});
            skLineSegment(sketch, "E10.3.39.18", {"start": v(11.9, 0.7) * mm, "end": v(11.9, 1.1) * mm});
            skLineSegment(sketch, "E10.6.39.18", {"start": v(11.9, 1.1) * mm, "end": v(11.5, 1.1) * mm});
            skLineSegment(sketch, "E10.9.39.18", {"start": v(11.9, 0.7) * mm, "end": v(11.5, 0.7) * mm});
            skLineSegment(sketch, "E10.0.39.19", {"start": v(11.5, 0.1) * mm, "end": v(11.5, 0.5) * mm});
            skLineSegment(sketch, "E10.3.39.19", {"start": v(11.9, 0.1) * mm, "end": v(11.9, 0.5) * mm});
            skLineSegment(sketch, "E10.6.39.19", {"start": v(11.9, 0.5) * mm, "end": v(11.5, 0.5) * mm});
            skLineSegment(sketch, "E10.9.39.19", {"start": v(11.9, 0.1) * mm, "end": v(11.5, 0.1) * mm});
            skLineSegment(sketch, "E11", {"start": v(-11.9, 0) * mm, "end": v(11.9, 0) * mm, "construction": true});
            skLineSegment(sketch, "E12.0", {"start": v(-11.9, 0.1) * mm, "end": v(11.9, 0.1) * mm, "construction": true});
            skSolve(sketch);
        }
        {
            var Q0;
            Q0 = qSketchRegion(id + "F3", true);
            extrude(context, id + "F4", {"entities" : qUnion([Q0]), "operationType" : NewBodyOperationType.REMOVE, "depth" : 25 * mm, "offsetDistance" : 25 * mm});
        }
        {
            var Q0;
            Q0=qCreatedBy(makeId("Top.planeOp"),FACE);
            cPlane(context, id + "F5", {"entities" : qUnion([Q0]), "cplaneType" : CPlaneType.OFFSET, "offset" : 10 * mm, "oppositeDirection" : true, "width" : 150 * mm, "height" : 150 * mm});
        }
        {
            var Q0;
            Q0=qCreatedBy(id+"F5.planeOp",FACE);
            var sketch = newSketch(context, id + "F6", { "sketchPlane" : qUnion([Q0])});
            skCircle(sketch, "E13", {"center": v(0, 0) * mm, "radius": 12.7 * mm});
            skCircle(sketch, "E14", {"center": v(0, 0) * mm, "radius": 11.9 * mm});
            skSolve(sketch);
        }
        {
            var Q0;
            Q0=makeQuery(id+"F6.imprint","IMPRINT",FACE,{"disambiguationData":[TD([[makeQuery(id+"F6.imprint","IMPRINT",EDGE,{"derivedFrom":sQuery(id+"F6.wireOp",EDGE,"E13")}),1.0]])]});
            extrude(context, id + "F7", {"entities" : qUnion([Q0]), "depth" : 1 / 101.6 * mm, "offsetDistance" : 25 * mm});
        }
        {
            var Q0;
            Q0=qCreatedBy(makeId("Front.planeOp"),FACE);
            var sketch = newSketch(context, id + "F8", { "sketchPlane" : qUnion([Q0])});
            skLineSegment(sketch, "E15.bottom", {"start": v(0, -20.2) * mm, "end": v(10.95, -20.2) * mm});
            skLineSegment(sketch, "E15.top", {"start": v(0, -20.6) * mm, "end": v(10.82, -20.6) * mm});
            skLineSegment(sketch, "E15.left", {"start": v(0, -20.2) * mm, "end": v(0, -20.6) * mm});
            skLineSegment(sketch, "E16.top", {"start": v(11.9, -17.42) * mm, "end": v(11.5, -17.42) * mm});
            skLineSegment(sketch, "E16.left", {"start": v(11.9, -19.5) * mm, "end": v(11.9, -17.42) * mm});
            skLineSegment(sketch, "E16.right", {"start": v(11.5, -19.64) * mm, "end": v(11.5, -17.42) * mm});
            skPoint(sketch, "E17.visualSharp", {"position": v(11.5, -20.2) * mm});
            skArc(sketch, "E17.filletArc", {"start": v(10.95, -20.2) * mm, "mid": v(11.34, -20.03) * mm, "end": v(11.5, -19.64) * mm});
            skArc(sketch, "E18.filletArc", {"start": v(10.82, -20.6) * mm, "mid": v(11.59, -20.28) * mm, "end": v(11.9, -19.5) * mm});
            skLineSegment(sketch, "E19", {"start": v(11.9, -17.42) * mm, "end": v(0, -17.42) * mm, "construction": true});
            skPoint(sketch, "E19.endSnap0", {"position": v(11.7, -17.42) * mm});
            skSolve(sketch);
        }
        {
            var Q0;
            Q0 = qSketchRegion(id + "F8", true);
            var Q1;
            Q1=sQuery(id+"F8.wireOp",EDGE,"E15.left");
            revolve(context, id + "F9", {"surfaceOperationType" : NewSurfaceOperationType.NEW, "entities" : qUnion([Q0]), "axis" : qUnion([Q1]), "revolveType" : RevolveType.FULL});
        }
        {
            var Q0;
            Q0=qCreatedBy(makeId("Front.planeOp"),FACE);
            var sketch = newSketch(context, id + "F10", { "sketchPlane" : qUnion([Q0])});
            skLineSegment(sketch, "E20", {"start": v(11.38, -6.62) * mm, "end": v(39.04, -6.62) * mm, "construction": true});
            skLineSegment(sketch, "E21.bottom", {"start": v(17.19, -8.6) * mm, "end": v(29.89, -8.6) * mm});
            skLineSegment(sketch, "E21.top", {"start": v(17.19, -8.21) * mm, "end": v(25.13, -8.21) * mm});
            skLineSegment(sketch, "E21.left", {"start": v(17.19, -8.6) * mm, "end": v(17.19, -8.21) * mm});
            skLineSegment(sketch, "E22.top", {"start": v(29.89, -7.62) * mm, "end": v(25.13, -7.62) * mm});
            skLineSegment(sketch, "E22.right", {"start": v(25.13, -8.21) * mm, "end": v(25.13, -7.62) * mm});
            skLineSegment(sketch, "E23", {"start": v(29.89, -7.62) * mm, "end": v(29.89, -6.62) * mm, "construction": true});
            skLineSegment(sketch, "E24", {"start": v(29.89, -7.62) * mm, "end": v(29.89, -8.6) * mm});
            skSolve(sketch);
        }
        {
            var Q0;
            Q0=makeQuery(id+"F10.imprint","IMPRINT",FACE,{"disambiguationData":[TD([[makeQuery(id+"F10.imprint","IMPRINT",EDGE,{"derivedFrom":sQuery(id+"F10.wireOp",EDGE,"E21.bottom")}),1.0]])]});
            var Q1;
            Q1=sQuery(id+"F10.wireOp",EDGE,"E20");
            revolve(context, id + "F11", {"surfaceOperationType" : NewSurfaceOperationType.NEW, "entities" : qUnion([Q0]), "axis" : qUnion([Q1]), "revolveType" : RevolveType.FULL});
        }
        {
            var Q0;
            Q0=qCreatedBy(makeId("Front.planeOp"),FACE);
            var sketch = newSketch(context, id + "F12", { "sketchPlane" : qUnion([Q0])});
            skLineSegment(sketch, "E25.0", {"start": v(11.38, -6.62) * mm, "end": v(39.04, -6.62) * mm, "construction": true});
            skCircle(sketch, "E26", {"center": v(20.47, -6.62) * mm, "radius": 1.2 * mm});
            skSolve(sketch);
        }
        {
            var Q0;
            Q0 = qSketchRegion(id + "F12", true);
            extrude(context, id + "F13", {"entities" : qUnion([Q0]), "operationType" : NewBodyOperationType.REMOVE, "endBound" : BoundingType.SYMMETRIC, "oppositeDirection" : true, "depth" : 25 * mm, "offsetDistance" : 25 * mm});
        }
        {
            var Q0;
            Q0=qCreatedBy(makeId("Front.planeOp"),FACE);
            var sketch = newSketch(context, id + "F14", { "sketchPlane" : qUnion([Q0])});
            skCircle(sketch, "E27", {"center": v(26.71, -6.62) * mm, "radius": 0.7 * mm});
            skSolve(sketch);
        }
        {
            var Q0;
            Q0=makeQuery(id+"F14.imprint","IMPRINT",FACE,{"disambiguationData":[TD([[makeQuery(id+"F14.imprint","IMPRINT",EDGE,{"derivedFrom":sQuery(id+"F14.wireOp",EDGE,"E27")}),1.0]])]});
            var Q1;
            Q1=sQuery(id+"F14.wireOp",EDGE,"E27");
            extrude(context, id + "F15", {"entities" : qUnion([Q0]), "operationType" : NewBodyOperationType.REMOVE, "surfaceEntities" : qUnion([Q1]), "depth" : 25 * mm, "offsetDistance" : 25 * mm});
        }
        {
            var Q0;
            Q0=qCreatedBy(id+"F0.planeOp",FACE);
            var sketch = newSketch(context, id + "F16", { "sketchPlane" : qUnion([Q0])});
            skCircle(sketch, "E28", {"center": v(0, -6.62) * mm, "radius": 1.98 * mm});
            skSolve(sketch);
        }
        {
            var Q0;
            Q0=makeQuery(id+"F16.imprint","IMPRINT",FACE,{"disambiguationData":[TD([[makeQuery(id+"F16.imprint","IMPRINT",EDGE,{"derivedFrom":sQuery(id+"F16.wireOp",EDGE,"E28")}),1.0]])]});
            var Q1;
            Q1 = qConstructionFilter(qBodyType(qCreatedBy(id + "F16" ,EDGE), BodyType.WIRE), ConstructionObject.NO);
            extrude(context, id + "F17", {"entities" : qUnion([Q0]), "operationType" : NewBodyOperationType.REMOVE, "surfaceEntities" : qUnion([Q1]), "oppositeDirection" : true, "depth" : 25 * mm, "offsetDistance" : 25 * mm});
        }
        {
            var Q0;
            Q0=qCreatedBy(id+"F0.planeOp",FACE);
            var sketch = newSketch(context, id + "F18", { "sketchPlane" : qUnion([Q0])});
            skCircle(sketch, "E29", {"center": v(0, -16.33) * mm, "radius": 1.98 * mm});
            skSolve(sketch);
        }
        {
            var Q0;
            Q0=makeQuery(id+"F18.imprint","IMPRINT",FACE,{"disambiguationData":[TD([[makeQuery(id+"F18.imprint","IMPRINT",EDGE,{"derivedFrom":sQuery(id+"F18.wireOp",EDGE,"E29")}),1.0]])]});
            extrude(context, id + "F19", {"entities" : qUnion([Q0]), "operationType" : NewBodyOperationType.REMOVE, "oppositeDirection" : true, "depth" : 25 * mm, "offsetDistance" : 25 * mm});
        }
        {
            var Q0;
            Q0=qCreatedBy(makeId("Front.planeOp"),FACE);
            var sketch = newSketch(context, id + "F20", { "sketchPlane" : qUnion([Q0])});
            skLineSegment(sketch, "E30.left", {"start": v(36.68, -6.72) * mm, "end": v(36.68, -7.23) * mm});
            skLineSegment(sketch, "E31.MirrorCS", {"start": v(37.68, -7.23) * mm, "end": v(37.68, -6.96) * mm});
            skLineSegment(sketch, "E32.MirrorCS", {"start": v(37.68, -6.96) * mm, "end": v(37.68, -6.96) * mm});
            skLineSegment(sketch, "E33.MirrorCS", {"start": v(36.68, -7.23) * mm, "end": v(37.68, -7.23) * mm});
            skArc(sketch, "E34", {"start": v(37.68, -6.96) * mm, "mid": v(37.48, -6.9) * mm, "end": v(37.36, -6.72) * mm});
            skPoint(sketch, "E35.orphan", {"position": v(36.68, -7.23) * mm});
            skLineSegment(sketch, "E36", {"start": v(36.68, -6.72) * mm, "end": v(37.36, -6.72) * mm});
            skLineSegment(sketch, "E37.0", {"start": v(11.38, -6.62) * mm, "end": v(39.04, -6.62) * mm, "construction": true});
            skLineSegment(sketch, "E38", {"start": v(37.68, -6.96) * mm, "end": v(37.68, -6.62) * mm, "construction": true});
            skSolve(sketch);
        }
        {
            var Q0;
            Q0=makeQuery(id+"F20.imprint","IMPRINT",FACE,{"disambiguationData":[TD([[makeQuery(id+"F20.imprint","IMPRINT",EDGE,{"derivedFrom":sQuery(id+"F20.wireOp",EDGE,"E30.left")}),1.0]])]});
            var Q1;
            Q1=sQuery(id+"F10.wireOp",EDGE,"E20");
            revolve(context, id + "F21", {"surfaceOperationType" : NewSurfaceOperationType.NEW, "entities" : qUnion([Q0]), "axis" : qUnion([Q1]), "revolveType" : RevolveType.FULL});
        }
        {
            var Q0;
            Q0=qCreatedBy(makeId("Front.planeOp"),FACE);
            var sketch = newSketch(context, id + "F22", { "sketchPlane" : qUnion([Q0])});
            skLineSegment(sketch, "E39.bottom", {"start": v(42.9, -6.96) * mm, "end": v(44.5, -6.96) * mm});
            skLineSegment(sketch, "E39.top", {"start": v(41.9, -7.62) * mm, "end": v(49.9, -7.62) * mm});
            skLineSegment(sketch, "E40.top", {"start": v(49.9, -8.6) * mm, "end": v(51.5, -8.6) * mm});
            skLineSegment(sketch, "E40.left", {"start": v(49.9, -7.62) * mm, "end": v(49.9, -8.6) * mm});
            skLineSegment(sketch, "E40.right", {"start": v(51.5, -7.62) * mm, "end": v(51.5, -8.6) * mm});
            skLineSegment(sketch, "E41.top", {"start": v(51.5, -7.62) * mm, "end": v(56.26, -7.62) * mm});
            skLineSegment(sketch, "E41.right", {"start": v(56.26, -7.3) * mm, "end": v(56.26, -7.62) * mm});
            skLineSegment(sketch, "E42.top", {"start": v(42.9, -7.3) * mm, "end": v(41.9, -7.3) * mm});
            skLineSegment(sketch, "E42.left", {"start": v(42.9, -6.96) * mm, "end": v(42.9, -7.3) * mm});
            skLineSegment(sketch, "E43.0", {"start": v(11.38, -6.62) * mm, "end": v(56.26, -6.62) * mm, "construction": true});
            skPoint(sketch, "E44.orphan", {"position": v(39.04, -6.62) * mm});
            skLineSegment(sketch, "E45.top", {"start": v(44.5, -7.3) * mm, "end": v(56.26, -7.3) * mm});
            skLineSegment(sketch, "E45.left", {"start": v(44.5, -6.96) * mm, "end": v(44.5, -7.3) * mm});
            skLineSegment(sketch, "E46", {"start": v(41.9, -7.3) * mm, "end": v(41.9, -7.62) * mm});
            skLineSegment(sketch, "E47", {"start": v(41.9, -7.62) * mm, "end": v(41.9, -6.62) * mm, "construction": true});
            skLineSegment(sketch, "E48", {"start": v(56.26, -7.62) * mm, "end": v(56.26, -6.62) * mm, "construction": true});
            skSolve(sketch);
        }
        {
            var Q0;
            Q0=makeQuery(id+"F22.imprint","IMPRINT",FACE,{"disambiguationData":[TD([[makeQuery(id+"F22.imprint","IMPRINT",EDGE,{"derivedFrom":sQuery(id+"F22.wireOp",EDGE,"E39.bottom")}),-1.0]])]});
            var Q1;
            Q1=sQuery(id+"F22.wireOp",EDGE,"E43.0");
            revolve(context, id + "F23", {"surfaceOperationType" : NewSurfaceOperationType.NEW, "entities" : qUnion([Q0]), "axis" : qUnion([Q1]), "revolveType" : RevolveType.FULL});
        }
        {
            var Q0;
            Q0=qCreatedBy(makeId("Front.planeOp"),FACE);
            var sketch = newSketch(context, id + "F24", { "sketchPlane" : qUnion([Q0])});
            skLineSegment(sketch, "E49", {"start": v(0, -15.75) * mm, "end": v(0, -12.38) * mm, "construction": true});
            skLineSegment(sketch, "E50.MirrorCS", {"start": v(-11.9, -12.58) * mm, "end": v(-11.5, -12.58) * mm});
            skLineSegment(sketch, "E51.MirrorCS", {"start": v(-11.9, -15.75) * mm, "end": v(-11.9, -12.58) * mm});
            skLineSegment(sketch, "E52.MirrorCS", {"start": v(-11.5, -15.75) * mm, "end": v(-11.5, -12.58) * mm});
            skLineSegment(sketch, "E53.MirrorCS", {"start": v(-11.9, -15.75) * mm, "end": v(-11.5, -15.75) * mm});
            skLineSegment(sketch, "E54.MirrorCS", {"start": v(-11.9, -15.75) * mm, "end": v(0, -15.75) * mm, "construction": true});
            skSolve(sketch);
        }
        {
            var Q0;
            Q0=makeQuery(id+"F24.imprint","IMPRINT",FACE,{"disambiguationData":[TD([[makeQuery(id+"F24.imprint","IMPRINT",EDGE,{"derivedFrom":sQuery(id+"F24.wireOp",EDGE,"E50.MirrorCS")}),-1.0]])]});
            var Q1;
            Q1=sQuery(id+"F24.wireOp",EDGE,"E49");
            revolve(context, id + "F25", {"surfaceOperationType" : NewSurfaceOperationType.NEW, "entities" : qUnion([Q0]), "axis" : qUnion([Q1]), "revolveType" : RevolveType.SYMMETRIC, "angle" : 340 * degree});
        }
    });
